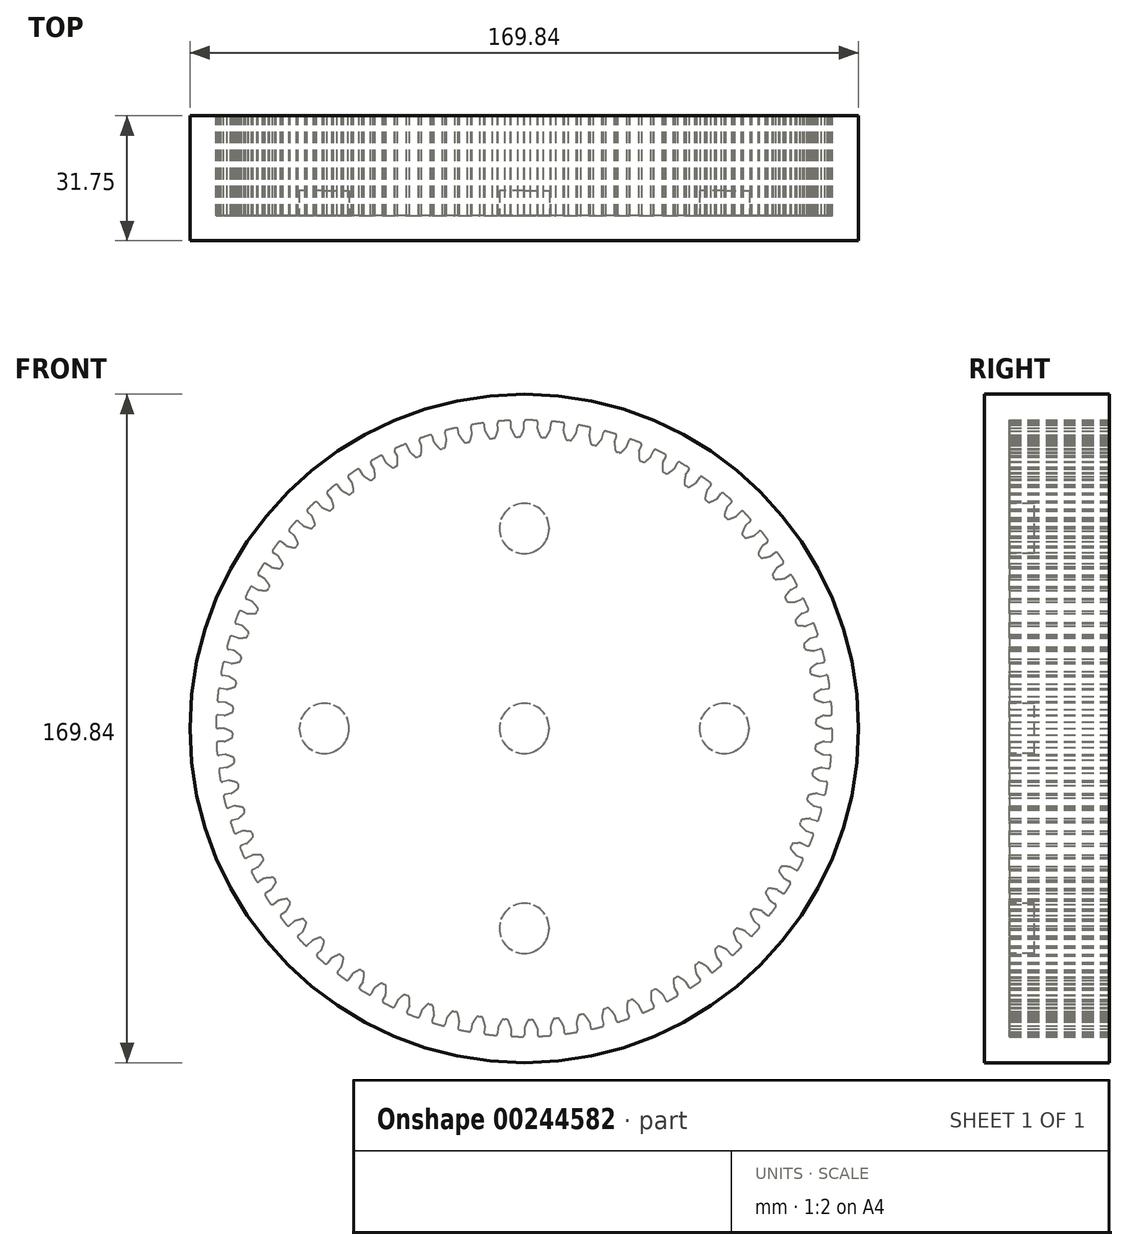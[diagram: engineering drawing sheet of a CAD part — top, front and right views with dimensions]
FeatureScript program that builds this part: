
annotation { "Feature Type Name" : "Feature", "Feature Type Description" : "" }
export const myFeature = defineFeature(function(context is Context, id is Id, definition is map)
    precondition{}
    {
        {
            var Q0;
            Q0=qCreatedBy(makeId("Front.planeOp"),FACE);
            var sketch = newSketch(context, id + "F0", { "sketchPlane" : qUnion([Q0])});
            skArc(sketch, "E0", {"start": v(-3.9, 78.22) * mm, "mid": v(-5.12, 78.15) * mm, "end": v(-6.35, 78.06) * mm});
            skArc(sketch, "E1.MirrorCS", {"start": v(-0.04, 76.1) * mm, "mid": v(-0.4, 75.22) * mm, "end": v(-0.82, 74.36) * mm});
            skPoint(sketch, "E2.end.orphan", {"position": v(-0.97, 78.31) * mm});
            skLineSegment(sketch, "E3", {"start": v(0, 76.3) * mm, "end": v(-0.03, 77.8) * mm});
            skLineSegment(sketch, "E4", {"start": v(-1.28, 74.09) * mm, "end": v(-1.62, 74.09) * mm});
            skLineSegment(sketch, "E5.MirrorCS", {"start": v(-3.33, 76.23) * mm, "end": v(-3.36, 77.73) * mm});
            skArc(sketch, "E6.MirrorCS", {"start": v(-3.28, 76.03) * mm, "mid": v(-2.87, 75.17) * mm, "end": v(-2.42, 74.33) * mm});
            skLineSegment(sketch, "E7.MirrorCS", {"start": v(-1.96, 74.07) * mm, "end": v(-1.62, 74.09) * mm});
            skPoint(sketch, "E8.visualSharp", {"position": v(-3.37, 78.25) * mm});
            skPoint(sketch, "E9.visualSharp", {"position": v(-0.05, 78.32) * mm});
            skArc(sketch, "E9.filletArc", {"start": v(0.48, 78.32) * mm, "mid": v(0.11, 78.17) * mm, "end": v(-0.03, 77.8) * mm});
            skPoint(sketch, "E10.visualSharp", {"position": v(0, 76.2) * mm});
            skArc(sketch, "E10.filletArc", {"start": v(-0.04, 76.1) * mm, "mid": v(0, 76.2) * mm, "end": v(0, 76.3) * mm});
            skPoint(sketch, "E11.visualSharp", {"position": v(-0.97, 74.09) * mm});
            skArc(sketch, "E11.filletArc", {"start": v(-1.28, 74.09) * mm, "mid": v(-1, 74.16) * mm, "end": v(-0.82, 74.36) * mm});
            skPoint(sketch, "E12.visualSharp", {"position": v(-2.27, 74.06) * mm});
            skArc(sketch, "E12.filletArc", {"start": v(-2.42, 74.33) * mm, "mid": v(-2.23, 74.13) * mm, "end": v(-1.96, 74.07) * mm});
            skPoint(sketch, "E13.visualSharp", {"position": v(-3.32, 76.13) * mm});
            skArc(sketch, "E13.filletArc", {"start": v(-3.33, 76.23) * mm, "mid": v(-3.31, 76.13) * mm, "end": v(-3.28, 76.03) * mm});
            skArc(sketch, "E14.filletArc", {"start": v(-3.36, 77.73) * mm, "mid": v(-3.52, 78.09) * mm, "end": v(-3.9, 78.22) * mm});
            skArc(sketch, "E15.1.0", {"start": v(-10.12, 77.14) * mm, "mid": v(-10.31, 77.48) * mm, "end": v(-10.7, 77.59) * mm});
            skLineSegment(sketch, "E15.1.1", {"start": v(-9.96, 75.65) * mm, "end": v(-10.12, 77.14) * mm});
            skArc(sketch, "E15.1.2", {"start": v(-9.96, 75.65) * mm, "mid": v(-9.94, 75.55) * mm, "end": v(-9.9, 75.46) * mm});
            skArc(sketch, "E15.1.3", {"start": v(-6.67, 75.81) * mm, "mid": v(-6.65, 75.91) * mm, "end": v(-6.65, 76.01) * mm});
            skLineSegment(sketch, "E15.1.4", {"start": v(-6.65, 76.01) * mm, "end": v(-6.82, 77.5) * mm});
            skArc(sketch, "E15.1.5", {"start": v(-6.35, 78.06) * mm, "mid": v(-6.7, 77.88) * mm, "end": v(-6.82, 77.5) * mm});
            skArc(sketch, "E15.1.6", {"start": v(-6.67, 75.81) * mm, "mid": v(-6.96, 74.9) * mm, "end": v(-7.3, 74) * mm});
            skArc(sketch, "E15.1.7", {"start": v(-9.9, 75.46) * mm, "mid": v(-9.42, 74.63) * mm, "end": v(-8.9, 73.83) * mm});
            skArc(sketch, "E15.1.8", {"start": v(-8.9, 73.83) * mm, "mid": v(-8.68, 73.66) * mm, "end": v(-8.4, 73.62) * mm});
            skLineSegment(sketch, "E15.1.9", {"start": v(-8.4, 73.62) * mm, "end": v(-8.07, 73.67) * mm});
            skLineSegment(sketch, "E15.1.10", {"start": v(-7.73, 73.7) * mm, "end": v(-8.07, 73.67) * mm});
            skArc(sketch, "E15.1.11", {"start": v(-7.73, 73.7) * mm, "mid": v(-7.47, 73.8) * mm, "end": v(-7.3, 74) * mm});
            skArc(sketch, "E15.2.0", {"start": v(-16.8, 75.96) * mm, "mid": v(-17.03, 76.3) * mm, "end": v(-17.42, 76.36) * mm});
            skLineSegment(sketch, "E15.2.1", {"start": v(-16.51, 74.5) * mm, "end": v(-16.8, 75.96) * mm});
            skArc(sketch, "E15.2.2", {"start": v(-16.51, 74.5) * mm, "mid": v(-16.48, 74.4) * mm, "end": v(-16.44, 74.3) * mm});
            skArc(sketch, "E15.2.3", {"start": v(-13.25, 74.94) * mm, "mid": v(-13.24, 75.04) * mm, "end": v(-13.25, 75.14) * mm});
            skLineSegment(sketch, "E15.2.4", {"start": v(-13.25, 75.14) * mm, "end": v(-13.54, 76.61) * mm});
            skArc(sketch, "E15.2.5", {"start": v(-13.13, 77.21) * mm, "mid": v(-13.46, 77) * mm, "end": v(-13.54, 76.61) * mm});
            skArc(sketch, "E15.2.6", {"start": v(-13.25, 74.94) * mm, "mid": v(-13.46, 74.01) * mm, "end": v(-13.72, 73.1) * mm});
            skArc(sketch, "E15.2.7", {"start": v(-16.44, 74.3) * mm, "mid": v(-15.88, 73.53) * mm, "end": v(-15.3, 72.78) * mm});
            skArc(sketch, "E15.2.8", {"start": v(-15.3, 72.78) * mm, "mid": v(-15.07, 72.62) * mm, "end": v(-14.8, 72.6) * mm});
            skLineSegment(sketch, "E15.2.9", {"start": v(-14.8, 72.6) * mm, "end": v(-14.46, 72.68) * mm});
            skLineSegment(sketch, "E15.2.10", {"start": v(-14.12, 72.74) * mm, "end": v(-14.46, 72.68) * mm});
            skArc(sketch, "E15.2.11", {"start": v(-14.12, 72.74) * mm, "mid": v(-13.87, 72.86) * mm, "end": v(-13.72, 73.1) * mm});
            skArc(sketch, "E15.3.0", {"start": v(-23.36, 74.21) * mm, "mid": v(-23.61, 74.52) * mm, "end": v(-24, 74.55) * mm});
            skLineSegment(sketch, "E15.3.1", {"start": v(-22.94, 72.77) * mm, "end": v(-23.36, 74.21) * mm});
            skArc(sketch, "E15.3.2", {"start": v(-22.94, 72.77) * mm, "mid": v(-22.9, 72.68) * mm, "end": v(-22.85, 72.6) * mm});
            skArc(sketch, "E15.3.3", {"start": v(-19.73, 73.5) * mm, "mid": v(-19.73, 73.6) * mm, "end": v(-19.75, 73.7) * mm});
            skLineSegment(sketch, "E15.3.4", {"start": v(-19.75, 73.7) * mm, "end": v(-20.17, 75.14) * mm});
            skArc(sketch, "E15.3.5", {"start": v(-19.81, 75.77) * mm, "mid": v(-20.12, 75.53) * mm, "end": v(-20.17, 75.14) * mm});
            skArc(sketch, "E15.3.6", {"start": v(-19.73, 73.5) * mm, "mid": v(-19.86, 72.56) * mm, "end": v(-20.04, 71.62) * mm});
            skArc(sketch, "E15.3.7", {"start": v(-22.85, 72.6) * mm, "mid": v(-22.23, 71.86) * mm, "end": v(-21.58, 71.17) * mm});
            skArc(sketch, "E15.3.8", {"start": v(-21.58, 71.17) * mm, "mid": v(-21.34, 71.03) * mm, "end": v(-21.06, 71.04) * mm});
            skLineSegment(sketch, "E15.3.9", {"start": v(-21.06, 71.04) * mm, "end": v(-20.74, 71.15) * mm});
            skLineSegment(sketch, "E15.3.10", {"start": v(-20.4, 71.23) * mm, "end": v(-20.74, 71.15) * mm});
            skArc(sketch, "E15.3.11", {"start": v(-20.4, 71.23) * mm, "mid": v(-20.17, 71.37) * mm, "end": v(-20.04, 71.62) * mm});
            skArc(sketch, "E15.4.0", {"start": v(-29.74, 71.9) * mm, "mid": v(-30.02, 72.18) * mm, "end": v(-30.41, 72.18) * mm});
            skLineSegment(sketch, "E15.4.1", {"start": v(-29.2, 70.5) * mm, "end": v(-29.74, 71.9) * mm});
            skArc(sketch, "E15.4.2", {"start": v(-29.2, 70.5) * mm, "mid": v(-29.15, 70.4) * mm, "end": v(-29.09, 70.33) * mm});
            skArc(sketch, "E15.4.3", {"start": v(-26.06, 71.5) * mm, "mid": v(-26.07, 71.6) * mm, "end": v(-26.1, 71.7) * mm});
            skLineSegment(sketch, "E15.4.4", {"start": v(-26.1, 71.7) * mm, "end": v(-26.64, 73.1) * mm});
            skArc(sketch, "E15.4.5", {"start": v(-26.34, 73.76) * mm, "mid": v(-26.63, 73.5) * mm, "end": v(-26.64, 73.1) * mm});
            skArc(sketch, "E15.4.6", {"start": v(-26.06, 71.5) * mm, "mid": v(-26.11, 70.55) * mm, "end": v(-26.2, 69.6) * mm});
            skArc(sketch, "E15.4.7", {"start": v(-29.09, 70.33) * mm, "mid": v(-28.41, 69.65) * mm, "end": v(-27.7, 69.02) * mm});
            skArc(sketch, "E15.4.8", {"start": v(-27.7, 69.02) * mm, "mid": v(-27.45, 68.9) * mm, "end": v(-27.17, 68.94) * mm});
            skLineSegment(sketch, "E15.4.9", {"start": v(-27.17, 68.94) * mm, "end": v(-26.86, 69.07) * mm});
            skLineSegment(sketch, "E15.4.10", {"start": v(-26.54, 69.18) * mm, "end": v(-26.86, 69.07) * mm});
            skArc(sketch, "E15.4.11", {"start": v(-26.54, 69.18) * mm, "mid": v(-26.31, 69.34) * mm, "end": v(-26.2, 69.6) * mm});
            skArc(sketch, "E15.5.0", {"start": v(-35.9, 69.03) * mm, "mid": v(-36.2, 69.28) * mm, "end": v(-36.59, 69.25) * mm});
            skLineSegment(sketch, "E15.5.1", {"start": v(-35.23, 67.68) * mm, "end": v(-35.9, 69.03) * mm});
            skArc(sketch, "E15.5.2", {"start": v(-35.23, 67.68) * mm, "mid": v(-35.18, 67.6) * mm, "end": v(-35.1, 67.52) * mm});
            skArc(sketch, "E15.5.3", {"start": v(-32.2, 68.96) * mm, "mid": v(-32.21, 69.06) * mm, "end": v(-32.25, 69.15) * mm});
            skLineSegment(sketch, "E15.5.4", {"start": v(-32.25, 69.15) * mm, "end": v(-32.91, 70.5) * mm});
            skArc(sketch, "E15.5.5", {"start": v(-32.67, 71.18) * mm, "mid": v(-32.93, 70.9) * mm, "end": v(-32.91, 70.5) * mm});
            skArc(sketch, "E15.5.6", {"start": v(-32.2, 68.96) * mm, "mid": v(-32.16, 68) * mm, "end": v(-32.17, 67.05) * mm});
            skArc(sketch, "E15.5.7", {"start": v(-35.1, 67.52) * mm, "mid": v(-34.37, 66.91) * mm, "end": v(-33.6, 66.34) * mm});
            skArc(sketch, "E15.5.8", {"start": v(-33.6, 66.34) * mm, "mid": v(-33.35, 66.25) * mm, "end": v(-33.08, 66.3) * mm});
            skLineSegment(sketch, "E15.5.9", {"start": v(-33.08, 66.3) * mm, "end": v(-32.78, 66.46) * mm});
            skLineSegment(sketch, "E15.5.10", {"start": v(-32.47, 66.6) * mm, "end": v(-32.78, 66.46) * mm});
            skArc(sketch, "E15.5.11", {"start": v(-32.47, 66.6) * mm, "mid": v(-32.26, 66.79) * mm, "end": v(-32.17, 67.05) * mm});
            skArc(sketch, "E15.6.0", {"start": v(-41.77, 65.63) * mm, "mid": v(-42.1, 65.87) * mm, "end": v(-42.48, 65.8) * mm});
            skLineSegment(sketch, "E15.6.1", {"start": v(-41, 64.35) * mm, "end": v(-41.77, 65.63) * mm});
            skArc(sketch, "E15.6.2", {"start": v(-41, 64.35) * mm, "mid": v(-40.93, 64.27) * mm, "end": v(-40.86, 64.2) * mm});
            skArc(sketch, "E15.6.3", {"start": v(-38.08, 65.9) * mm, "mid": v(-38.1, 65.99) * mm, "end": v(-38.15, 66.08) * mm});
            skLineSegment(sketch, "E15.6.4", {"start": v(-38.15, 66.08) * mm, "end": v(-38.93, 67.36) * mm});
            skArc(sketch, "E15.6.5", {"start": v(-38.75, 68.06) * mm, "mid": v(-38.99, 67.75) * mm, "end": v(-38.93, 67.36) * mm});
            skArc(sketch, "E15.6.6", {"start": v(-38.08, 65.9) * mm, "mid": v(-37.96, 64.94) * mm, "end": v(-37.9, 64) * mm});
            skArc(sketch, "E15.6.7", {"start": v(-40.86, 64.2) * mm, "mid": v(-40.07, 63.66) * mm, "end": v(-39.26, 63.16) * mm});
            skArc(sketch, "E15.6.8", {"start": v(-39.26, 63.16) * mm, "mid": v(-39, 63.09) * mm, "end": v(-38.73, 63.17) * mm});
            skLineSegment(sketch, "E15.6.9", {"start": v(-38.73, 63.17) * mm, "end": v(-38.44, 63.35) * mm});
            skLineSegment(sketch, "E15.6.10", {"start": v(-38.15, 63.52) * mm, "end": v(-38.44, 63.35) * mm});
            skArc(sketch, "E15.6.11", {"start": v(-38.15, 63.52) * mm, "mid": v(-37.95, 63.72) * mm, "end": v(-37.9, 64) * mm});
            skArc(sketch, "E15.7.0", {"start": v(-47.33, 61.74) * mm, "mid": v(-47.67, 61.95) * mm, "end": v(-48.06, 61.85) * mm});
            skLineSegment(sketch, "E15.7.1", {"start": v(-46.45, 60.53) * mm, "end": v(-47.33, 61.74) * mm});
            skArc(sketch, "E15.7.2", {"start": v(-46.45, 60.53) * mm, "mid": v(-46.38, 60.46) * mm, "end": v(-46.3, 60.4) * mm});
            skArc(sketch, "E15.7.3", {"start": v(-43.68, 62.32) * mm, "mid": v(-43.72, 62.41) * mm, "end": v(-43.77, 62.5) * mm});
            skLineSegment(sketch, "E15.7.4", {"start": v(-43.77, 62.5) * mm, "end": v(-44.65, 63.71) * mm});
            skArc(sketch, "E15.7.5", {"start": v(-44.53, 64.43) * mm, "mid": v(-44.74, 64.1) * mm, "end": v(-44.65, 63.71) * mm});
            skArc(sketch, "E15.7.6", {"start": v(-43.68, 62.32) * mm, "mid": v(-43.48, 61.39) * mm, "end": v(-43.32, 60.44) * mm});
            skArc(sketch, "E15.7.7", {"start": v(-46.3, 60.4) * mm, "mid": v(-45.47, 59.93) * mm, "end": v(-44.62, 59.5) * mm});
            skArc(sketch, "E15.7.8", {"start": v(-44.62, 59.5) * mm, "mid": v(-44.35, 59.45) * mm, "end": v(-44.09, 59.55) * mm});
            skLineSegment(sketch, "E15.7.9", {"start": v(-44.09, 59.55) * mm, "end": v(-43.82, 59.76) * mm});
            skLineSegment(sketch, "E15.7.10", {"start": v(-43.54, 59.96) * mm, "end": v(-43.82, 59.76) * mm});
            skArc(sketch, "E15.7.11", {"start": v(-43.54, 59.96) * mm, "mid": v(-43.36, 60.17) * mm, "end": v(-43.32, 60.44) * mm});
            skArc(sketch, "E15.8.0", {"start": v(-52.54, 57.38) * mm, "mid": v(-52.9, 57.56) * mm, "end": v(-53.26, 57.42) * mm});
            skLineSegment(sketch, "E15.8.1", {"start": v(-51.55, 56.26) * mm, "end": v(-52.54, 57.38) * mm});
            skArc(sketch, "E15.8.2", {"start": v(-51.55, 56.26) * mm, "mid": v(-51.47, 56.19) * mm, "end": v(-51.39, 56.14) * mm});
            skArc(sketch, "E15.8.3", {"start": v(-48.95, 58.28) * mm, "mid": v(-48.99, 58.37) * mm, "end": v(-49.05, 58.45) * mm});
            skLineSegment(sketch, "E15.8.4", {"start": v(-49.05, 58.45) * mm, "end": v(-50.04, 59.58) * mm});
            skArc(sketch, "E15.8.5", {"start": v(-49.98, 60.3) * mm, "mid": v(-50.16, 59.95) * mm, "end": v(-50.04, 59.58) * mm});
            skArc(sketch, "E15.8.6", {"start": v(-48.95, 58.28) * mm, "mid": v(-48.66, 57.36) * mm, "end": v(-48.43, 56.44) * mm});
            skArc(sketch, "E15.8.7", {"start": v(-51.39, 56.14) * mm, "mid": v(-50.52, 55.74) * mm, "end": v(-49.63, 55.38) * mm});
            skArc(sketch, "E15.8.8", {"start": v(-49.63, 55.38) * mm, "mid": v(-49.36, 55.36) * mm, "end": v(-49.11, 55.48) * mm});
            skLineSegment(sketch, "E15.8.9", {"start": v(-49.11, 55.48) * mm, "end": v(-48.86, 55.72) * mm});
            skLineSegment(sketch, "E15.8.10", {"start": v(-48.6, 55.93) * mm, "end": v(-48.86, 55.72) * mm});
            skArc(sketch, "E15.8.11", {"start": v(-48.6, 55.93) * mm, "mid": v(-48.44, 56.16) * mm, "end": v(-48.43, 56.44) * mm});
            skArc(sketch, "E15.9.0", {"start": v(-57.34, 52.59) * mm, "mid": v(-57.7, 52.73) * mm, "end": v(-58.06, 52.56) * mm});
            skLineSegment(sketch, "E15.9.1", {"start": v(-56.25, 51.55) * mm, "end": v(-57.34, 52.59) * mm});
            skArc(sketch, "E15.9.2", {"start": v(-56.25, 51.55) * mm, "mid": v(-56.17, 51.49) * mm, "end": v(-56.09, 51.44) * mm});
            skArc(sketch, "E15.9.3", {"start": v(-53.84, 53.79) * mm, "mid": v(-53.89, 53.88) * mm, "end": v(-53.95, 53.95) * mm});
            skLineSegment(sketch, "E15.9.4", {"start": v(-53.95, 53.95) * mm, "end": v(-55.04, 54.99) * mm});
            skArc(sketch, "E15.9.5", {"start": v(-55.04, 55.72) * mm, "mid": v(-55.2, 55.35) * mm, "end": v(-55.04, 54.99) * mm});
            skArc(sketch, "E15.9.6", {"start": v(-53.84, 53.79) * mm, "mid": v(-53.48, 52.9) * mm, "end": v(-53.16, 52) * mm});
            skArc(sketch, "E15.9.7", {"start": v(-56.09, 51.44) * mm, "mid": v(-55.19, 51.12) * mm, "end": v(-54.27, 50.84) * mm});
            skArc(sketch, "E15.9.8", {"start": v(-54.27, 50.84) * mm, "mid": v(-54, 50.85) * mm, "end": v(-53.76, 51) * mm});
            skLineSegment(sketch, "E15.9.9", {"start": v(-53.76, 51) * mm, "end": v(-53.53, 51.25) * mm});
            skLineSegment(sketch, "E15.9.10", {"start": v(-53.29, 51.49) * mm, "end": v(-53.53, 51.25) * mm});
            skArc(sketch, "E15.9.11", {"start": v(-53.29, 51.49) * mm, "mid": v(-53.15, 51.73) * mm, "end": v(-53.16, 52) * mm});
            skArc(sketch, "E15.10.0", {"start": v(-61.7, 47.39) * mm, "mid": v(-62.08, 47.5) * mm, "end": v(-62.42, 47.3) * mm});
            skLineSegment(sketch, "E15.10.1", {"start": v(-60.53, 46.45) * mm, "end": v(-61.7, 47.39) * mm});
            skArc(sketch, "E15.10.2", {"start": v(-60.53, 46.45) * mm, "mid": v(-60.45, 46.4) * mm, "end": v(-60.36, 46.36) * mm});
            skArc(sketch, "E15.10.3", {"start": v(-58.32, 48.9) * mm, "mid": v(-58.38, 48.97) * mm, "end": v(-58.45, 49.04) * mm});
            skLineSegment(sketch, "E15.10.4", {"start": v(-58.45, 49.04) * mm, "end": v(-59.62, 49.98) * mm});
            skArc(sketch, "E15.10.5", {"start": v(-59.7, 50.7) * mm, "mid": v(-59.8, 50.33) * mm, "end": v(-59.62, 49.98) * mm});
            skArc(sketch, "E15.10.6", {"start": v(-58.32, 48.9) * mm, "mid": v(-57.89, 48.04) * mm, "end": v(-57.5, 47.17) * mm});
            skArc(sketch, "E15.10.7", {"start": v(-60.36, 46.36) * mm, "mid": v(-59.43, 46.12) * mm, "end": v(-58.5, 45.92) * mm});
            skArc(sketch, "E15.10.8", {"start": v(-58.5, 45.92) * mm, "mid": v(-58.22, 45.95) * mm, "end": v(-58, 46.11) * mm});
            skLineSegment(sketch, "E15.10.9", {"start": v(-58, 46.11) * mm, "end": v(-57.8, 46.38) * mm});
            skLineSegment(sketch, "E15.10.10", {"start": v(-57.57, 46.65) * mm, "end": v(-57.8, 46.38) * mm});
            skArc(sketch, "E15.10.11", {"start": v(-57.57, 46.65) * mm, "mid": v(-57.46, 46.9) * mm, "end": v(-57.5, 47.17) * mm});
            skArc(sketch, "E15.11.0", {"start": v(-65.6, 41.83) * mm, "mid": v(-65.99, 41.9) * mm, "end": v(-66.3, 41.68) * mm});
            skLineSegment(sketch, "E15.11.1", {"start": v(-64.35, 41) * mm, "end": v(-65.6, 41.83) * mm});
            skArc(sketch, "E15.11.2", {"start": v(-64.35, 41) * mm, "mid": v(-64.26, 40.95) * mm, "end": v(-64.17, 40.92) * mm});
            skArc(sketch, "E15.11.3", {"start": v(-62.36, 43.62) * mm, "mid": v(-62.43, 43.7) * mm, "end": v(-62.5, 43.76) * mm});
            skLineSegment(sketch, "E15.11.4", {"start": v(-62.5, 43.76) * mm, "end": v(-63.75, 44.6) * mm});
            skArc(sketch, "E15.11.5", {"start": v(-63.88, 45.31) * mm, "mid": v(-63.97, 44.93) * mm, "end": v(-63.75, 44.6) * mm});
            skArc(sketch, "E15.11.6", {"start": v(-62.36, 43.62) * mm, "mid": v(-61.85, 42.81) * mm, "end": v(-61.39, 41.98) * mm});
            skArc(sketch, "E15.11.7", {"start": v(-64.17, 40.92) * mm, "mid": v(-63.22, 40.76) * mm, "end": v(-62.28, 40.65) * mm});
            skArc(sketch, "E15.11.8", {"start": v(-62.28, 40.65) * mm, "mid": v(-62, 40.7) * mm, "end": v(-61.8, 40.88) * mm});
            skLineSegment(sketch, "E15.11.9", {"start": v(-61.8, 40.88) * mm, "end": v(-61.62, 41.17) * mm});
            skLineSegment(sketch, "E15.11.10", {"start": v(-61.42, 41.45) * mm, "end": v(-61.62, 41.17) * mm});
            skArc(sketch, "E15.11.11", {"start": v(-61.42, 41.45) * mm, "mid": v(-61.33, 41.71) * mm, "end": v(-61.39, 41.98) * mm});
            skArc(sketch, "E15.12.0", {"start": v(-69, 35.96) * mm, "mid": v(-69.39, 36) * mm, "end": v(-69.7, 35.74) * mm});
            skLineSegment(sketch, "E15.12.1", {"start": v(-67.68, 35.23) * mm, "end": v(-69, 35.96) * mm});
            skArc(sketch, "E15.12.2", {"start": v(-67.68, 35.23) * mm, "mid": v(-67.59, 35.2) * mm, "end": v(-67.49, 35.17) * mm});
            skArc(sketch, "E15.12.3", {"start": v(-65.93, 38.02) * mm, "mid": v(-66, 38.1) * mm, "end": v(-66.08, 38.15) * mm});
            skLineSegment(sketch, "E15.12.4", {"start": v(-66.08, 38.15) * mm, "end": v(-67.4, 38.87) * mm});
            skArc(sketch, "E15.12.5", {"start": v(-67.59, 39.57) * mm, "mid": v(-67.64, 39.18) * mm, "end": v(-67.4, 38.87) * mm});
            skArc(sketch, "E15.12.6", {"start": v(-65.93, 38.02) * mm, "mid": v(-65.35, 37.26) * mm, "end": v(-64.81, 36.47) * mm});
            skArc(sketch, "E15.12.7", {"start": v(-67.49, 35.17) * mm, "mid": v(-66.54, 35.1) * mm, "end": v(-65.58, 35.06) * mm});
            skArc(sketch, "E15.12.8", {"start": v(-65.58, 35.06) * mm, "mid": v(-65.32, 35.14) * mm, "end": v(-65.13, 35.34) * mm});
            skLineSegment(sketch, "E15.12.9", {"start": v(-65.13, 35.34) * mm, "end": v(-64.97, 35.64) * mm});
            skLineSegment(sketch, "E15.12.10", {"start": v(-64.8, 35.94) * mm, "end": v(-64.97, 35.64) * mm});
            skArc(sketch, "E15.12.11", {"start": v(-64.8, 35.94) * mm, "mid": v(-64.73, 36.2) * mm, "end": v(-64.81, 36.47) * mm});
            skArc(sketch, "E15.13.0", {"start": v(-71.86, 29.8) * mm, "mid": v(-72.26, 29.81) * mm, "end": v(-72.54, 29.53) * mm});
            skLineSegment(sketch, "E15.13.1", {"start": v(-70.5, 29.2) * mm, "end": v(-71.86, 29.8) * mm});
            skArc(sketch, "E15.13.2", {"start": v(-70.5, 29.2) * mm, "mid": v(-70.4, 29.17) * mm, "end": v(-70.3, 29.16) * mm});
            skArc(sketch, "E15.13.3", {"start": v(-68.99, 32.13) * mm, "mid": v(-69.07, 32.2) * mm, "end": v(-69.15, 32.24) * mm});
            skLineSegment(sketch, "E15.13.4", {"start": v(-69.15, 32.24) * mm, "end": v(-70.53, 32.85) * mm});
            skArc(sketch, "E15.13.5", {"start": v(-70.78, 33.53) * mm, "mid": v(-70.8, 33.14) * mm, "end": v(-70.53, 32.85) * mm});
            skArc(sketch, "E15.13.6", {"start": v(-68.99, 32.13) * mm, "mid": v(-68.35, 31.42) * mm, "end": v(-67.74, 30.68) * mm});
            skArc(sketch, "E15.13.7", {"start": v(-70.3, 29.16) * mm, "mid": v(-69.34, 29.16) * mm, "end": v(-68.39, 29.22) * mm});
            skArc(sketch, "E15.13.8", {"start": v(-68.39, 29.22) * mm, "mid": v(-68.13, 29.31) * mm, "end": v(-67.96, 29.53) * mm});
            skLineSegment(sketch, "E15.13.9", {"start": v(-67.96, 29.53) * mm, "end": v(-67.83, 29.85) * mm});
            skLineSegment(sketch, "E15.13.10", {"start": v(-67.68, 30.15) * mm, "end": v(-67.83, 29.85) * mm});
            skArc(sketch, "E15.13.11", {"start": v(-67.68, 30.15) * mm, "mid": v(-67.64, 30.43) * mm, "end": v(-67.74, 30.68) * mm});
            skArc(sketch, "E15.14.0", {"start": v(-74.19, 23.43) * mm, "mid": v(-74.58, 23.4) * mm, "end": v(-74.84, 23.1) * mm});
            skLineSegment(sketch, "E15.14.1", {"start": v(-72.77, 22.95) * mm, "end": v(-74.19, 23.43) * mm});
            skArc(sketch, "E15.14.2", {"start": v(-72.77, 22.95) * mm, "mid": v(-72.67, 22.92) * mm, "end": v(-72.57, 22.92) * mm});
            skArc(sketch, "E15.14.3", {"start": v(-71.53, 26) * mm, "mid": v(-71.6, 26.05) * mm, "end": v(-71.7, 26.1) * mm});
            skLineSegment(sketch, "E15.14.4", {"start": v(-71.7, 26.1) * mm, "end": v(-73.12, 26.58) * mm});
            skArc(sketch, "E15.14.5", {"start": v(-73.43, 27.23) * mm, "mid": v(-73.42, 26.84) * mm, "end": v(-73.12, 26.58) * mm});
            skArc(sketch, "E15.14.6", {"start": v(-71.53, 26) * mm, "mid": v(-70.83, 25.35) * mm, "end": v(-70.16, 24.66) * mm});
            skArc(sketch, "E15.14.7", {"start": v(-72.57, 22.92) * mm, "mid": v(-71.62, 23) * mm, "end": v(-70.67, 23.14) * mm});
            skArc(sketch, "E15.14.8", {"start": v(-70.67, 23.14) * mm, "mid": v(-70.42, 23.26) * mm, "end": v(-70.27, 23.5) * mm});
            skLineSegment(sketch, "E15.14.9", {"start": v(-70.27, 23.5) * mm, "end": v(-70.17, 23.82) * mm});
            skLineSegment(sketch, "E15.14.10", {"start": v(-70.05, 24.14) * mm, "end": v(-70.17, 23.82) * mm});
            skArc(sketch, "E15.14.11", {"start": v(-70.05, 24.14) * mm, "mid": v(-70.03, 24.42) * mm, "end": v(-70.16, 24.66) * mm});
            skArc(sketch, "E15.15.0", {"start": v(-75.95, 16.87) * mm, "mid": v(-76.34, 16.81) * mm, "end": v(-76.57, 16.49) * mm});
            skLineSegment(sketch, "E15.15.1", {"start": v(-74.5, 16.52) * mm, "end": v(-75.95, 16.87) * mm});
            skArc(sketch, "E15.15.2", {"start": v(-74.5, 16.52) * mm, "mid": v(-74.4, 16.5) * mm, "end": v(-74.3, 16.5) * mm});
            skArc(sketch, "E15.15.3", {"start": v(-73.52, 19.66) * mm, "mid": v(-73.6, 19.71) * mm, "end": v(-73.7, 19.75) * mm});
            skLineSegment(sketch, "E15.15.4", {"start": v(-73.7, 19.75) * mm, "end": v(-75.16, 20.1) * mm});
            skArc(sketch, "E15.15.5", {"start": v(-75.53, 20.73) * mm, "mid": v(-75.48, 20.34) * mm, "end": v(-75.16, 20.1) * mm});
            skArc(sketch, "E15.15.6", {"start": v(-73.52, 19.66) * mm, "mid": v(-72.77, 19.08) * mm, "end": v(-72.04, 18.45) * mm});
            skArc(sketch, "E15.15.7", {"start": v(-74.3, 16.5) * mm, "mid": v(-73.35, 16.68) * mm, "end": v(-72.42, 16.9) * mm});
            skArc(sketch, "E15.15.8", {"start": v(-72.42, 16.9) * mm, "mid": v(-72.18, 17.04) * mm, "end": v(-72.05, 17.28) * mm});
            skLineSegment(sketch, "E15.15.9", {"start": v(-72.05, 17.28) * mm, "end": v(-71.98, 17.61) * mm});
            skLineSegment(sketch, "E15.15.10", {"start": v(-71.9, 17.94) * mm, "end": v(-71.98, 17.61) * mm});
            skArc(sketch, "E15.15.11", {"start": v(-71.9, 17.94) * mm, "mid": v(-71.9, 18.22) * mm, "end": v(-72.04, 18.45) * mm});
            skArc(sketch, "E15.16.0", {"start": v(-77.13, 10.19) * mm, "mid": v(-77.51, 10.1) * mm, "end": v(-77.71, 9.75) * mm});
            skLineSegment(sketch, "E15.16.1", {"start": v(-75.65, 9.96) * mm, "end": v(-77.13, 10.19) * mm});
            skArc(sketch, "E15.16.2", {"start": v(-75.65, 9.96) * mm, "mid": v(-75.55, 9.96) * mm, "end": v(-75.45, 9.97) * mm});
            skArc(sketch, "E15.16.3", {"start": v(-74.95, 13.18) * mm, "mid": v(-75.05, 13.22) * mm, "end": v(-75.14, 13.25) * mm});
            skLineSegment(sketch, "E15.16.4", {"start": v(-75.14, 13.25) * mm, "end": v(-76.62, 13.48) * mm});
            skArc(sketch, "E15.16.5", {"start": v(-77.05, 14.07) * mm, "mid": v(-76.96, 13.68) * mm, "end": v(-76.62, 13.48) * mm});
            skArc(sketch, "E15.16.6", {"start": v(-74.95, 13.18) * mm, "mid": v(-74.15, 12.66) * mm, "end": v(-73.38, 12.1) * mm});
            skArc(sketch, "E15.16.7", {"start": v(-75.45, 9.97) * mm, "mid": v(-74.53, 10.22) * mm, "end": v(-73.62, 10.52) * mm});
            skArc(sketch, "E15.16.8", {"start": v(-73.62, 10.52) * mm, "mid": v(-73.4, 10.68) * mm, "end": v(-73.29, 10.93) * mm});
            skLineSegment(sketch, "E15.16.9", {"start": v(-73.29, 10.93) * mm, "end": v(-73.24, 11.27) * mm});
            skLineSegment(sketch, "E15.16.10", {"start": v(-73.18, 11.6) * mm, "end": v(-73.24, 11.27) * mm});
            skArc(sketch, "E15.16.11", {"start": v(-73.18, 11.6) * mm, "mid": v(-73.2, 11.88) * mm, "end": v(-73.38, 12.1) * mm});
            skArc(sketch, "E15.17.0", {"start": v(-77.72, 3.43) * mm, "mid": v(-78.1, 3.3) * mm, "end": v(-78.27, 2.94) * mm});
            skLineSegment(sketch, "E15.17.1", {"start": v(-76.23, 3.33) * mm, "end": v(-77.72, 3.43) * mm});
            skArc(sketch, "E15.17.2", {"start": v(-76.23, 3.33) * mm, "mid": v(-76.13, 3.33) * mm, "end": v(-76.03, 3.36) * mm});
            skArc(sketch, "E15.17.3", {"start": v(-75.82, 6.6) * mm, "mid": v(-75.91, 6.63) * mm, "end": v(-76.01, 6.65) * mm});
            skLineSegment(sketch, "E15.17.4", {"start": v(-76.01, 6.65) * mm, "end": v(-77.5, 6.75) * mm});
            skArc(sketch, "E15.17.5", {"start": v(-77.98, 7.3) * mm, "mid": v(-77.86, 6.92) * mm, "end": v(-77.5, 6.75) * mm});
            skArc(sketch, "E15.17.6", {"start": v(-75.82, 6.6) * mm, "mid": v(-74.97, 6.15) * mm, "end": v(-74.15, 5.66) * mm});
            skArc(sketch, "E15.17.7", {"start": v(-76.03, 3.36) * mm, "mid": v(-75.13, 3.69) * mm, "end": v(-74.26, 4.06) * mm});
            skArc(sketch, "E15.17.8", {"start": v(-74.26, 4.06) * mm, "mid": v(-74.05, 4.24) * mm, "end": v(-73.96, 4.5) * mm});
            skLineSegment(sketch, "E15.17.9", {"start": v(-73.96, 4.5) * mm, "end": v(-73.95, 4.85) * mm});
            skLineSegment(sketch, "E15.17.10", {"start": v(-73.92, 5.19) * mm, "end": v(-73.95, 4.85) * mm});
            skArc(sketch, "E15.17.11", {"start": v(-73.92, 5.19) * mm, "mid": v(-73.97, 5.46) * mm, "end": v(-74.15, 5.66) * mm});
            skArc(sketch, "E15.18.0", {"start": v(-77.73, -3.36) * mm, "mid": v(-78.09, -3.52) * mm, "end": v(-78.22, -3.9) * mm});
            skLineSegment(sketch, "E15.18.1", {"start": v(-76.23, -3.33) * mm, "end": v(-77.73, -3.36) * mm});
            skArc(sketch, "E15.18.2", {"start": v(-76.23, -3.33) * mm, "mid": v(-76.13, -3.31) * mm, "end": v(-76.03, -3.28) * mm});
            skArc(sketch, "E15.18.3", {"start": v(-76.1, -0.04) * mm, "mid": v(-76.2, 0) * mm, "end": v(-76.3, 0) * mm});
            skLineSegment(sketch, "E15.18.4", {"start": v(-76.3, 0) * mm, "end": v(-77.8, -0.03) * mm});
            skArc(sketch, "E15.18.5", {"start": v(-78.32, 0.48) * mm, "mid": v(-78.17, 0.11) * mm, "end": v(-77.8, -0.03) * mm});
            skArc(sketch, "E15.18.6", {"start": v(-76.1, -0.04) * mm, "mid": v(-75.22, -0.4) * mm, "end": v(-74.36, -0.82) * mm});
            skArc(sketch, "E15.18.7", {"start": v(-76.03, -3.28) * mm, "mid": v(-75.17, -2.87) * mm, "end": v(-74.33, -2.42) * mm});
            skArc(sketch, "E15.18.8", {"start": v(-74.33, -2.42) * mm, "mid": v(-74.13, -2.23) * mm, "end": v(-74.07, -1.96) * mm});
            skLineSegment(sketch, "E15.18.9", {"start": v(-74.07, -1.96) * mm, "end": v(-74.09, -1.62) * mm});
            skLineSegment(sketch, "E15.18.10", {"start": v(-74.09, -1.28) * mm, "end": v(-74.09, -1.62) * mm});
            skArc(sketch, "E15.18.11", {"start": v(-74.09, -1.28) * mm, "mid": v(-74.16, -1) * mm, "end": v(-74.36, -0.82) * mm});
            skArc(sketch, "E15.19.0", {"start": v(-77.14, -10.12) * mm, "mid": v(-77.48, -10.31) * mm, "end": v(-77.59, -10.7) * mm});
            skLineSegment(sketch, "E15.19.1", {"start": v(-75.65, -9.96) * mm, "end": v(-77.14, -10.12) * mm});
            skArc(sketch, "E15.19.2", {"start": v(-75.65, -9.96) * mm, "mid": v(-75.55, -9.94) * mm, "end": v(-75.46, -9.9) * mm});
            skArc(sketch, "E15.19.3", {"start": v(-75.81, -6.67) * mm, "mid": v(-75.91, -6.65) * mm, "end": v(-76.01, -6.65) * mm});
            skLineSegment(sketch, "E15.19.4", {"start": v(-76.01, -6.65) * mm, "end": v(-77.5, -6.82) * mm});
            skArc(sketch, "E15.19.5", {"start": v(-78.06, -6.35) * mm, "mid": v(-77.88, -6.7) * mm, "end": v(-77.5, -6.82) * mm});
            skArc(sketch, "E15.19.6", {"start": v(-75.81, -6.67) * mm, "mid": v(-74.9, -6.96) * mm, "end": v(-74, -7.3) * mm});
            skArc(sketch, "E15.19.7", {"start": v(-75.46, -9.9) * mm, "mid": v(-74.63, -9.42) * mm, "end": v(-73.83, -8.9) * mm});
            skArc(sketch, "E15.19.8", {"start": v(-73.83, -8.9) * mm, "mid": v(-73.66, -8.68) * mm, "end": v(-73.62, -8.4) * mm});
            skLineSegment(sketch, "E15.19.9", {"start": v(-73.62, -8.4) * mm, "end": v(-73.67, -8.07) * mm});
            skLineSegment(sketch, "E15.19.10", {"start": v(-73.7, -7.73) * mm, "end": v(-73.67, -8.07) * mm});
            skArc(sketch, "E15.19.11", {"start": v(-73.7, -7.73) * mm, "mid": v(-73.8, -7.47) * mm, "end": v(-74, -7.3) * mm});
            skArc(sketch, "E15.20.0", {"start": v(-75.96, -16.8) * mm, "mid": v(-76.3, -17.03) * mm, "end": v(-76.36, -17.42) * mm});
            skLineSegment(sketch, "E15.20.1", {"start": v(-74.5, -16.51) * mm, "end": v(-75.96, -16.8) * mm});
            skArc(sketch, "E15.20.2", {"start": v(-74.5, -16.51) * mm, "mid": v(-74.4, -16.48) * mm, "end": v(-74.3, -16.44) * mm});
            skArc(sketch, "E15.20.3", {"start": v(-74.94, -13.25) * mm, "mid": v(-75.04, -13.24) * mm, "end": v(-75.14, -13.25) * mm});
            skLineSegment(sketch, "E15.20.4", {"start": v(-75.14, -13.25) * mm, "end": v(-76.61, -13.54) * mm});
            skArc(sketch, "E15.20.5", {"start": v(-77.21, -13.13) * mm, "mid": v(-77, -13.46) * mm, "end": v(-76.61, -13.54) * mm});
            skArc(sketch, "E15.20.6", {"start": v(-74.94, -13.25) * mm, "mid": v(-74.01, -13.46) * mm, "end": v(-73.1, -13.72) * mm});
            skArc(sketch, "E15.20.7", {"start": v(-74.3, -16.44) * mm, "mid": v(-73.53, -15.88) * mm, "end": v(-72.78, -15.3) * mm});
            skArc(sketch, "E15.20.8", {"start": v(-72.78, -15.3) * mm, "mid": v(-72.62, -15.07) * mm, "end": v(-72.6, -14.8) * mm});
            skLineSegment(sketch, "E15.20.9", {"start": v(-72.6, -14.8) * mm, "end": v(-72.68, -14.46) * mm});
            skLineSegment(sketch, "E15.20.10", {"start": v(-72.74, -14.12) * mm, "end": v(-72.68, -14.46) * mm});
            skArc(sketch, "E15.20.11", {"start": v(-72.74, -14.12) * mm, "mid": v(-72.86, -13.87) * mm, "end": v(-73.1, -13.72) * mm});
            skArc(sketch, "E15.21.0", {"start": v(-74.21, -23.36) * mm, "mid": v(-74.52, -23.61) * mm, "end": v(-74.55, -24) * mm});
            skLineSegment(sketch, "E15.21.1", {"start": v(-72.77, -22.94) * mm, "end": v(-74.21, -23.36) * mm});
            skArc(sketch, "E15.21.2", {"start": v(-72.77, -22.94) * mm, "mid": v(-72.68, -22.9) * mm, "end": v(-72.6, -22.85) * mm});
            skArc(sketch, "E15.21.3", {"start": v(-73.5, -19.73) * mm, "mid": v(-73.6, -19.73) * mm, "end": v(-73.7, -19.75) * mm});
            skLineSegment(sketch, "E15.21.4", {"start": v(-73.7, -19.75) * mm, "end": v(-75.14, -20.17) * mm});
            skArc(sketch, "E15.21.5", {"start": v(-75.77, -19.81) * mm, "mid": v(-75.53, -20.12) * mm, "end": v(-75.14, -20.17) * mm});
            skArc(sketch, "E15.21.6", {"start": v(-73.5, -19.73) * mm, "mid": v(-72.56, -19.86) * mm, "end": v(-71.62, -20.04) * mm});
            skArc(sketch, "E15.21.7", {"start": v(-72.6, -22.85) * mm, "mid": v(-71.86, -22.23) * mm, "end": v(-71.17, -21.58) * mm});
            skArc(sketch, "E15.21.8", {"start": v(-71.17, -21.58) * mm, "mid": v(-71.03, -21.34) * mm, "end": v(-71.04, -21.06) * mm});
            skLineSegment(sketch, "E15.21.9", {"start": v(-71.04, -21.06) * mm, "end": v(-71.15, -20.74) * mm});
            skLineSegment(sketch, "E15.21.10", {"start": v(-71.23, -20.4) * mm, "end": v(-71.15, -20.74) * mm});
            skArc(sketch, "E15.21.11", {"start": v(-71.23, -20.4) * mm, "mid": v(-71.37, -20.17) * mm, "end": v(-71.62, -20.04) * mm});
            skArc(sketch, "E15.22.0", {"start": v(-71.9, -29.74) * mm, "mid": v(-72.18, -30.02) * mm, "end": v(-72.18, -30.41) * mm});
            skLineSegment(sketch, "E15.22.1", {"start": v(-70.5, -29.2) * mm, "end": v(-71.9, -29.74) * mm});
            skArc(sketch, "E15.22.2", {"start": v(-70.5, -29.2) * mm, "mid": v(-70.4, -29.15) * mm, "end": v(-70.33, -29.09) * mm});
            skArc(sketch, "E15.22.3", {"start": v(-71.5, -26.06) * mm, "mid": v(-71.6, -26.07) * mm, "end": v(-71.7, -26.1) * mm});
            skLineSegment(sketch, "E15.22.4", {"start": v(-71.7, -26.1) * mm, "end": v(-73.1, -26.64) * mm});
            skArc(sketch, "E15.22.5", {"start": v(-73.76, -26.34) * mm, "mid": v(-73.5, -26.63) * mm, "end": v(-73.1, -26.64) * mm});
            skArc(sketch, "E15.22.6", {"start": v(-71.5, -26.06) * mm, "mid": v(-70.55, -26.11) * mm, "end": v(-69.6, -26.2) * mm});
            skArc(sketch, "E15.22.7", {"start": v(-70.33, -29.09) * mm, "mid": v(-69.65, -28.41) * mm, "end": v(-69.02, -27.7) * mm});
            skArc(sketch, "E15.22.8", {"start": v(-69.02, -27.7) * mm, "mid": v(-68.9, -27.45) * mm, "end": v(-68.94, -27.17) * mm});
            skLineSegment(sketch, "E15.22.9", {"start": v(-68.94, -27.17) * mm, "end": v(-69.07, -26.86) * mm});
            skLineSegment(sketch, "E15.22.10", {"start": v(-69.18, -26.54) * mm, "end": v(-69.07, -26.86) * mm});
            skArc(sketch, "E15.22.11", {"start": v(-69.18, -26.54) * mm, "mid": v(-69.34, -26.31) * mm, "end": v(-69.6, -26.2) * mm});
            skArc(sketch, "E15.23.0", {"start": v(-69.03, -35.9) * mm, "mid": v(-69.28, -36.2) * mm, "end": v(-69.25, -36.59) * mm});
            skLineSegment(sketch, "E15.23.1", {"start": v(-67.68, -35.23) * mm, "end": v(-69.03, -35.9) * mm});
            skArc(sketch, "E15.23.2", {"start": v(-67.68, -35.23) * mm, "mid": v(-67.6, -35.18) * mm, "end": v(-67.52, -35.1) * mm});
            skArc(sketch, "E15.23.3", {"start": v(-68.96, -32.2) * mm, "mid": v(-69.06, -32.21) * mm, "end": v(-69.15, -32.25) * mm});
            skLineSegment(sketch, "E15.23.4", {"start": v(-69.15, -32.25) * mm, "end": v(-70.5, -32.91) * mm});
            skArc(sketch, "E15.23.5", {"start": v(-71.18, -32.67) * mm, "mid": v(-70.9, -32.93) * mm, "end": v(-70.5, -32.91) * mm});
            skArc(sketch, "E15.23.6", {"start": v(-68.96, -32.2) * mm, "mid": v(-68, -32.16) * mm, "end": v(-67.05, -32.17) * mm});
            skArc(sketch, "E15.23.7", {"start": v(-67.52, -35.1) * mm, "mid": v(-66.91, -34.37) * mm, "end": v(-66.34, -33.6) * mm});
            skArc(sketch, "E15.23.8", {"start": v(-66.34, -33.6) * mm, "mid": v(-66.25, -33.35) * mm, "end": v(-66.3, -33.08) * mm});
            skLineSegment(sketch, "E15.23.9", {"start": v(-66.3, -33.08) * mm, "end": v(-66.46, -32.78) * mm});
            skLineSegment(sketch, "E15.23.10", {"start": v(-66.6, -32.47) * mm, "end": v(-66.46, -32.78) * mm});
            skArc(sketch, "E15.23.11", {"start": v(-66.6, -32.47) * mm, "mid": v(-66.79, -32.26) * mm, "end": v(-67.05, -32.17) * mm});
            skArc(sketch, "E15.24.0", {"start": v(-65.63, -41.77) * mm, "mid": v(-65.87, -42.1) * mm, "end": v(-65.8, -42.48) * mm});
            skLineSegment(sketch, "E15.24.1", {"start": v(-64.35, -41) * mm, "end": v(-65.63, -41.77) * mm});
            skArc(sketch, "E15.24.2", {"start": v(-64.35, -41) * mm, "mid": v(-64.27, -40.93) * mm, "end": v(-64.2, -40.86) * mm});
            skArc(sketch, "E15.24.3", {"start": v(-65.9, -38.08) * mm, "mid": v(-65.99, -38.1) * mm, "end": v(-66.08, -38.15) * mm});
            skLineSegment(sketch, "E15.24.4", {"start": v(-66.08, -38.15) * mm, "end": v(-67.36, -38.93) * mm});
            skArc(sketch, "E15.24.5", {"start": v(-68.06, -38.75) * mm, "mid": v(-67.75, -38.99) * mm, "end": v(-67.36, -38.93) * mm});
            skArc(sketch, "E15.24.6", {"start": v(-65.9, -38.08) * mm, "mid": v(-64.94, -37.96) * mm, "end": v(-64, -37.9) * mm});
            skArc(sketch, "E15.24.7", {"start": v(-64.2, -40.86) * mm, "mid": v(-63.66, -40.07) * mm, "end": v(-63.16, -39.26) * mm});
            skArc(sketch, "E15.24.8", {"start": v(-63.16, -39.26) * mm, "mid": v(-63.09, -39) * mm, "end": v(-63.17, -38.73) * mm});
            skLineSegment(sketch, "E15.24.9", {"start": v(-63.17, -38.73) * mm, "end": v(-63.35, -38.44) * mm});
            skLineSegment(sketch, "E15.24.10", {"start": v(-63.52, -38.15) * mm, "end": v(-63.35, -38.44) * mm});
            skArc(sketch, "E15.24.11", {"start": v(-63.52, -38.15) * mm, "mid": v(-63.72, -37.95) * mm, "end": v(-64, -37.9) * mm});
            skArc(sketch, "E15.25.0", {"start": v(-61.74, -47.33) * mm, "mid": v(-61.95, -47.67) * mm, "end": v(-61.85, -48.06) * mm});
            skLineSegment(sketch, "E15.25.1", {"start": v(-60.53, -46.45) * mm, "end": v(-61.74, -47.33) * mm});
            skArc(sketch, "E15.25.2", {"start": v(-60.53, -46.45) * mm, "mid": v(-60.46, -46.38) * mm, "end": v(-60.4, -46.3) * mm});
            skArc(sketch, "E15.25.3", {"start": v(-62.32, -43.68) * mm, "mid": v(-62.41, -43.72) * mm, "end": v(-62.5, -43.77) * mm});
            skLineSegment(sketch, "E15.25.4", {"start": v(-62.5, -43.77) * mm, "end": v(-63.71, -44.65) * mm});
            skArc(sketch, "E15.25.5", {"start": v(-64.43, -44.53) * mm, "mid": v(-64.1, -44.74) * mm, "end": v(-63.71, -44.65) * mm});
            skArc(sketch, "E15.25.6", {"start": v(-62.32, -43.68) * mm, "mid": v(-61.39, -43.48) * mm, "end": v(-60.44, -43.32) * mm});
            skArc(sketch, "E15.25.7", {"start": v(-60.4, -46.3) * mm, "mid": v(-59.93, -45.47) * mm, "end": v(-59.5, -44.62) * mm});
            skArc(sketch, "E15.25.8", {"start": v(-59.5, -44.62) * mm, "mid": v(-59.45, -44.35) * mm, "end": v(-59.55, -44.09) * mm});
            skLineSegment(sketch, "E15.25.9", {"start": v(-59.55, -44.09) * mm, "end": v(-59.76, -43.82) * mm});
            skLineSegment(sketch, "E15.25.10", {"start": v(-59.96, -43.54) * mm, "end": v(-59.76, -43.82) * mm});
            skArc(sketch, "E15.25.11", {"start": v(-59.96, -43.54) * mm, "mid": v(-60.17, -43.36) * mm, "end": v(-60.44, -43.32) * mm});
            skArc(sketch, "E15.26.0", {"start": v(-57.38, -52.54) * mm, "mid": v(-57.56, -52.9) * mm, "end": v(-57.42, -53.26) * mm});
            skLineSegment(sketch, "E15.26.1", {"start": v(-56.26, -51.55) * mm, "end": v(-57.38, -52.54) * mm});
            skArc(sketch, "E15.26.2", {"start": v(-56.26, -51.55) * mm, "mid": v(-56.19, -51.47) * mm, "end": v(-56.14, -51.39) * mm});
            skArc(sketch, "E15.26.3", {"start": v(-58.28, -48.95) * mm, "mid": v(-58.37, -48.99) * mm, "end": v(-58.45, -49.05) * mm});
            skLineSegment(sketch, "E15.26.4", {"start": v(-58.45, -49.05) * mm, "end": v(-59.58, -50.04) * mm});
            skArc(sketch, "E15.26.5", {"start": v(-60.3, -49.98) * mm, "mid": v(-59.95, -50.16) * mm, "end": v(-59.58, -50.04) * mm});
            skArc(sketch, "E15.26.6", {"start": v(-58.28, -48.95) * mm, "mid": v(-57.36, -48.66) * mm, "end": v(-56.44, -48.43) * mm});
            skArc(sketch, "E15.26.7", {"start": v(-56.14, -51.39) * mm, "mid": v(-55.74, -50.52) * mm, "end": v(-55.38, -49.63) * mm});
            skArc(sketch, "E15.26.8", {"start": v(-55.38, -49.63) * mm, "mid": v(-55.36, -49.36) * mm, "end": v(-55.48, -49.11) * mm});
            skLineSegment(sketch, "E15.26.9", {"start": v(-55.48, -49.11) * mm, "end": v(-55.72, -48.86) * mm});
            skLineSegment(sketch, "E15.26.10", {"start": v(-55.93, -48.6) * mm, "end": v(-55.72, -48.86) * mm});
            skArc(sketch, "E15.26.11", {"start": v(-55.93, -48.6) * mm, "mid": v(-56.16, -48.44) * mm, "end": v(-56.44, -48.43) * mm});
            skArc(sketch, "E15.27.0", {"start": v(-52.59, -57.34) * mm, "mid": v(-52.73, -57.7) * mm, "end": v(-52.56, -58.06) * mm});
            skLineSegment(sketch, "E15.27.1", {"start": v(-51.55, -56.25) * mm, "end": v(-52.59, -57.34) * mm});
            skArc(sketch, "E15.27.2", {"start": v(-51.55, -56.25) * mm, "mid": v(-51.49, -56.17) * mm, "end": v(-51.44, -56.09) * mm});
            skArc(sketch, "E15.27.3", {"start": v(-53.79, -53.84) * mm, "mid": v(-53.88, -53.89) * mm, "end": v(-53.95, -53.95) * mm});
            skLineSegment(sketch, "E15.27.4", {"start": v(-53.95, -53.95) * mm, "end": v(-54.99, -55.04) * mm});
            skArc(sketch, "E15.27.5", {"start": v(-55.72, -55.04) * mm, "mid": v(-55.35, -55.2) * mm, "end": v(-54.99, -55.04) * mm});
            skArc(sketch, "E15.27.6", {"start": v(-53.79, -53.84) * mm, "mid": v(-52.9, -53.48) * mm, "end": v(-52, -53.16) * mm});
            skArc(sketch, "E15.27.7", {"start": v(-51.44, -56.09) * mm, "mid": v(-51.12, -55.19) * mm, "end": v(-50.84, -54.27) * mm});
            skArc(sketch, "E15.27.8", {"start": v(-50.84, -54.27) * mm, "mid": v(-50.85, -54) * mm, "end": v(-51, -53.76) * mm});
            skLineSegment(sketch, "E15.27.9", {"start": v(-51, -53.76) * mm, "end": v(-51.25, -53.53) * mm});
            skLineSegment(sketch, "E15.27.10", {"start": v(-51.49, -53.29) * mm, "end": v(-51.25, -53.53) * mm});
            skArc(sketch, "E15.27.11", {"start": v(-51.49, -53.29) * mm, "mid": v(-51.73, -53.15) * mm, "end": v(-52, -53.16) * mm});
            skArc(sketch, "E15.28.0", {"start": v(-47.39, -61.7) * mm, "mid": v(-47.5, -62.08) * mm, "end": v(-47.3, -62.42) * mm});
            skLineSegment(sketch, "E15.28.1", {"start": v(-46.45, -60.53) * mm, "end": v(-47.39, -61.7) * mm});
            skArc(sketch, "E15.28.2", {"start": v(-46.45, -60.53) * mm, "mid": v(-46.4, -60.45) * mm, "end": v(-46.36, -60.36) * mm});
            skArc(sketch, "E15.28.3", {"start": v(-48.9, -58.32) * mm, "mid": v(-48.97, -58.38) * mm, "end": v(-49.04, -58.45) * mm});
            skLineSegment(sketch, "E15.28.4", {"start": v(-49.04, -58.45) * mm, "end": v(-49.98, -59.62) * mm});
            skArc(sketch, "E15.28.5", {"start": v(-50.7, -59.7) * mm, "mid": v(-50.33, -59.8) * mm, "end": v(-49.98, -59.62) * mm});
            skArc(sketch, "E15.28.6", {"start": v(-48.9, -58.32) * mm, "mid": v(-48.04, -57.89) * mm, "end": v(-47.17, -57.5) * mm});
            skArc(sketch, "E15.28.7", {"start": v(-46.36, -60.36) * mm, "mid": v(-46.12, -59.43) * mm, "end": v(-45.92, -58.5) * mm});
            skArc(sketch, "E15.28.8", {"start": v(-45.92, -58.5) * mm, "mid": v(-45.95, -58.22) * mm, "end": v(-46.11, -58) * mm});
            skLineSegment(sketch, "E15.28.9", {"start": v(-46.11, -58) * mm, "end": v(-46.38, -57.8) * mm});
            skLineSegment(sketch, "E15.28.10", {"start": v(-46.65, -57.57) * mm, "end": v(-46.38, -57.8) * mm});
            skArc(sketch, "E15.28.11", {"start": v(-46.65, -57.57) * mm, "mid": v(-46.9, -57.46) * mm, "end": v(-47.17, -57.5) * mm});
            skArc(sketch, "E15.29.0", {"start": v(-41.83, -65.6) * mm, "mid": v(-41.9, -65.99) * mm, "end": v(-41.68, -66.3) * mm});
            skLineSegment(sketch, "E15.29.1", {"start": v(-41, -64.35) * mm, "end": v(-41.83, -65.6) * mm});
            skArc(sketch, "E15.29.2", {"start": v(-41, -64.35) * mm, "mid": v(-40.95, -64.26) * mm, "end": v(-40.92, -64.17) * mm});
            skArc(sketch, "E15.29.3", {"start": v(-43.62, -62.36) * mm, "mid": v(-43.7, -62.43) * mm, "end": v(-43.76, -62.5) * mm});
            skLineSegment(sketch, "E15.29.4", {"start": v(-43.76, -62.5) * mm, "end": v(-44.6, -63.75) * mm});
            skArc(sketch, "E15.29.5", {"start": v(-45.31, -63.88) * mm, "mid": v(-44.93, -63.97) * mm, "end": v(-44.6, -63.75) * mm});
            skArc(sketch, "E15.29.6", {"start": v(-43.62, -62.36) * mm, "mid": v(-42.81, -61.85) * mm, "end": v(-41.98, -61.39) * mm});
            skArc(sketch, "E15.29.7", {"start": v(-40.92, -64.17) * mm, "mid": v(-40.76, -63.22) * mm, "end": v(-40.65, -62.28) * mm});
            skArc(sketch, "E15.29.8", {"start": v(-40.65, -62.28) * mm, "mid": v(-40.7, -62) * mm, "end": v(-40.88, -61.8) * mm});
            skLineSegment(sketch, "E15.29.9", {"start": v(-40.88, -61.8) * mm, "end": v(-41.17, -61.62) * mm});
            skLineSegment(sketch, "E15.29.10", {"start": v(-41.45, -61.42) * mm, "end": v(-41.17, -61.62) * mm});
            skArc(sketch, "E15.29.11", {"start": v(-41.45, -61.42) * mm, "mid": v(-41.71, -61.33) * mm, "end": v(-41.98, -61.39) * mm});
            skArc(sketch, "E15.30.0", {"start": v(-35.96, -69) * mm, "mid": v(-36, -69.39) * mm, "end": v(-35.74, -69.7) * mm});
            skLineSegment(sketch, "E15.30.1", {"start": v(-35.23, -67.68) * mm, "end": v(-35.96, -69) * mm});
            skArc(sketch, "E15.30.2", {"start": v(-35.23, -67.68) * mm, "mid": v(-35.2, -67.59) * mm, "end": v(-35.17, -67.49) * mm});
            skArc(sketch, "E15.30.3", {"start": v(-38.02, -65.93) * mm, "mid": v(-38.1, -66) * mm, "end": v(-38.15, -66.08) * mm});
            skLineSegment(sketch, "E15.30.4", {"start": v(-38.15, -66.08) * mm, "end": v(-38.87, -67.4) * mm});
            skArc(sketch, "E15.30.5", {"start": v(-39.57, -67.59) * mm, "mid": v(-39.18, -67.64) * mm, "end": v(-38.87, -67.4) * mm});
            skArc(sketch, "E15.30.6", {"start": v(-38.02, -65.93) * mm, "mid": v(-37.26, -65.35) * mm, "end": v(-36.47, -64.81) * mm});
            skArc(sketch, "E15.30.7", {"start": v(-35.17, -67.49) * mm, "mid": v(-35.1, -66.54) * mm, "end": v(-35.06, -65.58) * mm});
            skArc(sketch, "E15.30.8", {"start": v(-35.06, -65.58) * mm, "mid": v(-35.14, -65.32) * mm, "end": v(-35.34, -65.13) * mm});
            skLineSegment(sketch, "E15.30.9", {"start": v(-35.34, -65.13) * mm, "end": v(-35.64, -64.97) * mm});
            skLineSegment(sketch, "E15.30.10", {"start": v(-35.94, -64.8) * mm, "end": v(-35.64, -64.97) * mm});
            skArc(sketch, "E15.30.11", {"start": v(-35.94, -64.8) * mm, "mid": v(-36.2, -64.73) * mm, "end": v(-36.47, -64.81) * mm});
            skArc(sketch, "E15.31.0", {"start": v(-29.8, -71.86) * mm, "mid": v(-29.81, -72.26) * mm, "end": v(-29.53, -72.54) * mm});
            skLineSegment(sketch, "E15.31.1", {"start": v(-29.2, -70.5) * mm, "end": v(-29.8, -71.86) * mm});
            skArc(sketch, "E15.31.2", {"start": v(-29.2, -70.5) * mm, "mid": v(-29.17, -70.4) * mm, "end": v(-29.16, -70.3) * mm});
            skArc(sketch, "E15.31.3", {"start": v(-32.13, -68.99) * mm, "mid": v(-32.2, -69.07) * mm, "end": v(-32.24, -69.15) * mm});
            skLineSegment(sketch, "E15.31.4", {"start": v(-32.24, -69.15) * mm, "end": v(-32.85, -70.53) * mm});
            skArc(sketch, "E15.31.5", {"start": v(-33.53, -70.78) * mm, "mid": v(-33.14, -70.8) * mm, "end": v(-32.85, -70.53) * mm});
            skArc(sketch, "E15.31.6", {"start": v(-32.13, -68.99) * mm, "mid": v(-31.42, -68.35) * mm, "end": v(-30.68, -67.74) * mm});
            skArc(sketch, "E15.31.7", {"start": v(-29.16, -70.3) * mm, "mid": v(-29.16, -69.34) * mm, "end": v(-29.22, -68.39) * mm});
            skArc(sketch, "E15.31.8", {"start": v(-29.22, -68.39) * mm, "mid": v(-29.31, -68.13) * mm, "end": v(-29.53, -67.96) * mm});
            skLineSegment(sketch, "E15.31.9", {"start": v(-29.53, -67.96) * mm, "end": v(-29.85, -67.83) * mm});
            skLineSegment(sketch, "E15.31.10", {"start": v(-30.15, -67.68) * mm, "end": v(-29.85, -67.83) * mm});
            skArc(sketch, "E15.31.11", {"start": v(-30.15, -67.68) * mm, "mid": v(-30.43, -67.64) * mm, "end": v(-30.68, -67.74) * mm});
            skArc(sketch, "E15.32.0", {"start": v(-23.43, -74.19) * mm, "mid": v(-23.4, -74.58) * mm, "end": v(-23.1, -74.84) * mm});
            skLineSegment(sketch, "E15.32.1", {"start": v(-22.95, -72.77) * mm, "end": v(-23.43, -74.19) * mm});
            skArc(sketch, "E15.32.2", {"start": v(-22.95, -72.77) * mm, "mid": v(-22.92, -72.67) * mm, "end": v(-22.92, -72.57) * mm});
            skArc(sketch, "E15.32.3", {"start": v(-26, -71.53) * mm, "mid": v(-26.05, -71.6) * mm, "end": v(-26.1, -71.7) * mm});
            skLineSegment(sketch, "E15.32.4", {"start": v(-26.1, -71.7) * mm, "end": v(-26.58, -73.12) * mm});
            skArc(sketch, "E15.32.5", {"start": v(-27.23, -73.43) * mm, "mid": v(-26.84, -73.42) * mm, "end": v(-26.58, -73.12) * mm});
            skArc(sketch, "E15.32.6", {"start": v(-26, -71.53) * mm, "mid": v(-25.35, -70.83) * mm, "end": v(-24.66, -70.16) * mm});
            skArc(sketch, "E15.32.7", {"start": v(-22.92, -72.57) * mm, "mid": v(-23, -71.62) * mm, "end": v(-23.14, -70.67) * mm});
            skArc(sketch, "E15.32.8", {"start": v(-23.14, -70.67) * mm, "mid": v(-23.26, -70.42) * mm, "end": v(-23.5, -70.27) * mm});
            skLineSegment(sketch, "E15.32.9", {"start": v(-23.5, -70.27) * mm, "end": v(-23.82, -70.17) * mm});
            skLineSegment(sketch, "E15.32.10", {"start": v(-24.14, -70.05) * mm, "end": v(-23.82, -70.17) * mm});
            skArc(sketch, "E15.32.11", {"start": v(-24.14, -70.05) * mm, "mid": v(-24.42, -70.03) * mm, "end": v(-24.66, -70.16) * mm});
            skArc(sketch, "E15.33.0", {"start": v(-16.87, -75.95) * mm, "mid": v(-16.81, -76.34) * mm, "end": v(-16.49, -76.57) * mm});
            skLineSegment(sketch, "E15.33.1", {"start": v(-16.52, -74.5) * mm, "end": v(-16.87, -75.95) * mm});
            skArc(sketch, "E15.33.2", {"start": v(-16.52, -74.5) * mm, "mid": v(-16.5, -74.4) * mm, "end": v(-16.5, -74.3) * mm});
            skArc(sketch, "E15.33.3", {"start": v(-19.66, -73.52) * mm, "mid": v(-19.71, -73.6) * mm, "end": v(-19.75, -73.7) * mm});
            skLineSegment(sketch, "E15.33.4", {"start": v(-19.75, -73.7) * mm, "end": v(-20.1, -75.16) * mm});
            skArc(sketch, "E15.33.5", {"start": v(-20.73, -75.53) * mm, "mid": v(-20.34, -75.48) * mm, "end": v(-20.1, -75.16) * mm});
            skArc(sketch, "E15.33.6", {"start": v(-19.66, -73.52) * mm, "mid": v(-19.08, -72.77) * mm, "end": v(-18.45, -72.04) * mm});
            skArc(sketch, "E15.33.7", {"start": v(-16.5, -74.3) * mm, "mid": v(-16.68, -73.35) * mm, "end": v(-16.9, -72.42) * mm});
            skArc(sketch, "E15.33.8", {"start": v(-16.9, -72.42) * mm, "mid": v(-17.04, -72.18) * mm, "end": v(-17.28, -72.05) * mm});
            skLineSegment(sketch, "E15.33.9", {"start": v(-17.28, -72.05) * mm, "end": v(-17.61, -71.98) * mm});
            skLineSegment(sketch, "E15.33.10", {"start": v(-17.94, -71.9) * mm, "end": v(-17.61, -71.98) * mm});
            skArc(sketch, "E15.33.11", {"start": v(-17.94, -71.9) * mm, "mid": v(-18.22, -71.9) * mm, "end": v(-18.45, -72.04) * mm});
            skArc(sketch, "E15.34.0", {"start": v(-10.19, -77.13) * mm, "mid": v(-10.1, -77.51) * mm, "end": v(-9.75, -77.71) * mm});
            skLineSegment(sketch, "E15.34.1", {"start": v(-9.96, -75.65) * mm, "end": v(-10.19, -77.13) * mm});
            skArc(sketch, "E15.34.2", {"start": v(-9.96, -75.65) * mm, "mid": v(-9.96, -75.55) * mm, "end": v(-9.97, -75.45) * mm});
            skArc(sketch, "E15.34.3", {"start": v(-13.18, -74.95) * mm, "mid": v(-13.22, -75.05) * mm, "end": v(-13.25, -75.14) * mm});
            skLineSegment(sketch, "E15.34.4", {"start": v(-13.25, -75.14) * mm, "end": v(-13.48, -76.62) * mm});
            skArc(sketch, "E15.34.5", {"start": v(-14.07, -77.05) * mm, "mid": v(-13.68, -76.96) * mm, "end": v(-13.48, -76.62) * mm});
            skArc(sketch, "E15.34.6", {"start": v(-13.18, -74.95) * mm, "mid": v(-12.66, -74.15) * mm, "end": v(-12.1, -73.38) * mm});
            skArc(sketch, "E15.34.7", {"start": v(-9.97, -75.45) * mm, "mid": v(-10.22, -74.53) * mm, "end": v(-10.52, -73.62) * mm});
            skArc(sketch, "E15.34.8", {"start": v(-10.52, -73.62) * mm, "mid": v(-10.68, -73.4) * mm, "end": v(-10.93, -73.29) * mm});
            skLineSegment(sketch, "E15.34.9", {"start": v(-10.93, -73.29) * mm, "end": v(-11.27, -73.24) * mm});
            skLineSegment(sketch, "E15.34.10", {"start": v(-11.6, -73.18) * mm, "end": v(-11.27, -73.24) * mm});
            skArc(sketch, "E15.34.11", {"start": v(-11.6, -73.18) * mm, "mid": v(-11.88, -73.2) * mm, "end": v(-12.1, -73.38) * mm});
            skArc(sketch, "E15.35.0", {"start": v(-3.43, -77.72) * mm, "mid": v(-3.3, -78.1) * mm, "end": v(-2.94, -78.27) * mm});
            skLineSegment(sketch, "E15.35.1", {"start": v(-3.33, -76.23) * mm, "end": v(-3.43, -77.72) * mm});
            skArc(sketch, "E15.35.2", {"start": v(-3.33, -76.23) * mm, "mid": v(-3.33, -76.13) * mm, "end": v(-3.36, -76.03) * mm});
            skArc(sketch, "E15.35.3", {"start": v(-6.6, -75.82) * mm, "mid": v(-6.63, -75.91) * mm, "end": v(-6.65, -76.01) * mm});
            skLineSegment(sketch, "E15.35.4", {"start": v(-6.65, -76.01) * mm, "end": v(-6.75, -77.5) * mm});
            skArc(sketch, "E15.35.5", {"start": v(-7.3, -77.98) * mm, "mid": v(-6.92, -77.86) * mm, "end": v(-6.75, -77.5) * mm});
            skArc(sketch, "E15.35.6", {"start": v(-6.6, -75.82) * mm, "mid": v(-6.15, -74.97) * mm, "end": v(-5.66, -74.15) * mm});
            skArc(sketch, "E15.35.7", {"start": v(-3.36, -76.03) * mm, "mid": v(-3.69, -75.13) * mm, "end": v(-4.06, -74.26) * mm});
            skArc(sketch, "E15.35.8", {"start": v(-4.06, -74.26) * mm, "mid": v(-4.24, -74.05) * mm, "end": v(-4.5, -73.96) * mm});
            skLineSegment(sketch, "E15.35.9", {"start": v(-4.5, -73.96) * mm, "end": v(-4.85, -73.95) * mm});
            skLineSegment(sketch, "E15.35.10", {"start": v(-5.19, -73.92) * mm, "end": v(-4.85, -73.95) * mm});
            skArc(sketch, "E15.35.11", {"start": v(-5.19, -73.92) * mm, "mid": v(-5.46, -73.97) * mm, "end": v(-5.66, -74.15) * mm});
            skArc(sketch, "E15.36.0", {"start": v(3.36, -77.73) * mm, "mid": v(3.52, -78.09) * mm, "end": v(3.9, -78.22) * mm});
            skLineSegment(sketch, "E15.36.1", {"start": v(3.33, -76.23) * mm, "end": v(3.36, -77.73) * mm});
            skArc(sketch, "E15.36.2", {"start": v(3.33, -76.23) * mm, "mid": v(3.31, -76.13) * mm, "end": v(3.28, -76.03) * mm});
            skArc(sketch, "E15.36.3", {"start": v(0.04, -76.1) * mm, "mid": v(0, -76.2) * mm, "end": v(0, -76.3) * mm});
            skLineSegment(sketch, "E15.36.4", {"start": v(0, -76.3) * mm, "end": v(0.03, -77.8) * mm});
            skArc(sketch, "E15.36.5", {"start": v(-0.48, -78.32) * mm, "mid": v(-0.11, -78.17) * mm, "end": v(0.03, -77.8) * mm});
            skArc(sketch, "E15.36.6", {"start": v(0.04, -76.1) * mm, "mid": v(0.4, -75.22) * mm, "end": v(0.82, -74.36) * mm});
            skArc(sketch, "E15.36.7", {"start": v(3.28, -76.03) * mm, "mid": v(2.87, -75.17) * mm, "end": v(2.42, -74.33) * mm});
            skArc(sketch, "E15.36.8", {"start": v(2.42, -74.33) * mm, "mid": v(2.23, -74.13) * mm, "end": v(1.96, -74.07) * mm});
            skLineSegment(sketch, "E15.36.9", {"start": v(1.96, -74.07) * mm, "end": v(1.62, -74.09) * mm});
            skLineSegment(sketch, "E15.36.10", {"start": v(1.28, -74.09) * mm, "end": v(1.62, -74.09) * mm});
            skArc(sketch, "E15.36.11", {"start": v(1.28, -74.09) * mm, "mid": v(1, -74.16) * mm, "end": v(0.82, -74.36) * mm});
            skArc(sketch, "E15.37.0", {"start": v(10.12, -77.14) * mm, "mid": v(10.31, -77.48) * mm, "end": v(10.7, -77.59) * mm});
            skLineSegment(sketch, "E15.37.1", {"start": v(9.96, -75.65) * mm, "end": v(10.12, -77.14) * mm});
            skArc(sketch, "E15.37.2", {"start": v(9.96, -75.65) * mm, "mid": v(9.94, -75.55) * mm, "end": v(9.9, -75.46) * mm});
            skArc(sketch, "E15.37.3", {"start": v(6.67, -75.81) * mm, "mid": v(6.65, -75.91) * mm, "end": v(6.65, -76.01) * mm});
            skLineSegment(sketch, "E15.37.4", {"start": v(6.65, -76.01) * mm, "end": v(6.82, -77.5) * mm});
            skArc(sketch, "E15.37.5", {"start": v(6.35, -78.06) * mm, "mid": v(6.7, -77.88) * mm, "end": v(6.82, -77.5) * mm});
            skArc(sketch, "E15.37.6", {"start": v(6.67, -75.81) * mm, "mid": v(6.96, -74.9) * mm, "end": v(7.3, -74) * mm});
            skArc(sketch, "E15.37.7", {"start": v(9.9, -75.46) * mm, "mid": v(9.42, -74.63) * mm, "end": v(8.9, -73.83) * mm});
            skArc(sketch, "E15.37.8", {"start": v(8.9, -73.83) * mm, "mid": v(8.68, -73.66) * mm, "end": v(8.4, -73.62) * mm});
            skLineSegment(sketch, "E15.37.9", {"start": v(8.4, -73.62) * mm, "end": v(8.07, -73.67) * mm});
            skLineSegment(sketch, "E15.37.10", {"start": v(7.73, -73.7) * mm, "end": v(8.07, -73.67) * mm});
            skArc(sketch, "E15.37.11", {"start": v(7.73, -73.7) * mm, "mid": v(7.47, -73.8) * mm, "end": v(7.3, -74) * mm});
            skArc(sketch, "E15.38.0", {"start": v(16.8, -75.96) * mm, "mid": v(17.03, -76.3) * mm, "end": v(17.42, -76.36) * mm});
            skLineSegment(sketch, "E15.38.1", {"start": v(16.51, -74.5) * mm, "end": v(16.8, -75.96) * mm});
            skArc(sketch, "E15.38.2", {"start": v(16.51, -74.5) * mm, "mid": v(16.48, -74.4) * mm, "end": v(16.44, -74.3) * mm});
            skArc(sketch, "E15.38.3", {"start": v(13.25, -74.94) * mm, "mid": v(13.24, -75.04) * mm, "end": v(13.25, -75.14) * mm});
            skLineSegment(sketch, "E15.38.4", {"start": v(13.25, -75.14) * mm, "end": v(13.54, -76.61) * mm});
            skArc(sketch, "E15.38.5", {"start": v(13.13, -77.21) * mm, "mid": v(13.46, -77) * mm, "end": v(13.54, -76.61) * mm});
            skArc(sketch, "E15.38.6", {"start": v(13.25, -74.94) * mm, "mid": v(13.46, -74.01) * mm, "end": v(13.72, -73.1) * mm});
            skArc(sketch, "E15.38.7", {"start": v(16.44, -74.3) * mm, "mid": v(15.88, -73.53) * mm, "end": v(15.3, -72.78) * mm});
            skArc(sketch, "E15.38.8", {"start": v(15.3, -72.78) * mm, "mid": v(15.07, -72.62) * mm, "end": v(14.8, -72.6) * mm});
            skLineSegment(sketch, "E15.38.9", {"start": v(14.8, -72.6) * mm, "end": v(14.46, -72.68) * mm});
            skLineSegment(sketch, "E15.38.10", {"start": v(14.12, -72.74) * mm, "end": v(14.46, -72.68) * mm});
            skArc(sketch, "E15.38.11", {"start": v(14.12, -72.74) * mm, "mid": v(13.87, -72.86) * mm, "end": v(13.72, -73.1) * mm});
            skArc(sketch, "E15.39.0", {"start": v(23.36, -74.21) * mm, "mid": v(23.61, -74.52) * mm, "end": v(24, -74.55) * mm});
            skLineSegment(sketch, "E15.39.1", {"start": v(22.94, -72.77) * mm, "end": v(23.36, -74.21) * mm});
            skArc(sketch, "E15.39.2", {"start": v(22.94, -72.77) * mm, "mid": v(22.9, -72.68) * mm, "end": v(22.85, -72.6) * mm});
            skArc(sketch, "E15.39.3", {"start": v(19.73, -73.5) * mm, "mid": v(19.73, -73.6) * mm, "end": v(19.75, -73.7) * mm});
            skLineSegment(sketch, "E15.39.4", {"start": v(19.75, -73.7) * mm, "end": v(20.17, -75.14) * mm});
            skArc(sketch, "E15.39.5", {"start": v(19.81, -75.77) * mm, "mid": v(20.12, -75.53) * mm, "end": v(20.17, -75.14) * mm});
            skArc(sketch, "E15.39.6", {"start": v(19.73, -73.5) * mm, "mid": v(19.86, -72.56) * mm, "end": v(20.04, -71.62) * mm});
            skArc(sketch, "E15.39.7", {"start": v(22.85, -72.6) * mm, "mid": v(22.23, -71.86) * mm, "end": v(21.58, -71.17) * mm});
            skArc(sketch, "E15.39.8", {"start": v(21.58, -71.17) * mm, "mid": v(21.34, -71.03) * mm, "end": v(21.06, -71.04) * mm});
            skLineSegment(sketch, "E15.39.9", {"start": v(21.06, -71.04) * mm, "end": v(20.74, -71.15) * mm});
            skLineSegment(sketch, "E15.39.10", {"start": v(20.4, -71.23) * mm, "end": v(20.74, -71.15) * mm});
            skArc(sketch, "E15.39.11", {"start": v(20.4, -71.23) * mm, "mid": v(20.17, -71.37) * mm, "end": v(20.04, -71.62) * mm});
            skArc(sketch, "E15.40.0", {"start": v(29.74, -71.9) * mm, "mid": v(30.02, -72.18) * mm, "end": v(30.41, -72.18) * mm});
            skLineSegment(sketch, "E15.40.1", {"start": v(29.2, -70.5) * mm, "end": v(29.74, -71.9) * mm});
            skArc(sketch, "E15.40.2", {"start": v(29.2, -70.5) * mm, "mid": v(29.15, -70.4) * mm, "end": v(29.09, -70.33) * mm});
            skArc(sketch, "E15.40.3", {"start": v(26.06, -71.5) * mm, "mid": v(26.07, -71.6) * mm, "end": v(26.1, -71.7) * mm});
            skLineSegment(sketch, "E15.40.4", {"start": v(26.1, -71.7) * mm, "end": v(26.64, -73.1) * mm});
            skArc(sketch, "E15.40.5", {"start": v(26.34, -73.76) * mm, "mid": v(26.63, -73.5) * mm, "end": v(26.64, -73.1) * mm});
            skArc(sketch, "E15.40.6", {"start": v(26.06, -71.5) * mm, "mid": v(26.11, -70.55) * mm, "end": v(26.2, -69.6) * mm});
            skArc(sketch, "E15.40.7", {"start": v(29.09, -70.33) * mm, "mid": v(28.41, -69.65) * mm, "end": v(27.7, -69.02) * mm});
            skArc(sketch, "E15.40.8", {"start": v(27.7, -69.02) * mm, "mid": v(27.45, -68.9) * mm, "end": v(27.17, -68.94) * mm});
            skLineSegment(sketch, "E15.40.9", {"start": v(27.17, -68.94) * mm, "end": v(26.86, -69.07) * mm});
            skLineSegment(sketch, "E15.40.10", {"start": v(26.54, -69.18) * mm, "end": v(26.86, -69.07) * mm});
            skArc(sketch, "E15.40.11", {"start": v(26.54, -69.18) * mm, "mid": v(26.31, -69.34) * mm, "end": v(26.2, -69.6) * mm});
            skArc(sketch, "E15.41.0", {"start": v(35.9, -69.03) * mm, "mid": v(36.2, -69.28) * mm, "end": v(36.59, -69.25) * mm});
            skLineSegment(sketch, "E15.41.1", {"start": v(35.23, -67.68) * mm, "end": v(35.9, -69.03) * mm});
            skArc(sketch, "E15.41.2", {"start": v(35.23, -67.68) * mm, "mid": v(35.18, -67.6) * mm, "end": v(35.1, -67.52) * mm});
            skArc(sketch, "E15.41.3", {"start": v(32.2, -68.96) * mm, "mid": v(32.21, -69.06) * mm, "end": v(32.25, -69.15) * mm});
            skLineSegment(sketch, "E15.41.4", {"start": v(32.25, -69.15) * mm, "end": v(32.91, -70.5) * mm});
            skArc(sketch, "E15.41.5", {"start": v(32.67, -71.18) * mm, "mid": v(32.93, -70.9) * mm, "end": v(32.91, -70.5) * mm});
            skArc(sketch, "E15.41.6", {"start": v(32.2, -68.96) * mm, "mid": v(32.16, -68) * mm, "end": v(32.17, -67.05) * mm});
            skArc(sketch, "E15.41.7", {"start": v(35.1, -67.52) * mm, "mid": v(34.37, -66.91) * mm, "end": v(33.6, -66.34) * mm});
            skArc(sketch, "E15.41.8", {"start": v(33.6, -66.34) * mm, "mid": v(33.35, -66.25) * mm, "end": v(33.08, -66.3) * mm});
            skLineSegment(sketch, "E15.41.9", {"start": v(33.08, -66.3) * mm, "end": v(32.78, -66.46) * mm});
            skLineSegment(sketch, "E15.41.10", {"start": v(32.47, -66.6) * mm, "end": v(32.78, -66.46) * mm});
            skArc(sketch, "E15.41.11", {"start": v(32.47, -66.6) * mm, "mid": v(32.26, -66.79) * mm, "end": v(32.17, -67.05) * mm});
            skArc(sketch, "E15.42.0", {"start": v(41.77, -65.63) * mm, "mid": v(42.1, -65.87) * mm, "end": v(42.48, -65.8) * mm});
            skLineSegment(sketch, "E15.42.1", {"start": v(41, -64.35) * mm, "end": v(41.77, -65.63) * mm});
            skArc(sketch, "E15.42.2", {"start": v(41, -64.35) * mm, "mid": v(40.93, -64.27) * mm, "end": v(40.86, -64.2) * mm});
            skArc(sketch, "E15.42.3", {"start": v(38.08, -65.9) * mm, "mid": v(38.1, -65.99) * mm, "end": v(38.15, -66.08) * mm});
            skLineSegment(sketch, "E15.42.4", {"start": v(38.15, -66.08) * mm, "end": v(38.93, -67.36) * mm});
            skArc(sketch, "E15.42.5", {"start": v(38.75, -68.06) * mm, "mid": v(38.99, -67.75) * mm, "end": v(38.93, -67.36) * mm});
            skArc(sketch, "E15.42.6", {"start": v(38.08, -65.9) * mm, "mid": v(37.96, -64.94) * mm, "end": v(37.9, -64) * mm});
            skArc(sketch, "E15.42.7", {"start": v(40.86, -64.2) * mm, "mid": v(40.07, -63.66) * mm, "end": v(39.26, -63.16) * mm});
            skArc(sketch, "E15.42.8", {"start": v(39.26, -63.16) * mm, "mid": v(39, -63.09) * mm, "end": v(38.73, -63.17) * mm});
            skLineSegment(sketch, "E15.42.9", {"start": v(38.73, -63.17) * mm, "end": v(38.44, -63.35) * mm});
            skLineSegment(sketch, "E15.42.10", {"start": v(38.15, -63.52) * mm, "end": v(38.44, -63.35) * mm});
            skArc(sketch, "E15.42.11", {"start": v(38.15, -63.52) * mm, "mid": v(37.95, -63.72) * mm, "end": v(37.9, -64) * mm});
            skArc(sketch, "E15.43.0", {"start": v(47.33, -61.74) * mm, "mid": v(47.67, -61.95) * mm, "end": v(48.06, -61.85) * mm});
            skLineSegment(sketch, "E15.43.1", {"start": v(46.45, -60.53) * mm, "end": v(47.33, -61.74) * mm});
            skArc(sketch, "E15.43.2", {"start": v(46.45, -60.53) * mm, "mid": v(46.38, -60.46) * mm, "end": v(46.3, -60.4) * mm});
            skArc(sketch, "E15.43.3", {"start": v(43.68, -62.32) * mm, "mid": v(43.72, -62.41) * mm, "end": v(43.77, -62.5) * mm});
            skLineSegment(sketch, "E15.43.4", {"start": v(43.77, -62.5) * mm, "end": v(44.65, -63.71) * mm});
            skArc(sketch, "E15.43.5", {"start": v(44.53, -64.43) * mm, "mid": v(44.74, -64.1) * mm, "end": v(44.65, -63.71) * mm});
            skArc(sketch, "E15.43.6", {"start": v(43.68, -62.32) * mm, "mid": v(43.48, -61.39) * mm, "end": v(43.32, -60.44) * mm});
            skArc(sketch, "E15.43.7", {"start": v(46.3, -60.4) * mm, "mid": v(45.47, -59.93) * mm, "end": v(44.62, -59.5) * mm});
            skArc(sketch, "E15.43.8", {"start": v(44.62, -59.5) * mm, "mid": v(44.35, -59.45) * mm, "end": v(44.09, -59.55) * mm});
            skLineSegment(sketch, "E15.43.9", {"start": v(44.09, -59.55) * mm, "end": v(43.82, -59.76) * mm});
            skLineSegment(sketch, "E15.43.10", {"start": v(43.54, -59.96) * mm, "end": v(43.82, -59.76) * mm});
            skArc(sketch, "E15.43.11", {"start": v(43.54, -59.96) * mm, "mid": v(43.36, -60.17) * mm, "end": v(43.32, -60.44) * mm});
            skArc(sketch, "E15.44.0", {"start": v(52.54, -57.38) * mm, "mid": v(52.9, -57.56) * mm, "end": v(53.26, -57.42) * mm});
            skLineSegment(sketch, "E15.44.1", {"start": v(51.55, -56.26) * mm, "end": v(52.54, -57.38) * mm});
            skArc(sketch, "E15.44.2", {"start": v(51.55, -56.26) * mm, "mid": v(51.47, -56.19) * mm, "end": v(51.39, -56.14) * mm});
            skArc(sketch, "E15.44.3", {"start": v(48.95, -58.28) * mm, "mid": v(48.99, -58.37) * mm, "end": v(49.05, -58.45) * mm});
            skLineSegment(sketch, "E15.44.4", {"start": v(49.05, -58.45) * mm, "end": v(50.04, -59.58) * mm});
            skArc(sketch, "E15.44.5", {"start": v(49.98, -60.3) * mm, "mid": v(50.16, -59.95) * mm, "end": v(50.04, -59.58) * mm});
            skArc(sketch, "E15.44.6", {"start": v(48.95, -58.28) * mm, "mid": v(48.66, -57.36) * mm, "end": v(48.43, -56.44) * mm});
            skArc(sketch, "E15.44.7", {"start": v(51.39, -56.14) * mm, "mid": v(50.52, -55.74) * mm, "end": v(49.63, -55.38) * mm});
            skArc(sketch, "E15.44.8", {"start": v(49.63, -55.38) * mm, "mid": v(49.36, -55.36) * mm, "end": v(49.11, -55.48) * mm});
            skLineSegment(sketch, "E15.44.9", {"start": v(49.11, -55.48) * mm, "end": v(48.86, -55.72) * mm});
            skLineSegment(sketch, "E15.44.10", {"start": v(48.6, -55.93) * mm, "end": v(48.86, -55.72) * mm});
            skArc(sketch, "E15.44.11", {"start": v(48.6, -55.93) * mm, "mid": v(48.44, -56.16) * mm, "end": v(48.43, -56.44) * mm});
            skArc(sketch, "E15.45.0", {"start": v(57.34, -52.59) * mm, "mid": v(57.7, -52.73) * mm, "end": v(58.06, -52.56) * mm});
            skLineSegment(sketch, "E15.45.1", {"start": v(56.25, -51.55) * mm, "end": v(57.34, -52.59) * mm});
            skArc(sketch, "E15.45.2", {"start": v(56.25, -51.55) * mm, "mid": v(56.17, -51.49) * mm, "end": v(56.09, -51.44) * mm});
            skArc(sketch, "E15.45.3", {"start": v(53.84, -53.79) * mm, "mid": v(53.89, -53.88) * mm, "end": v(53.95, -53.95) * mm});
            skLineSegment(sketch, "E15.45.4", {"start": v(53.95, -53.95) * mm, "end": v(55.04, -54.99) * mm});
            skArc(sketch, "E15.45.5", {"start": v(55.04, -55.72) * mm, "mid": v(55.2, -55.35) * mm, "end": v(55.04, -54.99) * mm});
            skArc(sketch, "E15.45.6", {"start": v(53.84, -53.79) * mm, "mid": v(53.48, -52.9) * mm, "end": v(53.16, -52) * mm});
            skArc(sketch, "E15.45.7", {"start": v(56.09, -51.44) * mm, "mid": v(55.19, -51.12) * mm, "end": v(54.27, -50.84) * mm});
            skArc(sketch, "E15.45.8", {"start": v(54.27, -50.84) * mm, "mid": v(54, -50.85) * mm, "end": v(53.76, -51) * mm});
            skLineSegment(sketch, "E15.45.9", {"start": v(53.76, -51) * mm, "end": v(53.53, -51.25) * mm});
            skLineSegment(sketch, "E15.45.10", {"start": v(53.29, -51.49) * mm, "end": v(53.53, -51.25) * mm});
            skArc(sketch, "E15.45.11", {"start": v(53.29, -51.49) * mm, "mid": v(53.15, -51.73) * mm, "end": v(53.16, -52) * mm});
            skArc(sketch, "E15.46.0", {"start": v(61.7, -47.39) * mm, "mid": v(62.08, -47.5) * mm, "end": v(62.42, -47.3) * mm});
            skLineSegment(sketch, "E15.46.1", {"start": v(60.53, -46.45) * mm, "end": v(61.7, -47.39) * mm});
            skArc(sketch, "E15.46.2", {"start": v(60.53, -46.45) * mm, "mid": v(60.45, -46.4) * mm, "end": v(60.36, -46.36) * mm});
            skArc(sketch, "E15.46.3", {"start": v(58.32, -48.9) * mm, "mid": v(58.38, -48.97) * mm, "end": v(58.45, -49.04) * mm});
            skLineSegment(sketch, "E15.46.4", {"start": v(58.45, -49.04) * mm, "end": v(59.62, -49.98) * mm});
            skArc(sketch, "E15.46.5", {"start": v(59.7, -50.7) * mm, "mid": v(59.8, -50.33) * mm, "end": v(59.62, -49.98) * mm});
            skArc(sketch, "E15.46.6", {"start": v(58.32, -48.9) * mm, "mid": v(57.89, -48.04) * mm, "end": v(57.5, -47.17) * mm});
            skArc(sketch, "E15.46.7", {"start": v(60.36, -46.36) * mm, "mid": v(59.43, -46.12) * mm, "end": v(58.5, -45.92) * mm});
            skArc(sketch, "E15.46.8", {"start": v(58.5, -45.92) * mm, "mid": v(58.22, -45.95) * mm, "end": v(58, -46.11) * mm});
            skLineSegment(sketch, "E15.46.9", {"start": v(58, -46.11) * mm, "end": v(57.8, -46.38) * mm});
            skLineSegment(sketch, "E15.46.10", {"start": v(57.57, -46.65) * mm, "end": v(57.8, -46.38) * mm});
            skArc(sketch, "E15.46.11", {"start": v(57.57, -46.65) * mm, "mid": v(57.46, -46.9) * mm, "end": v(57.5, -47.17) * mm});
            skArc(sketch, "E15.47.0", {"start": v(65.6, -41.83) * mm, "mid": v(65.99, -41.9) * mm, "end": v(66.3, -41.68) * mm});
            skLineSegment(sketch, "E15.47.1", {"start": v(64.35, -41) * mm, "end": v(65.6, -41.83) * mm});
            skArc(sketch, "E15.47.2", {"start": v(64.35, -41) * mm, "mid": v(64.26, -40.95) * mm, "end": v(64.17, -40.92) * mm});
            skArc(sketch, "E15.47.3", {"start": v(62.36, -43.62) * mm, "mid": v(62.43, -43.7) * mm, "end": v(62.5, -43.76) * mm});
            skLineSegment(sketch, "E15.47.4", {"start": v(62.5, -43.76) * mm, "end": v(63.75, -44.6) * mm});
            skArc(sketch, "E15.47.5", {"start": v(63.88, -45.31) * mm, "mid": v(63.97, -44.93) * mm, "end": v(63.75, -44.6) * mm});
            skArc(sketch, "E15.47.6", {"start": v(62.36, -43.62) * mm, "mid": v(61.85, -42.81) * mm, "end": v(61.39, -41.98) * mm});
            skArc(sketch, "E15.47.7", {"start": v(64.17, -40.92) * mm, "mid": v(63.22, -40.76) * mm, "end": v(62.28, -40.65) * mm});
            skArc(sketch, "E15.47.8", {"start": v(62.28, -40.65) * mm, "mid": v(62, -40.7) * mm, "end": v(61.8, -40.88) * mm});
            skLineSegment(sketch, "E15.47.9", {"start": v(61.8, -40.88) * mm, "end": v(61.62, -41.17) * mm});
            skLineSegment(sketch, "E15.47.10", {"start": v(61.42, -41.45) * mm, "end": v(61.62, -41.17) * mm});
            skArc(sketch, "E15.47.11", {"start": v(61.42, -41.45) * mm, "mid": v(61.33, -41.71) * mm, "end": v(61.39, -41.98) * mm});
            skArc(sketch, "E15.48.0", {"start": v(69, -35.96) * mm, "mid": v(69.39, -36) * mm, "end": v(69.7, -35.74) * mm});
            skLineSegment(sketch, "E15.48.1", {"start": v(67.68, -35.23) * mm, "end": v(69, -35.96) * mm});
            skArc(sketch, "E15.48.2", {"start": v(67.68, -35.23) * mm, "mid": v(67.59, -35.2) * mm, "end": v(67.49, -35.17) * mm});
            skArc(sketch, "E15.48.3", {"start": v(65.93, -38.02) * mm, "mid": v(66, -38.1) * mm, "end": v(66.08, -38.15) * mm});
            skLineSegment(sketch, "E15.48.4", {"start": v(66.08, -38.15) * mm, "end": v(67.4, -38.87) * mm});
            skArc(sketch, "E15.48.5", {"start": v(67.59, -39.57) * mm, "mid": v(67.64, -39.18) * mm, "end": v(67.4, -38.87) * mm});
            skArc(sketch, "E15.48.6", {"start": v(65.93, -38.02) * mm, "mid": v(65.35, -37.26) * mm, "end": v(64.81, -36.47) * mm});
            skArc(sketch, "E15.48.7", {"start": v(67.49, -35.17) * mm, "mid": v(66.54, -35.1) * mm, "end": v(65.58, -35.06) * mm});
            skArc(sketch, "E15.48.8", {"start": v(65.58, -35.06) * mm, "mid": v(65.32, -35.14) * mm, "end": v(65.13, -35.34) * mm});
            skLineSegment(sketch, "E15.48.9", {"start": v(65.13, -35.34) * mm, "end": v(64.97, -35.64) * mm});
            skLineSegment(sketch, "E15.48.10", {"start": v(64.8, -35.94) * mm, "end": v(64.97, -35.64) * mm});
            skArc(sketch, "E15.48.11", {"start": v(64.8, -35.94) * mm, "mid": v(64.73, -36.2) * mm, "end": v(64.81, -36.47) * mm});
            skArc(sketch, "E15.49.0", {"start": v(71.86, -29.8) * mm, "mid": v(72.26, -29.81) * mm, "end": v(72.54, -29.53) * mm});
            skLineSegment(sketch, "E15.49.1", {"start": v(70.5, -29.2) * mm, "end": v(71.86, -29.8) * mm});
            skArc(sketch, "E15.49.2", {"start": v(70.5, -29.2) * mm, "mid": v(70.4, -29.17) * mm, "end": v(70.3, -29.16) * mm});
            skArc(sketch, "E15.49.3", {"start": v(68.99, -32.13) * mm, "mid": v(69.07, -32.2) * mm, "end": v(69.15, -32.24) * mm});
            skLineSegment(sketch, "E15.49.4", {"start": v(69.15, -32.24) * mm, "end": v(70.53, -32.85) * mm});
            skArc(sketch, "E15.49.5", {"start": v(70.78, -33.53) * mm, "mid": v(70.8, -33.14) * mm, "end": v(70.53, -32.85) * mm});
            skArc(sketch, "E15.49.6", {"start": v(68.99, -32.13) * mm, "mid": v(68.35, -31.42) * mm, "end": v(67.74, -30.68) * mm});
            skArc(sketch, "E15.49.7", {"start": v(70.3, -29.16) * mm, "mid": v(69.34, -29.16) * mm, "end": v(68.39, -29.22) * mm});
            skArc(sketch, "E15.49.8", {"start": v(68.39, -29.22) * mm, "mid": v(68.13, -29.31) * mm, "end": v(67.96, -29.53) * mm});
            skLineSegment(sketch, "E15.49.9", {"start": v(67.96, -29.53) * mm, "end": v(67.83, -29.85) * mm});
            skLineSegment(sketch, "E15.49.10", {"start": v(67.68, -30.15) * mm, "end": v(67.83, -29.85) * mm});
            skArc(sketch, "E15.49.11", {"start": v(67.68, -30.15) * mm, "mid": v(67.64, -30.43) * mm, "end": v(67.74, -30.68) * mm});
            skArc(sketch, "E15.50.0", {"start": v(74.19, -23.43) * mm, "mid": v(74.58, -23.4) * mm, "end": v(74.84, -23.1) * mm});
            skLineSegment(sketch, "E15.50.1", {"start": v(72.77, -22.95) * mm, "end": v(74.19, -23.43) * mm});
            skArc(sketch, "E15.50.2", {"start": v(72.77, -22.95) * mm, "mid": v(72.67, -22.92) * mm, "end": v(72.57, -22.92) * mm});
            skArc(sketch, "E15.50.3", {"start": v(71.53, -26) * mm, "mid": v(71.6, -26.05) * mm, "end": v(71.7, -26.1) * mm});
            skLineSegment(sketch, "E15.50.4", {"start": v(71.7, -26.1) * mm, "end": v(73.12, -26.58) * mm});
            skArc(sketch, "E15.50.5", {"start": v(73.43, -27.23) * mm, "mid": v(73.42, -26.84) * mm, "end": v(73.12, -26.58) * mm});
            skArc(sketch, "E15.50.6", {"start": v(71.53, -26) * mm, "mid": v(70.83, -25.35) * mm, "end": v(70.16, -24.66) * mm});
            skArc(sketch, "E15.50.7", {"start": v(72.57, -22.92) * mm, "mid": v(71.62, -23) * mm, "end": v(70.67, -23.14) * mm});
            skArc(sketch, "E15.50.8", {"start": v(70.67, -23.14) * mm, "mid": v(70.42, -23.26) * mm, "end": v(70.27, -23.5) * mm});
            skLineSegment(sketch, "E15.50.9", {"start": v(70.27, -23.5) * mm, "end": v(70.17, -23.82) * mm});
            skLineSegment(sketch, "E15.50.10", {"start": v(70.05, -24.14) * mm, "end": v(70.17, -23.82) * mm});
            skArc(sketch, "E15.50.11", {"start": v(70.05, -24.14) * mm, "mid": v(70.03, -24.42) * mm, "end": v(70.16, -24.66) * mm});
            skArc(sketch, "E15.51.0", {"start": v(75.95, -16.87) * mm, "mid": v(76.34, -16.81) * mm, "end": v(76.57, -16.49) * mm});
            skLineSegment(sketch, "E15.51.1", {"start": v(74.5, -16.52) * mm, "end": v(75.95, -16.87) * mm});
            skArc(sketch, "E15.51.2", {"start": v(74.5, -16.52) * mm, "mid": v(74.4, -16.5) * mm, "end": v(74.3, -16.5) * mm});
            skArc(sketch, "E15.51.3", {"start": v(73.52, -19.66) * mm, "mid": v(73.6, -19.71) * mm, "end": v(73.7, -19.75) * mm});
            skLineSegment(sketch, "E15.51.4", {"start": v(73.7, -19.75) * mm, "end": v(75.16, -20.1) * mm});
            skArc(sketch, "E15.51.5", {"start": v(75.53, -20.73) * mm, "mid": v(75.48, -20.34) * mm, "end": v(75.16, -20.1) * mm});
            skArc(sketch, "E15.51.6", {"start": v(73.52, -19.66) * mm, "mid": v(72.77, -19.08) * mm, "end": v(72.04, -18.45) * mm});
            skArc(sketch, "E15.51.7", {"start": v(74.3, -16.5) * mm, "mid": v(73.35, -16.68) * mm, "end": v(72.42, -16.9) * mm});
            skArc(sketch, "E15.51.8", {"start": v(72.42, -16.9) * mm, "mid": v(72.18, -17.04) * mm, "end": v(72.05, -17.28) * mm});
            skLineSegment(sketch, "E15.51.9", {"start": v(72.05, -17.28) * mm, "end": v(71.98, -17.61) * mm});
            skLineSegment(sketch, "E15.51.10", {"start": v(71.9, -17.94) * mm, "end": v(71.98, -17.61) * mm});
            skArc(sketch, "E15.51.11", {"start": v(71.9, -17.94) * mm, "mid": v(71.9, -18.22) * mm, "end": v(72.04, -18.45) * mm});
            skArc(sketch, "E15.52.0", {"start": v(77.13, -10.19) * mm, "mid": v(77.51, -10.1) * mm, "end": v(77.71, -9.75) * mm});
            skLineSegment(sketch, "E15.52.1", {"start": v(75.65, -9.96) * mm, "end": v(77.13, -10.19) * mm});
            skArc(sketch, "E15.52.2", {"start": v(75.65, -9.96) * mm, "mid": v(75.55, -9.96) * mm, "end": v(75.45, -9.97) * mm});
            skArc(sketch, "E15.52.3", {"start": v(74.95, -13.18) * mm, "mid": v(75.05, -13.22) * mm, "end": v(75.14, -13.25) * mm});
            skLineSegment(sketch, "E15.52.4", {"start": v(75.14, -13.25) * mm, "end": v(76.62, -13.48) * mm});
            skArc(sketch, "E15.52.5", {"start": v(77.05, -14.07) * mm, "mid": v(76.96, -13.68) * mm, "end": v(76.62, -13.48) * mm});
            skArc(sketch, "E15.52.6", {"start": v(74.95, -13.18) * mm, "mid": v(74.15, -12.66) * mm, "end": v(73.38, -12.1) * mm});
            skArc(sketch, "E15.52.7", {"start": v(75.45, -9.97) * mm, "mid": v(74.53, -10.22) * mm, "end": v(73.62, -10.52) * mm});
            skArc(sketch, "E15.52.8", {"start": v(73.62, -10.52) * mm, "mid": v(73.4, -10.68) * mm, "end": v(73.29, -10.93) * mm});
            skLineSegment(sketch, "E15.52.9", {"start": v(73.29, -10.93) * mm, "end": v(73.24, -11.27) * mm});
            skLineSegment(sketch, "E15.52.10", {"start": v(73.18, -11.6) * mm, "end": v(73.24, -11.27) * mm});
            skArc(sketch, "E15.52.11", {"start": v(73.18, -11.6) * mm, "mid": v(73.2, -11.88) * mm, "end": v(73.38, -12.1) * mm});
            skArc(sketch, "E15.53.0", {"start": v(77.72, -3.43) * mm, "mid": v(78.1, -3.3) * mm, "end": v(78.27, -2.94) * mm});
            skLineSegment(sketch, "E15.53.1", {"start": v(76.23, -3.33) * mm, "end": v(77.72, -3.43) * mm});
            skArc(sketch, "E15.53.2", {"start": v(76.23, -3.33) * mm, "mid": v(76.13, -3.33) * mm, "end": v(76.03, -3.36) * mm});
            skArc(sketch, "E15.53.3", {"start": v(75.82, -6.6) * mm, "mid": v(75.91, -6.63) * mm, "end": v(76.01, -6.65) * mm});
            skLineSegment(sketch, "E15.53.4", {"start": v(76.01, -6.65) * mm, "end": v(77.5, -6.75) * mm});
            skArc(sketch, "E15.53.5", {"start": v(77.98, -7.3) * mm, "mid": v(77.86, -6.92) * mm, "end": v(77.5, -6.75) * mm});
            skArc(sketch, "E15.53.6", {"start": v(75.82, -6.6) * mm, "mid": v(74.97, -6.15) * mm, "end": v(74.15, -5.66) * mm});
            skArc(sketch, "E15.53.7", {"start": v(76.03, -3.36) * mm, "mid": v(75.13, -3.69) * mm, "end": v(74.26, -4.06) * mm});
            skArc(sketch, "E15.53.8", {"start": v(74.26, -4.06) * mm, "mid": v(74.05, -4.24) * mm, "end": v(73.96, -4.5) * mm});
            skLineSegment(sketch, "E15.53.9", {"start": v(73.96, -4.5) * mm, "end": v(73.95, -4.85) * mm});
            skLineSegment(sketch, "E15.53.10", {"start": v(73.92, -5.19) * mm, "end": v(73.95, -4.85) * mm});
            skArc(sketch, "E15.53.11", {"start": v(73.92, -5.19) * mm, "mid": v(73.97, -5.46) * mm, "end": v(74.15, -5.66) * mm});
            skArc(sketch, "E15.54.0", {"start": v(77.73, 3.36) * mm, "mid": v(78.09, 3.52) * mm, "end": v(78.22, 3.9) * mm});
            skLineSegment(sketch, "E15.54.1", {"start": v(76.23, 3.33) * mm, "end": v(77.73, 3.36) * mm});
            skArc(sketch, "E15.54.2", {"start": v(76.23, 3.33) * mm, "mid": v(76.13, 3.31) * mm, "end": v(76.03, 3.28) * mm});
            skArc(sketch, "E15.54.3", {"start": v(76.1, 0.04) * mm, "mid": v(76.2, 0) * mm, "end": v(76.3, 0) * mm});
            skLineSegment(sketch, "E15.54.4", {"start": v(76.3, 0) * mm, "end": v(77.8, 0.03) * mm});
            skArc(sketch, "E15.54.5", {"start": v(78.32, -0.48) * mm, "mid": v(78.17, -0.11) * mm, "end": v(77.8, 0.03) * mm});
            skArc(sketch, "E15.54.6", {"start": v(76.1, 0.04) * mm, "mid": v(75.22, 0.4) * mm, "end": v(74.36, 0.82) * mm});
            skArc(sketch, "E15.54.7", {"start": v(76.03, 3.28) * mm, "mid": v(75.17, 2.87) * mm, "end": v(74.33, 2.42) * mm});
            skArc(sketch, "E15.54.8", {"start": v(74.33, 2.42) * mm, "mid": v(74.13, 2.23) * mm, "end": v(74.07, 1.96) * mm});
            skLineSegment(sketch, "E15.54.9", {"start": v(74.07, 1.96) * mm, "end": v(74.09, 1.62) * mm});
            skLineSegment(sketch, "E15.54.10", {"start": v(74.09, 1.28) * mm, "end": v(74.09, 1.62) * mm});
            skArc(sketch, "E15.54.11", {"start": v(74.09, 1.28) * mm, "mid": v(74.16, 1) * mm, "end": v(74.36, 0.82) * mm});
            skArc(sketch, "E15.55.0", {"start": v(77.14, 10.12) * mm, "mid": v(77.48, 10.31) * mm, "end": v(77.59, 10.7) * mm});
            skLineSegment(sketch, "E15.55.1", {"start": v(75.65, 9.96) * mm, "end": v(77.14, 10.12) * mm});
            skArc(sketch, "E15.55.2", {"start": v(75.65, 9.96) * mm, "mid": v(75.55, 9.94) * mm, "end": v(75.46, 9.9) * mm});
            skArc(sketch, "E15.55.3", {"start": v(75.81, 6.67) * mm, "mid": v(75.91, 6.65) * mm, "end": v(76.01, 6.65) * mm});
            skLineSegment(sketch, "E15.55.4", {"start": v(76.01, 6.65) * mm, "end": v(77.5, 6.82) * mm});
            skArc(sketch, "E15.55.5", {"start": v(78.06, 6.35) * mm, "mid": v(77.88, 6.7) * mm, "end": v(77.5, 6.82) * mm});
            skArc(sketch, "E15.55.6", {"start": v(75.81, 6.67) * mm, "mid": v(74.9, 6.96) * mm, "end": v(74, 7.3) * mm});
            skArc(sketch, "E15.55.7", {"start": v(75.46, 9.9) * mm, "mid": v(74.63, 9.42) * mm, "end": v(73.83, 8.9) * mm});
            skArc(sketch, "E15.55.8", {"start": v(73.83, 8.9) * mm, "mid": v(73.66, 8.68) * mm, "end": v(73.62, 8.4) * mm});
            skLineSegment(sketch, "E15.55.9", {"start": v(73.62, 8.4) * mm, "end": v(73.67, 8.07) * mm});
            skLineSegment(sketch, "E15.55.10", {"start": v(73.7, 7.73) * mm, "end": v(73.67, 8.07) * mm});
            skArc(sketch, "E15.55.11", {"start": v(73.7, 7.73) * mm, "mid": v(73.8, 7.47) * mm, "end": v(74, 7.3) * mm});
            skArc(sketch, "E15.56.0", {"start": v(75.96, 16.8) * mm, "mid": v(76.3, 17.03) * mm, "end": v(76.36, 17.42) * mm});
            skLineSegment(sketch, "E15.56.1", {"start": v(74.5, 16.51) * mm, "end": v(75.96, 16.8) * mm});
            skArc(sketch, "E15.56.2", {"start": v(74.5, 16.51) * mm, "mid": v(74.4, 16.48) * mm, "end": v(74.3, 16.44) * mm});
            skArc(sketch, "E15.56.3", {"start": v(74.94, 13.25) * mm, "mid": v(75.04, 13.24) * mm, "end": v(75.14, 13.25) * mm});
            skLineSegment(sketch, "E15.56.4", {"start": v(75.14, 13.25) * mm, "end": v(76.61, 13.54) * mm});
            skArc(sketch, "E15.56.5", {"start": v(77.21, 13.13) * mm, "mid": v(77, 13.46) * mm, "end": v(76.61, 13.54) * mm});
            skArc(sketch, "E15.56.6", {"start": v(74.94, 13.25) * mm, "mid": v(74.01, 13.46) * mm, "end": v(73.1, 13.72) * mm});
            skArc(sketch, "E15.56.7", {"start": v(74.3, 16.44) * mm, "mid": v(73.53, 15.88) * mm, "end": v(72.78, 15.3) * mm});
            skArc(sketch, "E15.56.8", {"start": v(72.78, 15.3) * mm, "mid": v(72.62, 15.07) * mm, "end": v(72.6, 14.8) * mm});
            skLineSegment(sketch, "E15.56.9", {"start": v(72.6, 14.8) * mm, "end": v(72.68, 14.46) * mm});
            skLineSegment(sketch, "E15.56.10", {"start": v(72.74, 14.12) * mm, "end": v(72.68, 14.46) * mm});
            skArc(sketch, "E15.56.11", {"start": v(72.74, 14.12) * mm, "mid": v(72.86, 13.87) * mm, "end": v(73.1, 13.72) * mm});
            skArc(sketch, "E15.57.0", {"start": v(74.21, 23.36) * mm, "mid": v(74.52, 23.61) * mm, "end": v(74.55, 24) * mm});
            skLineSegment(sketch, "E15.57.1", {"start": v(72.77, 22.94) * mm, "end": v(74.21, 23.36) * mm});
            skArc(sketch, "E15.57.2", {"start": v(72.77, 22.94) * mm, "mid": v(72.68, 22.9) * mm, "end": v(72.6, 22.85) * mm});
            skArc(sketch, "E15.57.3", {"start": v(73.5, 19.73) * mm, "mid": v(73.6, 19.73) * mm, "end": v(73.7, 19.75) * mm});
            skLineSegment(sketch, "E15.57.4", {"start": v(73.7, 19.75) * mm, "end": v(75.14, 20.17) * mm});
            skArc(sketch, "E15.57.5", {"start": v(75.77, 19.81) * mm, "mid": v(75.53, 20.12) * mm, "end": v(75.14, 20.17) * mm});
            skArc(sketch, "E15.57.6", {"start": v(73.5, 19.73) * mm, "mid": v(72.56, 19.86) * mm, "end": v(71.62, 20.04) * mm});
            skArc(sketch, "E15.57.7", {"start": v(72.6, 22.85) * mm, "mid": v(71.86, 22.23) * mm, "end": v(71.17, 21.58) * mm});
            skArc(sketch, "E15.57.8", {"start": v(71.17, 21.58) * mm, "mid": v(71.03, 21.34) * mm, "end": v(71.04, 21.06) * mm});
            skLineSegment(sketch, "E15.57.9", {"start": v(71.04, 21.06) * mm, "end": v(71.15, 20.74) * mm});
            skLineSegment(sketch, "E15.57.10", {"start": v(71.23, 20.4) * mm, "end": v(71.15, 20.74) * mm});
            skArc(sketch, "E15.57.11", {"start": v(71.23, 20.4) * mm, "mid": v(71.37, 20.17) * mm, "end": v(71.62, 20.04) * mm});
            skArc(sketch, "E15.58.0", {"start": v(71.9, 29.74) * mm, "mid": v(72.18, 30.02) * mm, "end": v(72.18, 30.41) * mm});
            skLineSegment(sketch, "E15.58.1", {"start": v(70.5, 29.2) * mm, "end": v(71.9, 29.74) * mm});
            skArc(sketch, "E15.58.2", {"start": v(70.5, 29.2) * mm, "mid": v(70.4, 29.15) * mm, "end": v(70.33, 29.09) * mm});
            skArc(sketch, "E15.58.3", {"start": v(71.5, 26.06) * mm, "mid": v(71.6, 26.07) * mm, "end": v(71.7, 26.1) * mm});
            skLineSegment(sketch, "E15.58.4", {"start": v(71.7, 26.1) * mm, "end": v(73.1, 26.64) * mm});
            skArc(sketch, "E15.58.5", {"start": v(73.76, 26.34) * mm, "mid": v(73.5, 26.63) * mm, "end": v(73.1, 26.64) * mm});
            skArc(sketch, "E15.58.6", {"start": v(71.5, 26.06) * mm, "mid": v(70.55, 26.11) * mm, "end": v(69.6, 26.2) * mm});
            skArc(sketch, "E15.58.7", {"start": v(70.33, 29.09) * mm, "mid": v(69.65, 28.41) * mm, "end": v(69.02, 27.7) * mm});
            skArc(sketch, "E15.58.8", {"start": v(69.02, 27.7) * mm, "mid": v(68.9, 27.45) * mm, "end": v(68.94, 27.17) * mm});
            skLineSegment(sketch, "E15.58.9", {"start": v(68.94, 27.17) * mm, "end": v(69.07, 26.86) * mm});
            skLineSegment(sketch, "E15.58.10", {"start": v(69.18, 26.54) * mm, "end": v(69.07, 26.86) * mm});
            skArc(sketch, "E15.58.11", {"start": v(69.18, 26.54) * mm, "mid": v(69.34, 26.31) * mm, "end": v(69.6, 26.2) * mm});
            skArc(sketch, "E15.59.0", {"start": v(69.03, 35.9) * mm, "mid": v(69.28, 36.2) * mm, "end": v(69.25, 36.59) * mm});
            skLineSegment(sketch, "E15.59.1", {"start": v(67.68, 35.23) * mm, "end": v(69.03, 35.9) * mm});
            skArc(sketch, "E15.59.2", {"start": v(67.68, 35.23) * mm, "mid": v(67.6, 35.18) * mm, "end": v(67.52, 35.1) * mm});
            skArc(sketch, "E15.59.3", {"start": v(68.96, 32.2) * mm, "mid": v(69.06, 32.21) * mm, "end": v(69.15, 32.25) * mm});
            skLineSegment(sketch, "E15.59.4", {"start": v(69.15, 32.25) * mm, "end": v(70.5, 32.91) * mm});
            skArc(sketch, "E15.59.5", {"start": v(71.18, 32.67) * mm, "mid": v(70.9, 32.93) * mm, "end": v(70.5, 32.91) * mm});
            skArc(sketch, "E15.59.6", {"start": v(68.96, 32.2) * mm, "mid": v(68, 32.16) * mm, "end": v(67.05, 32.17) * mm});
            skArc(sketch, "E15.59.7", {"start": v(67.52, 35.1) * mm, "mid": v(66.91, 34.37) * mm, "end": v(66.34, 33.6) * mm});
            skArc(sketch, "E15.59.8", {"start": v(66.34, 33.6) * mm, "mid": v(66.25, 33.35) * mm, "end": v(66.3, 33.08) * mm});
            skLineSegment(sketch, "E15.59.9", {"start": v(66.3, 33.08) * mm, "end": v(66.46, 32.78) * mm});
            skLineSegment(sketch, "E15.59.10", {"start": v(66.6, 32.47) * mm, "end": v(66.46, 32.78) * mm});
            skArc(sketch, "E15.59.11", {"start": v(66.6, 32.47) * mm, "mid": v(66.79, 32.26) * mm, "end": v(67.05, 32.17) * mm});
            skArc(sketch, "E15.60.0", {"start": v(65.63, 41.77) * mm, "mid": v(65.87, 42.1) * mm, "end": v(65.8, 42.48) * mm});
            skLineSegment(sketch, "E15.60.1", {"start": v(64.35, 41) * mm, "end": v(65.63, 41.77) * mm});
            skArc(sketch, "E15.60.2", {"start": v(64.35, 41) * mm, "mid": v(64.27, 40.93) * mm, "end": v(64.2, 40.86) * mm});
            skArc(sketch, "E15.60.3", {"start": v(65.9, 38.08) * mm, "mid": v(65.99, 38.1) * mm, "end": v(66.08, 38.15) * mm});
            skLineSegment(sketch, "E15.60.4", {"start": v(66.08, 38.15) * mm, "end": v(67.36, 38.93) * mm});
            skArc(sketch, "E15.60.5", {"start": v(68.06, 38.75) * mm, "mid": v(67.75, 38.99) * mm, "end": v(67.36, 38.93) * mm});
            skArc(sketch, "E15.60.6", {"start": v(65.9, 38.08) * mm, "mid": v(64.94, 37.96) * mm, "end": v(64, 37.9) * mm});
            skArc(sketch, "E15.60.7", {"start": v(64.2, 40.86) * mm, "mid": v(63.66, 40.07) * mm, "end": v(63.16, 39.26) * mm});
            skArc(sketch, "E15.60.8", {"start": v(63.16, 39.26) * mm, "mid": v(63.09, 39) * mm, "end": v(63.17, 38.73) * mm});
            skLineSegment(sketch, "E15.60.9", {"start": v(63.17, 38.73) * mm, "end": v(63.35, 38.44) * mm});
            skLineSegment(sketch, "E15.60.10", {"start": v(63.52, 38.15) * mm, "end": v(63.35, 38.44) * mm});
            skArc(sketch, "E15.60.11", {"start": v(63.52, 38.15) * mm, "mid": v(63.72, 37.95) * mm, "end": v(64, 37.9) * mm});
            skArc(sketch, "E15.61.0", {"start": v(61.74, 47.33) * mm, "mid": v(61.95, 47.67) * mm, "end": v(61.85, 48.06) * mm});
            skLineSegment(sketch, "E15.61.1", {"start": v(60.53, 46.45) * mm, "end": v(61.74, 47.33) * mm});
            skArc(sketch, "E15.61.2", {"start": v(60.53, 46.45) * mm, "mid": v(60.46, 46.38) * mm, "end": v(60.4, 46.3) * mm});
            skArc(sketch, "E15.61.3", {"start": v(62.32, 43.68) * mm, "mid": v(62.41, 43.72) * mm, "end": v(62.5, 43.77) * mm});
            skLineSegment(sketch, "E15.61.4", {"start": v(62.5, 43.77) * mm, "end": v(63.71, 44.65) * mm});
            skArc(sketch, "E15.61.5", {"start": v(64.43, 44.53) * mm, "mid": v(64.1, 44.74) * mm, "end": v(63.71, 44.65) * mm});
            skArc(sketch, "E15.61.6", {"start": v(62.32, 43.68) * mm, "mid": v(61.39, 43.48) * mm, "end": v(60.44, 43.32) * mm});
            skArc(sketch, "E15.61.7", {"start": v(60.4, 46.3) * mm, "mid": v(59.93, 45.47) * mm, "end": v(59.5, 44.62) * mm});
            skArc(sketch, "E15.61.8", {"start": v(59.5, 44.62) * mm, "mid": v(59.45, 44.35) * mm, "end": v(59.55, 44.09) * mm});
            skLineSegment(sketch, "E15.61.9", {"start": v(59.55, 44.09) * mm, "end": v(59.76, 43.82) * mm});
            skLineSegment(sketch, "E15.61.10", {"start": v(59.96, 43.54) * mm, "end": v(59.76, 43.82) * mm});
            skArc(sketch, "E15.61.11", {"start": v(59.96, 43.54) * mm, "mid": v(60.17, 43.36) * mm, "end": v(60.44, 43.32) * mm});
            skArc(sketch, "E15.62.0", {"start": v(57.38, 52.54) * mm, "mid": v(57.56, 52.9) * mm, "end": v(57.42, 53.26) * mm});
            skLineSegment(sketch, "E15.62.1", {"start": v(56.26, 51.55) * mm, "end": v(57.38, 52.54) * mm});
            skArc(sketch, "E15.62.2", {"start": v(56.26, 51.55) * mm, "mid": v(56.19, 51.47) * mm, "end": v(56.14, 51.39) * mm});
            skArc(sketch, "E15.62.3", {"start": v(58.28, 48.95) * mm, "mid": v(58.37, 48.99) * mm, "end": v(58.45, 49.05) * mm});
            skLineSegment(sketch, "E15.62.4", {"start": v(58.45, 49.05) * mm, "end": v(59.58, 50.04) * mm});
            skArc(sketch, "E15.62.5", {"start": v(60.3, 49.98) * mm, "mid": v(59.95, 50.16) * mm, "end": v(59.58, 50.04) * mm});
            skArc(sketch, "E15.62.6", {"start": v(58.28, 48.95) * mm, "mid": v(57.36, 48.66) * mm, "end": v(56.44, 48.43) * mm});
            skArc(sketch, "E15.62.7", {"start": v(56.14, 51.39) * mm, "mid": v(55.74, 50.52) * mm, "end": v(55.38, 49.63) * mm});
            skArc(sketch, "E15.62.8", {"start": v(55.38, 49.63) * mm, "mid": v(55.36, 49.36) * mm, "end": v(55.48, 49.11) * mm});
            skLineSegment(sketch, "E15.62.9", {"start": v(55.48, 49.11) * mm, "end": v(55.72, 48.86) * mm});
            skLineSegment(sketch, "E15.62.10", {"start": v(55.93, 48.6) * mm, "end": v(55.72, 48.86) * mm});
            skArc(sketch, "E15.62.11", {"start": v(55.93, 48.6) * mm, "mid": v(56.16, 48.44) * mm, "end": v(56.44, 48.43) * mm});
            skArc(sketch, "E15.63.0", {"start": v(52.59, 57.34) * mm, "mid": v(52.73, 57.7) * mm, "end": v(52.56, 58.06) * mm});
            skLineSegment(sketch, "E15.63.1", {"start": v(51.55, 56.25) * mm, "end": v(52.59, 57.34) * mm});
            skArc(sketch, "E15.63.2", {"start": v(51.55, 56.25) * mm, "mid": v(51.49, 56.17) * mm, "end": v(51.44, 56.09) * mm});
            skArc(sketch, "E15.63.3", {"start": v(53.79, 53.84) * mm, "mid": v(53.88, 53.89) * mm, "end": v(53.95, 53.95) * mm});
            skLineSegment(sketch, "E15.63.4", {"start": v(53.95, 53.95) * mm, "end": v(54.99, 55.04) * mm});
            skArc(sketch, "E15.63.5", {"start": v(55.72, 55.04) * mm, "mid": v(55.35, 55.2) * mm, "end": v(54.99, 55.04) * mm});
            skArc(sketch, "E15.63.6", {"start": v(53.79, 53.84) * mm, "mid": v(52.9, 53.48) * mm, "end": v(52, 53.16) * mm});
            skArc(sketch, "E15.63.7", {"start": v(51.44, 56.09) * mm, "mid": v(51.12, 55.19) * mm, "end": v(50.84, 54.27) * mm});
            skArc(sketch, "E15.63.8", {"start": v(50.84, 54.27) * mm, "mid": v(50.85, 54) * mm, "end": v(51, 53.76) * mm});
            skLineSegment(sketch, "E15.63.9", {"start": v(51, 53.76) * mm, "end": v(51.25, 53.53) * mm});
            skLineSegment(sketch, "E15.63.10", {"start": v(51.49, 53.29) * mm, "end": v(51.25, 53.53) * mm});
            skArc(sketch, "E15.63.11", {"start": v(51.49, 53.29) * mm, "mid": v(51.73, 53.15) * mm, "end": v(52, 53.16) * mm});
            skArc(sketch, "E15.64.0", {"start": v(47.39, 61.7) * mm, "mid": v(47.5, 62.08) * mm, "end": v(47.3, 62.42) * mm});
            skLineSegment(sketch, "E15.64.1", {"start": v(46.45, 60.53) * mm, "end": v(47.39, 61.7) * mm});
            skArc(sketch, "E15.64.2", {"start": v(46.45, 60.53) * mm, "mid": v(46.4, 60.45) * mm, "end": v(46.36, 60.36) * mm});
            skArc(sketch, "E15.64.3", {"start": v(48.9, 58.32) * mm, "mid": v(48.97, 58.38) * mm, "end": v(49.04, 58.45) * mm});
            skLineSegment(sketch, "E15.64.4", {"start": v(49.04, 58.45) * mm, "end": v(49.98, 59.62) * mm});
            skArc(sketch, "E15.64.5", {"start": v(50.7, 59.7) * mm, "mid": v(50.33, 59.8) * mm, "end": v(49.98, 59.62) * mm});
            skArc(sketch, "E15.64.6", {"start": v(48.9, 58.32) * mm, "mid": v(48.04, 57.89) * mm, "end": v(47.17, 57.5) * mm});
            skArc(sketch, "E15.64.7", {"start": v(46.36, 60.36) * mm, "mid": v(46.12, 59.43) * mm, "end": v(45.92, 58.5) * mm});
            skArc(sketch, "E15.64.8", {"start": v(45.92, 58.5) * mm, "mid": v(45.95, 58.22) * mm, "end": v(46.11, 58) * mm});
            skLineSegment(sketch, "E15.64.9", {"start": v(46.11, 58) * mm, "end": v(46.38, 57.8) * mm});
            skLineSegment(sketch, "E15.64.10", {"start": v(46.65, 57.57) * mm, "end": v(46.38, 57.8) * mm});
            skArc(sketch, "E15.64.11", {"start": v(46.65, 57.57) * mm, "mid": v(46.9, 57.46) * mm, "end": v(47.17, 57.5) * mm});
            skArc(sketch, "E15.65.0", {"start": v(41.83, 65.6) * mm, "mid": v(41.9, 65.99) * mm, "end": v(41.68, 66.3) * mm});
            skLineSegment(sketch, "E15.65.1", {"start": v(41, 64.35) * mm, "end": v(41.83, 65.6) * mm});
            skArc(sketch, "E15.65.2", {"start": v(41, 64.35) * mm, "mid": v(40.95, 64.26) * mm, "end": v(40.92, 64.17) * mm});
            skArc(sketch, "E15.65.3", {"start": v(43.62, 62.36) * mm, "mid": v(43.7, 62.43) * mm, "end": v(43.76, 62.5) * mm});
            skLineSegment(sketch, "E15.65.4", {"start": v(43.76, 62.5) * mm, "end": v(44.6, 63.75) * mm});
            skArc(sketch, "E15.65.5", {"start": v(45.31, 63.88) * mm, "mid": v(44.93, 63.97) * mm, "end": v(44.6, 63.75) * mm});
            skArc(sketch, "E15.65.6", {"start": v(43.62, 62.36) * mm, "mid": v(42.81, 61.85) * mm, "end": v(41.98, 61.39) * mm});
            skArc(sketch, "E15.65.7", {"start": v(40.92, 64.17) * mm, "mid": v(40.76, 63.22) * mm, "end": v(40.65, 62.28) * mm});
            skArc(sketch, "E15.65.8", {"start": v(40.65, 62.28) * mm, "mid": v(40.7, 62) * mm, "end": v(40.88, 61.8) * mm});
            skLineSegment(sketch, "E15.65.9", {"start": v(40.88, 61.8) * mm, "end": v(41.17, 61.62) * mm});
            skLineSegment(sketch, "E15.65.10", {"start": v(41.45, 61.42) * mm, "end": v(41.17, 61.62) * mm});
            skArc(sketch, "E15.65.11", {"start": v(41.45, 61.42) * mm, "mid": v(41.71, 61.33) * mm, "end": v(41.98, 61.39) * mm});
            skArc(sketch, "E15.66.0", {"start": v(35.96, 69) * mm, "mid": v(36, 69.39) * mm, "end": v(35.74, 69.7) * mm});
            skLineSegment(sketch, "E15.66.1", {"start": v(35.23, 67.68) * mm, "end": v(35.96, 69) * mm});
            skArc(sketch, "E15.66.2", {"start": v(35.23, 67.68) * mm, "mid": v(35.2, 67.59) * mm, "end": v(35.17, 67.49) * mm});
            skArc(sketch, "E15.66.3", {"start": v(38.02, 65.93) * mm, "mid": v(38.1, 66) * mm, "end": v(38.15, 66.08) * mm});
            skLineSegment(sketch, "E15.66.4", {"start": v(38.15, 66.08) * mm, "end": v(38.87, 67.4) * mm});
            skArc(sketch, "E15.66.5", {"start": v(39.57, 67.59) * mm, "mid": v(39.18, 67.64) * mm, "end": v(38.87, 67.4) * mm});
            skArc(sketch, "E15.66.6", {"start": v(38.02, 65.93) * mm, "mid": v(37.26, 65.35) * mm, "end": v(36.47, 64.81) * mm});
            skArc(sketch, "E15.66.7", {"start": v(35.17, 67.49) * mm, "mid": v(35.1, 66.54) * mm, "end": v(35.06, 65.58) * mm});
            skArc(sketch, "E15.66.8", {"start": v(35.06, 65.58) * mm, "mid": v(35.14, 65.32) * mm, "end": v(35.34, 65.13) * mm});
            skLineSegment(sketch, "E15.66.9", {"start": v(35.34, 65.13) * mm, "end": v(35.64, 64.97) * mm});
            skLineSegment(sketch, "E15.66.10", {"start": v(35.94, 64.8) * mm, "end": v(35.64, 64.97) * mm});
            skArc(sketch, "E15.66.11", {"start": v(35.94, 64.8) * mm, "mid": v(36.2, 64.73) * mm, "end": v(36.47, 64.81) * mm});
            skArc(sketch, "E15.67.0", {"start": v(29.8, 71.86) * mm, "mid": v(29.81, 72.26) * mm, "end": v(29.53, 72.54) * mm});
            skLineSegment(sketch, "E15.67.1", {"start": v(29.2, 70.5) * mm, "end": v(29.8, 71.86) * mm});
            skArc(sketch, "E15.67.2", {"start": v(29.2, 70.5) * mm, "mid": v(29.17, 70.4) * mm, "end": v(29.16, 70.3) * mm});
            skArc(sketch, "E15.67.3", {"start": v(32.13, 68.99) * mm, "mid": v(32.2, 69.07) * mm, "end": v(32.24, 69.15) * mm});
            skLineSegment(sketch, "E15.67.4", {"start": v(32.24, 69.15) * mm, "end": v(32.85, 70.53) * mm});
            skArc(sketch, "E15.67.5", {"start": v(33.53, 70.78) * mm, "mid": v(33.14, 70.8) * mm, "end": v(32.85, 70.53) * mm});
            skArc(sketch, "E15.67.6", {"start": v(32.13, 68.99) * mm, "mid": v(31.42, 68.35) * mm, "end": v(30.68, 67.74) * mm});
            skArc(sketch, "E15.67.7", {"start": v(29.16, 70.3) * mm, "mid": v(29.16, 69.34) * mm, "end": v(29.22, 68.39) * mm});
            skArc(sketch, "E15.67.8", {"start": v(29.22, 68.39) * mm, "mid": v(29.31, 68.13) * mm, "end": v(29.53, 67.96) * mm});
            skLineSegment(sketch, "E15.67.9", {"start": v(29.53, 67.96) * mm, "end": v(29.85, 67.83) * mm});
            skLineSegment(sketch, "E15.67.10", {"start": v(30.15, 67.68) * mm, "end": v(29.85, 67.83) * mm});
            skArc(sketch, "E15.67.11", {"start": v(30.15, 67.68) * mm, "mid": v(30.43, 67.64) * mm, "end": v(30.68, 67.74) * mm});
            skArc(sketch, "E15.68.0", {"start": v(23.43, 74.19) * mm, "mid": v(23.4, 74.58) * mm, "end": v(23.1, 74.84) * mm});
            skLineSegment(sketch, "E15.68.1", {"start": v(22.95, 72.77) * mm, "end": v(23.43, 74.19) * mm});
            skArc(sketch, "E15.68.2", {"start": v(22.95, 72.77) * mm, "mid": v(22.92, 72.67) * mm, "end": v(22.92, 72.57) * mm});
            skArc(sketch, "E15.68.3", {"start": v(26, 71.53) * mm, "mid": v(26.05, 71.6) * mm, "end": v(26.1, 71.7) * mm});
            skLineSegment(sketch, "E15.68.4", {"start": v(26.1, 71.7) * mm, "end": v(26.58, 73.12) * mm});
            skArc(sketch, "E15.68.5", {"start": v(27.23, 73.43) * mm, "mid": v(26.84, 73.42) * mm, "end": v(26.58, 73.12) * mm});
            skArc(sketch, "E15.68.6", {"start": v(26, 71.53) * mm, "mid": v(25.35, 70.83) * mm, "end": v(24.66, 70.16) * mm});
            skArc(sketch, "E15.68.7", {"start": v(22.92, 72.57) * mm, "mid": v(23, 71.62) * mm, "end": v(23.14, 70.67) * mm});
            skArc(sketch, "E15.68.8", {"start": v(23.14, 70.67) * mm, "mid": v(23.26, 70.42) * mm, "end": v(23.5, 70.27) * mm});
            skLineSegment(sketch, "E15.68.9", {"start": v(23.5, 70.27) * mm, "end": v(23.82, 70.17) * mm});
            skLineSegment(sketch, "E15.68.10", {"start": v(24.14, 70.05) * mm, "end": v(23.82, 70.17) * mm});
            skArc(sketch, "E15.68.11", {"start": v(24.14, 70.05) * mm, "mid": v(24.42, 70.03) * mm, "end": v(24.66, 70.16) * mm});
            skArc(sketch, "E15.69.0", {"start": v(16.87, 75.95) * mm, "mid": v(16.81, 76.34) * mm, "end": v(16.49, 76.57) * mm});
            skLineSegment(sketch, "E15.69.1", {"start": v(16.52, 74.5) * mm, "end": v(16.87, 75.95) * mm});
            skArc(sketch, "E15.69.2", {"start": v(16.52, 74.5) * mm, "mid": v(16.5, 74.4) * mm, "end": v(16.5, 74.3) * mm});
            skArc(sketch, "E15.69.3", {"start": v(19.66, 73.52) * mm, "mid": v(19.71, 73.6) * mm, "end": v(19.75, 73.7) * mm});
            skLineSegment(sketch, "E15.69.4", {"start": v(19.75, 73.7) * mm, "end": v(20.1, 75.16) * mm});
            skArc(sketch, "E15.69.5", {"start": v(20.73, 75.53) * mm, "mid": v(20.34, 75.48) * mm, "end": v(20.1, 75.16) * mm});
            skArc(sketch, "E15.69.6", {"start": v(19.66, 73.52) * mm, "mid": v(19.08, 72.77) * mm, "end": v(18.45, 72.04) * mm});
            skArc(sketch, "E15.69.7", {"start": v(16.5, 74.3) * mm, "mid": v(16.68, 73.35) * mm, "end": v(16.9, 72.42) * mm});
            skArc(sketch, "E15.69.8", {"start": v(16.9, 72.42) * mm, "mid": v(17.04, 72.18) * mm, "end": v(17.28, 72.05) * mm});
            skLineSegment(sketch, "E15.69.9", {"start": v(17.28, 72.05) * mm, "end": v(17.61, 71.98) * mm});
            skLineSegment(sketch, "E15.69.10", {"start": v(17.94, 71.9) * mm, "end": v(17.61, 71.98) * mm});
            skArc(sketch, "E15.69.11", {"start": v(17.94, 71.9) * mm, "mid": v(18.22, 71.9) * mm, "end": v(18.45, 72.04) * mm});
            skArc(sketch, "E15.70.0", {"start": v(10.19, 77.13) * mm, "mid": v(10.1, 77.51) * mm, "end": v(9.75, 77.71) * mm});
            skLineSegment(sketch, "E15.70.1", {"start": v(9.96, 75.65) * mm, "end": v(10.19, 77.13) * mm});
            skArc(sketch, "E15.70.2", {"start": v(9.96, 75.65) * mm, "mid": v(9.96, 75.55) * mm, "end": v(9.97, 75.45) * mm});
            skArc(sketch, "E15.70.3", {"start": v(13.18, 74.95) * mm, "mid": v(13.22, 75.05) * mm, "end": v(13.25, 75.14) * mm});
            skLineSegment(sketch, "E15.70.4", {"start": v(13.25, 75.14) * mm, "end": v(13.48, 76.62) * mm});
            skArc(sketch, "E15.70.5", {"start": v(14.07, 77.05) * mm, "mid": v(13.68, 76.96) * mm, "end": v(13.48, 76.62) * mm});
            skArc(sketch, "E15.70.6", {"start": v(13.18, 74.95) * mm, "mid": v(12.66, 74.15) * mm, "end": v(12.1, 73.38) * mm});
            skArc(sketch, "E15.70.7", {"start": v(9.97, 75.45) * mm, "mid": v(10.22, 74.53) * mm, "end": v(10.52, 73.62) * mm});
            skArc(sketch, "E15.70.8", {"start": v(10.52, 73.62) * mm, "mid": v(10.68, 73.4) * mm, "end": v(10.93, 73.29) * mm});
            skLineSegment(sketch, "E15.70.9", {"start": v(10.93, 73.29) * mm, "end": v(11.27, 73.24) * mm});
            skLineSegment(sketch, "E15.70.10", {"start": v(11.6, 73.18) * mm, "end": v(11.27, 73.24) * mm});
            skArc(sketch, "E15.70.11", {"start": v(11.6, 73.18) * mm, "mid": v(11.88, 73.2) * mm, "end": v(12.1, 73.38) * mm});
            skArc(sketch, "E15.71.0", {"start": v(3.43, 77.72) * mm, "mid": v(3.3, 78.1) * mm, "end": v(2.94, 78.27) * mm});
            skLineSegment(sketch, "E15.71.1", {"start": v(3.33, 76.23) * mm, "end": v(3.43, 77.72) * mm});
            skArc(sketch, "E15.71.2", {"start": v(3.33, 76.23) * mm, "mid": v(3.33, 76.13) * mm, "end": v(3.36, 76.03) * mm});
            skArc(sketch, "E15.71.3", {"start": v(6.6, 75.82) * mm, "mid": v(6.63, 75.91) * mm, "end": v(6.65, 76.01) * mm});
            skLineSegment(sketch, "E15.71.4", {"start": v(6.65, 76.01) * mm, "end": v(6.75, 77.5) * mm});
            skArc(sketch, "E15.71.5", {"start": v(7.3, 77.98) * mm, "mid": v(6.92, 77.86) * mm, "end": v(6.75, 77.5) * mm});
            skArc(sketch, "E15.71.6", {"start": v(6.6, 75.82) * mm, "mid": v(6.15, 74.97) * mm, "end": v(5.66, 74.15) * mm});
            skArc(sketch, "E15.71.7", {"start": v(3.36, 76.03) * mm, "mid": v(3.69, 75.13) * mm, "end": v(4.06, 74.26) * mm});
            skArc(sketch, "E15.71.8", {"start": v(4.06, 74.26) * mm, "mid": v(4.24, 74.05) * mm, "end": v(4.5, 73.96) * mm});
            skLineSegment(sketch, "E15.71.9", {"start": v(4.5, 73.96) * mm, "end": v(4.85, 73.95) * mm});
            skLineSegment(sketch, "E15.71.10", {"start": v(5.19, 73.92) * mm, "end": v(4.85, 73.95) * mm});
            skArc(sketch, "E15.71.11", {"start": v(5.19, 73.92) * mm, "mid": v(5.46, 73.97) * mm, "end": v(5.66, 74.15) * mm});
            skArc(sketch, "E16.trimOffspring", {"start": v(-10.7, 77.59) * mm, "mid": v(-11.91, 77.4) * mm, "end": v(-13.13, 77.21) * mm});
            skArc(sketch, "E17.trimOffspring", {"start": v(-17.42, 76.36) * mm, "mid": v(-18.62, 76.08) * mm, "end": v(-19.81, 75.77) * mm});
            skArc(sketch, "E18.trimOffspring", {"start": v(-24, 74.55) * mm, "mid": v(-25.18, 74.16) * mm, "end": v(-26.34, 73.76) * mm});
            skArc(sketch, "E19.trimOffspring", {"start": v(-72.18, -30.41) * mm, "mid": v(-71.69, -31.54) * mm, "end": v(-71.18, -32.67) * mm});
            skArc(sketch, "E20.trimOffspring", {"start": v(-74.55, -24) * mm, "mid": v(-74.16, -25.18) * mm, "end": v(-73.76, -26.34) * mm});
            skArc(sketch, "E21.trimOffspring", {"start": v(-76.36, -17.42) * mm, "mid": v(-76.08, -18.62) * mm, "end": v(-75.77, -19.81) * mm});
            skArc(sketch, "E22.trimOffspring", {"start": v(-69.25, -36.59) * mm, "mid": v(-68.67, -37.67) * mm, "end": v(-68.06, -38.75) * mm});
            skArc(sketch, "E23.trimOffspring", {"start": v(-77.59, -10.7) * mm, "mid": v(-77.4, -11.91) * mm, "end": v(-77.21, -13.13) * mm});
            skArc(sketch, "E24.trimOffspring", {"start": v(-65.8, -42.48) * mm, "mid": v(-65.12, -43.51) * mm, "end": v(-64.43, -44.53) * mm});
            skArc(sketch, "E25.trimOffspring", {"start": v(-61.85, -48.06) * mm, "mid": v(-61.08, -49.02) * mm, "end": v(-60.3, -49.98) * mm});
            skArc(sketch, "E26.trimOffspring", {"start": v(-57.42, -53.26) * mm, "mid": v(-56.58, -54.16) * mm, "end": v(-55.72, -55.04) * mm});
            skArc(sketch, "E27.trimOffspring", {"start": v(-52.56, -58.06) * mm, "mid": v(-51.64, -58.88) * mm, "end": v(-50.7, -59.7) * mm});
            skArc(sketch, "E28.trimOffspring", {"start": v(-47.3, -62.42) * mm, "mid": v(-46.31, -63.16) * mm, "end": v(-45.31, -63.88) * mm});
            skArc(sketch, "E29.trimOffspring", {"start": v(-41.68, -66.3) * mm, "mid": v(-40.63, -66.96) * mm, "end": v(-39.57, -67.59) * mm});
            skArc(sketch, "E30.trimOffspring", {"start": v(-35.74, -69.7) * mm, "mid": v(-34.64, -70.24) * mm, "end": v(-33.53, -70.78) * mm});
            skArc(sketch, "E31.trimOffspring", {"start": v(-29.53, -72.54) * mm, "mid": v(-28.39, -73) * mm, "end": v(-27.23, -73.43) * mm});
            skArc(sketch, "E32.trimOffspring", {"start": v(-23.1, -74.84) * mm, "mid": v(-21.92, -75.2) * mm, "end": v(-20.73, -75.53) * mm});
            skArc(sketch, "E33.trimOffspring", {"start": v(-16.49, -76.57) * mm, "mid": v(-15.28, -76.82) * mm, "end": v(-14.07, -77.05) * mm});
            skArc(sketch, "E34.trimOffspring", {"start": v(36.59, -69.25) * mm, "mid": v(37.67, -68.67) * mm, "end": v(38.75, -68.06) * mm});
            skArc(sketch, "E35.trimOffspring", {"start": v(42.48, -65.8) * mm, "mid": v(43.51, -65.12) * mm, "end": v(44.53, -64.43) * mm});
            skArc(sketch, "E36.trimOffspring", {"start": v(48.06, -61.85) * mm, "mid": v(49.02, -61.08) * mm, "end": v(49.98, -60.3) * mm});
            skArc(sketch, "E37.trimOffspring", {"start": v(53.26, -57.42) * mm, "mid": v(54.16, -56.58) * mm, "end": v(55.04, -55.72) * mm});
            skArc(sketch, "E38.trimOffspring", {"start": v(58.06, -52.56) * mm, "mid": v(58.88, -51.64) * mm, "end": v(59.7, -50.7) * mm});
            skArc(sketch, "E39.trimOffspring", {"start": v(62.42, -47.3) * mm, "mid": v(63.16, -46.31) * mm, "end": v(63.88, -45.31) * mm});
            skArc(sketch, "E40.trimOffspring", {"start": v(30.41, -72.18) * mm, "mid": v(31.54, -71.69) * mm, "end": v(32.67, -71.18) * mm});
            skArc(sketch, "E41.trimOffspring", {"start": v(24, -74.55) * mm, "mid": v(25.18, -74.16) * mm, "end": v(26.34, -73.76) * mm});
            skArc(sketch, "E42.trimOffspring", {"start": v(17.42, -76.36) * mm, "mid": v(18.62, -76.08) * mm, "end": v(19.81, -75.77) * mm});
            skArc(sketch, "E43.trimOffspring", {"start": v(10.7, -77.59) * mm, "mid": v(11.91, -77.4) * mm, "end": v(13.13, -77.21) * mm});
            skArc(sketch, "E44.trimOffspring", {"start": v(47.3, 62.42) * mm, "mid": v(46.31, 63.16) * mm, "end": v(45.31, 63.88) * mm});
            skArc(sketch, "E45.trimOffspring", {"start": v(52.56, 58.06) * mm, "mid": v(51.64, 58.88) * mm, "end": v(50.7, 59.7) * mm});
            skArc(sketch, "E46.trimOffspring", {"start": v(57.42, 53.26) * mm, "mid": v(56.58, 54.16) * mm, "end": v(55.72, 55.04) * mm});
            skArc(sketch, "E47.trimOffspring", {"start": v(61.85, 48.06) * mm, "mid": v(61.08, 49.02) * mm, "end": v(60.3, 49.98) * mm});
            skArc(sketch, "E48.trimOffspring", {"start": v(65.8, 42.48) * mm, "mid": v(65.12, 43.51) * mm, "end": v(64.43, 44.53) * mm});
            skArc(sketch, "E49.trimOffspring", {"start": v(69.25, 36.59) * mm, "mid": v(68.67, 37.67) * mm, "end": v(68.06, 38.75) * mm});
            skArc(sketch, "E50.trimOffspring", {"start": v(72.18, 30.41) * mm, "mid": v(71.69, 31.54) * mm, "end": v(71.18, 32.67) * mm});
            skArc(sketch, "E51.trimOffspring", {"start": v(74.55, 24) * mm, "mid": v(74.16, 25.18) * mm, "end": v(73.76, 26.34) * mm});
            skArc(sketch, "E52.trimOffspring", {"start": v(76.36, 17.42) * mm, "mid": v(76.08, 18.62) * mm, "end": v(75.77, 19.81) * mm});
            skArc(sketch, "E53.trimOffspring", {"start": v(77.59, 10.7) * mm, "mid": v(77.4, 11.91) * mm, "end": v(77.21, 13.13) * mm});
            skArc(sketch, "E54.trimOffspring", {"start": v(78.22, 3.9) * mm, "mid": v(78.15, 5.12) * mm, "end": v(78.06, 6.35) * mm});
            skArc(sketch, "E55.trimOffspring", {"start": v(78.27, -2.94) * mm, "mid": v(78.3, -1.7) * mm, "end": v(78.32, -0.48) * mm});
            skArc(sketch, "E56.trimOffspring", {"start": v(77.71, -9.75) * mm, "mid": v(77.86, -8.53) * mm, "end": v(77.98, -7.3) * mm});
            skArc(sketch, "E57.trimOffspring", {"start": v(76.57, -16.49) * mm, "mid": v(76.82, -15.28) * mm, "end": v(77.05, -14.07) * mm});
            skArc(sketch, "E58.trimOffspring", {"start": v(74.84, -23.1) * mm, "mid": v(75.2, -21.92) * mm, "end": v(75.53, -20.73) * mm});
            skArc(sketch, "E59.trimOffspring", {"start": v(72.54, -29.53) * mm, "mid": v(73, -28.39) * mm, "end": v(73.43, -27.23) * mm});
            skArc(sketch, "E60.trimOffspring", {"start": v(2.94, 78.27) * mm, "mid": v(1.7, 78.3) * mm, "end": v(0.48, 78.32) * mm});
            skArc(sketch, "E61.trimOffspring", {"start": v(9.75, 77.71) * mm, "mid": v(8.53, 77.86) * mm, "end": v(7.3, 77.98) * mm});
            skArc(sketch, "E62.trimOffspring", {"start": v(16.49, 76.57) * mm, "mid": v(15.28, 76.82) * mm, "end": v(14.07, 77.05) * mm});
            skArc(sketch, "E63.trimOffspring", {"start": v(23.1, 74.84) * mm, "mid": v(21.92, 75.2) * mm, "end": v(20.73, 75.53) * mm});
            skArc(sketch, "E64.trimOffspring", {"start": v(29.53, 72.54) * mm, "mid": v(28.39, 73) * mm, "end": v(27.23, 73.43) * mm});
            skArc(sketch, "E65.trimOffspring", {"start": v(35.74, 69.7) * mm, "mid": v(34.64, 70.24) * mm, "end": v(33.53, 70.78) * mm});
            skArc(sketch, "E66.trimOffspring", {"start": v(41.68, 66.3) * mm, "mid": v(40.63, 66.96) * mm, "end": v(39.57, 67.59) * mm});
            skArc(sketch, "E67.trimOffspring", {"start": v(-30.41, 72.18) * mm, "mid": v(-31.54, 71.69) * mm, "end": v(-32.67, 71.18) * mm});
            skArc(sketch, "E68.trimOffspring", {"start": v(-36.59, 69.25) * mm, "mid": v(-37.67, 68.67) * mm, "end": v(-38.75, 68.06) * mm});
            skArc(sketch, "E69.trimOffspring", {"start": v(-42.48, 65.8) * mm, "mid": v(-43.51, 65.12) * mm, "end": v(-44.53, 64.43) * mm});
            skArc(sketch, "E70.trimOffspring", {"start": v(-48.06, 61.85) * mm, "mid": v(-49.02, 61.08) * mm, "end": v(-49.98, 60.3) * mm});
            skArc(sketch, "E71.trimOffspring", {"start": v(-53.26, 57.42) * mm, "mid": v(-54.16, 56.58) * mm, "end": v(-55.04, 55.72) * mm});
            skArc(sketch, "E72.trimOffspring", {"start": v(-78.22, -3.9) * mm, "mid": v(-78.15, -5.12) * mm, "end": v(-78.06, -6.35) * mm});
            skArc(sketch, "E73.trimOffspring", {"start": v(-77.71, 9.75) * mm, "mid": v(-77.86, 8.53) * mm, "end": v(-77.98, 7.3) * mm});
            skArc(sketch, "E74.trimOffspring", {"start": v(-78.27, 2.94) * mm, "mid": v(-78.3, 1.7) * mm, "end": v(-78.32, 0.48) * mm});
            skArc(sketch, "E75.trimOffspring", {"start": v(-76.57, 16.49) * mm, "mid": v(-76.82, 15.28) * mm, "end": v(-77.05, 14.07) * mm});
            skArc(sketch, "E76.trimOffspring", {"start": v(-74.84, 23.1) * mm, "mid": v(-75.2, 21.92) * mm, "end": v(-75.53, 20.73) * mm});
            skArc(sketch, "E77.trimOffspring", {"start": v(-72.54, 29.53) * mm, "mid": v(-73, 28.39) * mm, "end": v(-73.43, 27.23) * mm});
            skArc(sketch, "E78.trimOffspring", {"start": v(-69.7, 35.74) * mm, "mid": v(-70.24, 34.64) * mm, "end": v(-70.78, 33.53) * mm});
            skArc(sketch, "E79.trimOffspring", {"start": v(-66.3, 41.68) * mm, "mid": v(-66.96, 40.63) * mm, "end": v(-67.59, 39.57) * mm});
            skArc(sketch, "E80.trimOffspring", {"start": v(-58.06, 52.56) * mm, "mid": v(-58.88, 51.64) * mm, "end": v(-59.7, 50.7) * mm});
            skArc(sketch, "E81.trimOffspring", {"start": v(-62.42, 47.3) * mm, "mid": v(-63.16, 46.31) * mm, "end": v(-63.88, 45.31) * mm});
            skArc(sketch, "E82.trimOffspring", {"start": v(3.9, -78.22) * mm, "mid": v(5.12, -78.15) * mm, "end": v(6.35, -78.06) * mm});
            skArc(sketch, "E83.trimOffspring", {"start": v(-2.94, -78.27) * mm, "mid": v(-1.7, -78.3) * mm, "end": v(-0.48, -78.32) * mm});
            skArc(sketch, "E84.trimOffspring", {"start": v(-9.75, -77.71) * mm, "mid": v(-8.53, -77.86) * mm, "end": v(-7.3, -77.98) * mm});
            skArc(sketch, "E85.trimOffspring", {"start": v(69.7, -35.74) * mm, "mid": v(70.24, -34.64) * mm, "end": v(70.78, -33.53) * mm});
            skArc(sketch, "E86.trimOffspring", {"start": v(66.3, -41.68) * mm, "mid": v(66.96, -40.63) * mm, "end": v(67.59, -39.57) * mm});
            skCircle(sketch, "E87", {"center": v(0, 0) * mm, "radius": 84.92 * mm});
            skSolve(sketch);
        }
        {
            var Q0;
            Q0 = qSketchRegion(id + "F0", true);
            extrude(context, id + "F1", {"entities" : qUnion([Q0]), "depth" : 25.4 * mm});
        }
        {
            var Q0;
            Q0=makeQuery(id+"F1.opExtrude","CAP_FACE",FACE,{"disambiguationData":[OSD([sQuery(id+"F0.wireOp",EDGE,"E0"),sQuery(id+"F0.wireOp",EDGE,"E1.MirrorCS"),sQuery(id+"F0.wireOp",EDGE,"E3"),sQuery(id+"F0.wireOp",EDGE,"E4"),sQuery(id+"F0.wireOp",EDGE,"E5.MirrorCS"),sQuery(id+"F0.wireOp",EDGE,"E6.MirrorCS"),sQuery(id+"F0.wireOp",EDGE,"E7.MirrorCS"),sQuery(id+"F0.wireOp",EDGE,"E9.filletArc"),sQuery(id+"F0.wireOp",EDGE,"E10.filletArc"),sQuery(id+"F0.wireOp",EDGE,"E11.filletArc"),sQuery(id+"F0.wireOp",EDGE,"E12.filletArc"),sQuery(id+"F0.wireOp",EDGE,"E13.filletArc"),sQuery(id+"F0.wireOp",EDGE,"E14.filletArc"),sQuery(id+"F0.wireOp",EDGE,"E15.1.0"),sQuery(id+"F0.wireOp",EDGE,"E15.1.1"),sQuery(id+"F0.wireOp",EDGE,"E15.1.2"),sQuery(id+"F0.wireOp",EDGE,"E15.1.3"),sQuery(id+"F0.wireOp",EDGE,"E15.1.4"),sQuery(id+"F0.wireOp",EDGE,"E15.1.5"),sQuery(id+"F0.wireOp",EDGE,"E15.1.6"),sQuery(id+"F0.wireOp",EDGE,"E15.1.7"),sQuery(id+"F0.wireOp",EDGE,"E15.1.8"),sQuery(id+"F0.wireOp",EDGE,"E15.1.9"),sQuery(id+"F0.wireOp",EDGE,"E15.1.10"),sQuery(id+"F0.wireOp",EDGE,"E15.1.11"),sQuery(id+"F0.wireOp",EDGE,"E15.2.0"),sQuery(id+"F0.wireOp",EDGE,"E15.2.1"),sQuery(id+"F0.wireOp",EDGE,"E15.2.2"),sQuery(id+"F0.wireOp",EDGE,"E15.2.3"),sQuery(id+"F0.wireOp",EDGE,"E15.2.4"),sQuery(id+"F0.wireOp",EDGE,"E15.2.5"),sQuery(id+"F0.wireOp",EDGE,"E15.2.6"),sQuery(id+"F0.wireOp",EDGE,"E15.2.7"),sQuery(id+"F0.wireOp",EDGE,"E15.2.8"),sQuery(id+"F0.wireOp",EDGE,"E15.2.9"),sQuery(id+"F0.wireOp",EDGE,"E15.2.10"),sQuery(id+"F0.wireOp",EDGE,"E15.2.11"),sQuery(id+"F0.wireOp",EDGE,"E15.3.0"),sQuery(id+"F0.wireOp",EDGE,"E15.3.1"),sQuery(id+"F0.wireOp",EDGE,"E15.3.2"),sQuery(id+"F0.wireOp",EDGE,"E15.3.3"),sQuery(id+"F0.wireOp",EDGE,"E15.3.4"),sQuery(id+"F0.wireOp",EDGE,"E15.3.5"),sQuery(id+"F0.wireOp",EDGE,"E15.3.6"),sQuery(id+"F0.wireOp",EDGE,"E15.3.7"),sQuery(id+"F0.wireOp",EDGE,"E15.3.8"),sQuery(id+"F0.wireOp",EDGE,"E15.3.9"),sQuery(id+"F0.wireOp",EDGE,"E15.3.10"),sQuery(id+"F0.wireOp",EDGE,"E15.3.11"),sQuery(id+"F0.wireOp",EDGE,"E15.4.0"),sQuery(id+"F0.wireOp",EDGE,"E15.4.1"),sQuery(id+"F0.wireOp",EDGE,"E15.4.2"),sQuery(id+"F0.wireOp",EDGE,"E15.4.3"),sQuery(id+"F0.wireOp",EDGE,"E15.4.4"),sQuery(id+"F0.wireOp",EDGE,"E15.4.5"),sQuery(id+"F0.wireOp",EDGE,"E15.4.6"),sQuery(id+"F0.wireOp",EDGE,"E15.4.7"),sQuery(id+"F0.wireOp",EDGE,"E15.4.8"),sQuery(id+"F0.wireOp",EDGE,"E15.4.9"),sQuery(id+"F0.wireOp",EDGE,"E15.4.10"),sQuery(id+"F0.wireOp",EDGE,"E15.4.11"),sQuery(id+"F0.wireOp",EDGE,"E15.5.0"),sQuery(id+"F0.wireOp",EDGE,"E15.5.1"),sQuery(id+"F0.wireOp",EDGE,"E15.5.2"),sQuery(id+"F0.wireOp",EDGE,"E15.5.3"),sQuery(id+"F0.wireOp",EDGE,"E15.5.4"),sQuery(id+"F0.wireOp",EDGE,"E15.5.5"),sQuery(id+"F0.wireOp",EDGE,"E15.5.6"),sQuery(id+"F0.wireOp",EDGE,"E15.5.7"),sQuery(id+"F0.wireOp",EDGE,"E15.5.8"),sQuery(id+"F0.wireOp",EDGE,"E15.5.9"),sQuery(id+"F0.wireOp",EDGE,"E15.5.10"),sQuery(id+"F0.wireOp",EDGE,"E15.5.11"),sQuery(id+"F0.wireOp",EDGE,"E15.6.0"),sQuery(id+"F0.wireOp",EDGE,"E15.6.1"),sQuery(id+"F0.wireOp",EDGE,"E15.6.2"),sQuery(id+"F0.wireOp",EDGE,"E15.6.3"),sQuery(id+"F0.wireOp",EDGE,"E15.6.4"),sQuery(id+"F0.wireOp",EDGE,"E15.6.5"),sQuery(id+"F0.wireOp",EDGE,"E15.6.6"),sQuery(id+"F0.wireOp",EDGE,"E15.6.7"),sQuery(id+"F0.wireOp",EDGE,"E15.6.8"),sQuery(id+"F0.wireOp",EDGE,"E15.6.9"),sQuery(id+"F0.wireOp",EDGE,"E15.6.10"),sQuery(id+"F0.wireOp",EDGE,"E15.6.11"),sQuery(id+"F0.wireOp",EDGE,"E15.7.0"),sQuery(id+"F0.wireOp",EDGE,"E15.7.1"),sQuery(id+"F0.wireOp",EDGE,"E15.7.2"),sQuery(id+"F0.wireOp",EDGE,"E15.7.3"),sQuery(id+"F0.wireOp",EDGE,"E15.7.4"),sQuery(id+"F0.wireOp",EDGE,"E15.7.5"),sQuery(id+"F0.wireOp",EDGE,"E15.7.6"),sQuery(id+"F0.wireOp",EDGE,"E15.7.7"),sQuery(id+"F0.wireOp",EDGE,"E15.7.8"),sQuery(id+"F0.wireOp",EDGE,"E15.7.9"),sQuery(id+"F0.wireOp",EDGE,"E15.7.10"),sQuery(id+"F0.wireOp",EDGE,"E15.7.11"),sQuery(id+"F0.wireOp",EDGE,"E15.8.0"),sQuery(id+"F0.wireOp",EDGE,"E15.8.1"),sQuery(id+"F0.wireOp",EDGE,"E15.8.2"),sQuery(id+"F0.wireOp",EDGE,"E15.8.3"),sQuery(id+"F0.wireOp",EDGE,"E15.8.4"),sQuery(id+"F0.wireOp",EDGE,"E15.8.5"),sQuery(id+"F0.wireOp",EDGE,"E15.8.6"),sQuery(id+"F0.wireOp",EDGE,"E15.8.7"),sQuery(id+"F0.wireOp",EDGE,"E15.8.8"),sQuery(id+"F0.wireOp",EDGE,"E15.8.9"),sQuery(id+"F0.wireOp",EDGE,"E15.8.10"),sQuery(id+"F0.wireOp",EDGE,"E15.8.11"),sQuery(id+"F0.wireOp",EDGE,"E15.9.0"),sQuery(id+"F0.wireOp",EDGE,"E15.9.1"),sQuery(id+"F0.wireOp",EDGE,"E15.9.2"),sQuery(id+"F0.wireOp",EDGE,"E15.9.3"),sQuery(id+"F0.wireOp",EDGE,"E15.9.4"),sQuery(id+"F0.wireOp",EDGE,"E15.9.5"),sQuery(id+"F0.wireOp",EDGE,"E15.9.6"),sQuery(id+"F0.wireOp",EDGE,"E15.9.7"),sQuery(id+"F0.wireOp",EDGE,"E15.9.8"),sQuery(id+"F0.wireOp",EDGE,"E15.9.9"),sQuery(id+"F0.wireOp",EDGE,"E15.9.10"),sQuery(id+"F0.wireOp",EDGE,"E15.9.11"),sQuery(id+"F0.wireOp",EDGE,"E15.10.0"),sQuery(id+"F0.wireOp",EDGE,"E15.10.1"),sQuery(id+"F0.wireOp",EDGE,"E15.10.2"),sQuery(id+"F0.wireOp",EDGE,"E15.10.3"),sQuery(id+"F0.wireOp",EDGE,"E15.10.4"),sQuery(id+"F0.wireOp",EDGE,"E15.10.5"),sQuery(id+"F0.wireOp",EDGE,"E15.10.6"),sQuery(id+"F0.wireOp",EDGE,"E15.10.7"),sQuery(id+"F0.wireOp",EDGE,"E15.10.8"),sQuery(id+"F0.wireOp",EDGE,"E15.10.9"),sQuery(id+"F0.wireOp",EDGE,"E15.10.10"),sQuery(id+"F0.wireOp",EDGE,"E15.10.11"),sQuery(id+"F0.wireOp",EDGE,"E15.11.0"),sQuery(id+"F0.wireOp",EDGE,"E15.11.1"),sQuery(id+"F0.wireOp",EDGE,"E15.11.2"),sQuery(id+"F0.wireOp",EDGE,"E15.11.3"),sQuery(id+"F0.wireOp",EDGE,"E15.11.4"),sQuery(id+"F0.wireOp",EDGE,"E15.11.5"),sQuery(id+"F0.wireOp",EDGE,"E15.11.6"),sQuery(id+"F0.wireOp",EDGE,"E15.11.7"),sQuery(id+"F0.wireOp",EDGE,"E15.11.8"),sQuery(id+"F0.wireOp",EDGE,"E15.11.9"),sQuery(id+"F0.wireOp",EDGE,"E15.11.10"),sQuery(id+"F0.wireOp",EDGE,"E15.11.11"),sQuery(id+"F0.wireOp",EDGE,"E15.12.0"),sQuery(id+"F0.wireOp",EDGE,"E15.12.1"),sQuery(id+"F0.wireOp",EDGE,"E15.12.2"),sQuery(id+"F0.wireOp",EDGE,"E15.12.3"),sQuery(id+"F0.wireOp",EDGE,"E15.12.4"),sQuery(id+"F0.wireOp",EDGE,"E15.12.5"),sQuery(id+"F0.wireOp",EDGE,"E15.12.6"),sQuery(id+"F0.wireOp",EDGE,"E15.12.7"),sQuery(id+"F0.wireOp",EDGE,"E15.12.8"),sQuery(id+"F0.wireOp",EDGE,"E15.12.9"),sQuery(id+"F0.wireOp",EDGE,"E15.12.10"),sQuery(id+"F0.wireOp",EDGE,"E15.12.11"),sQuery(id+"F0.wireOp",EDGE,"E15.13.0"),sQuery(id+"F0.wireOp",EDGE,"E15.13.1"),sQuery(id+"F0.wireOp",EDGE,"E15.13.2"),sQuery(id+"F0.wireOp",EDGE,"E15.13.3"),sQuery(id+"F0.wireOp",EDGE,"E15.13.4"),sQuery(id+"F0.wireOp",EDGE,"E15.13.5"),sQuery(id+"F0.wireOp",EDGE,"E15.13.6"),sQuery(id+"F0.wireOp",EDGE,"E15.13.7"),sQuery(id+"F0.wireOp",EDGE,"E15.13.8"),sQuery(id+"F0.wireOp",EDGE,"E15.13.9"),sQuery(id+"F0.wireOp",EDGE,"E15.13.10"),sQuery(id+"F0.wireOp",EDGE,"E15.13.11"),sQuery(id+"F0.wireOp",EDGE,"E15.14.0"),sQuery(id+"F0.wireOp",EDGE,"E15.14.1"),sQuery(id+"F0.wireOp",EDGE,"E15.14.2"),sQuery(id+"F0.wireOp",EDGE,"E15.14.3"),sQuery(id+"F0.wireOp",EDGE,"E15.14.4"),sQuery(id+"F0.wireOp",EDGE,"E15.14.5"),sQuery(id+"F0.wireOp",EDGE,"E15.14.6"),sQuery(id+"F0.wireOp",EDGE,"E15.14.7"),sQuery(id+"F0.wireOp",EDGE,"E15.14.8"),sQuery(id+"F0.wireOp",EDGE,"E15.14.9"),sQuery(id+"F0.wireOp",EDGE,"E15.14.10"),sQuery(id+"F0.wireOp",EDGE,"E15.14.11"),sQuery(id+"F0.wireOp",EDGE,"E15.15.0"),sQuery(id+"F0.wireOp",EDGE,"E15.15.1"),sQuery(id+"F0.wireOp",EDGE,"E15.15.2"),sQuery(id+"F0.wireOp",EDGE,"E15.15.3"),sQuery(id+"F0.wireOp",EDGE,"E15.15.4"),sQuery(id+"F0.wireOp",EDGE,"E15.15.5"),sQuery(id+"F0.wireOp",EDGE,"E15.15.6"),sQuery(id+"F0.wireOp",EDGE,"E15.15.7"),sQuery(id+"F0.wireOp",EDGE,"E15.15.8"),sQuery(id+"F0.wireOp",EDGE,"E15.15.9"),sQuery(id+"F0.wireOp",EDGE,"E15.15.10"),sQuery(id+"F0.wireOp",EDGE,"E15.15.11"),sQuery(id+"F0.wireOp",EDGE,"E15.16.0"),sQuery(id+"F0.wireOp",EDGE,"E15.16.1"),sQuery(id+"F0.wireOp",EDGE,"E15.16.2"),sQuery(id+"F0.wireOp",EDGE,"E15.16.3"),sQuery(id+"F0.wireOp",EDGE,"E15.16.4"),sQuery(id+"F0.wireOp",EDGE,"E15.16.5"),sQuery(id+"F0.wireOp",EDGE,"E15.16.6"),sQuery(id+"F0.wireOp",EDGE,"E15.16.7"),sQuery(id+"F0.wireOp",EDGE,"E15.16.8"),sQuery(id+"F0.wireOp",EDGE,"E15.16.9"),sQuery(id+"F0.wireOp",EDGE,"E15.16.10"),sQuery(id+"F0.wireOp",EDGE,"E15.16.11"),sQuery(id+"F0.wireOp",EDGE,"E15.17.0"),sQuery(id+"F0.wireOp",EDGE,"E15.17.1"),sQuery(id+"F0.wireOp",EDGE,"E15.17.2"),sQuery(id+"F0.wireOp",EDGE,"E15.17.3"),sQuery(id+"F0.wireOp",EDGE,"E15.17.4"),sQuery(id+"F0.wireOp",EDGE,"E15.17.5"),sQuery(id+"F0.wireOp",EDGE,"E15.17.6"),sQuery(id+"F0.wireOp",EDGE,"E15.17.7"),sQuery(id+"F0.wireOp",EDGE,"E15.17.8"),sQuery(id+"F0.wireOp",EDGE,"E15.17.9"),sQuery(id+"F0.wireOp",EDGE,"E15.17.10"),sQuery(id+"F0.wireOp",EDGE,"E15.17.11"),sQuery(id+"F0.wireOp",EDGE,"E15.18.0"),sQuery(id+"F0.wireOp",EDGE,"E15.18.1"),sQuery(id+"F0.wireOp",EDGE,"E15.18.2"),sQuery(id+"F0.wireOp",EDGE,"E15.18.3"),sQuery(id+"F0.wireOp",EDGE,"E15.18.4"),sQuery(id+"F0.wireOp",EDGE,"E15.18.5"),sQuery(id+"F0.wireOp",EDGE,"E15.18.6"),sQuery(id+"F0.wireOp",EDGE,"E15.18.7"),sQuery(id+"F0.wireOp",EDGE,"E15.18.8"),sQuery(id+"F0.wireOp",EDGE,"E15.18.9"),sQuery(id+"F0.wireOp",EDGE,"E15.18.10"),sQuery(id+"F0.wireOp",EDGE,"E15.18.11"),sQuery(id+"F0.wireOp",EDGE,"E15.19.0"),sQuery(id+"F0.wireOp",EDGE,"E15.19.1"),sQuery(id+"F0.wireOp",EDGE,"E15.19.2"),sQuery(id+"F0.wireOp",EDGE,"E15.19.3"),sQuery(id+"F0.wireOp",EDGE,"E15.19.4"),sQuery(id+"F0.wireOp",EDGE,"E15.19.5"),sQuery(id+"F0.wireOp",EDGE,"E15.19.6"),sQuery(id+"F0.wireOp",EDGE,"E15.19.7"),sQuery(id+"F0.wireOp",EDGE,"E15.19.8"),sQuery(id+"F0.wireOp",EDGE,"E15.19.9"),sQuery(id+"F0.wireOp",EDGE,"E15.19.10"),sQuery(id+"F0.wireOp",EDGE,"E15.19.11"),sQuery(id+"F0.wireOp",EDGE,"E15.20.0"),sQuery(id+"F0.wireOp",EDGE,"E15.20.1"),sQuery(id+"F0.wireOp",EDGE,"E15.20.2"),sQuery(id+"F0.wireOp",EDGE,"E15.20.3"),sQuery(id+"F0.wireOp",EDGE,"E15.20.4"),sQuery(id+"F0.wireOp",EDGE,"E15.20.5"),sQuery(id+"F0.wireOp",EDGE,"E15.20.6"),sQuery(id+"F0.wireOp",EDGE,"E15.20.7"),sQuery(id+"F0.wireOp",EDGE,"E15.20.8"),sQuery(id+"F0.wireOp",EDGE,"E15.20.9"),sQuery(id+"F0.wireOp",EDGE,"E15.20.10"),sQuery(id+"F0.wireOp",EDGE,"E15.20.11"),sQuery(id+"F0.wireOp",EDGE,"E15.21.0"),sQuery(id+"F0.wireOp",EDGE,"E15.21.1"),sQuery(id+"F0.wireOp",EDGE,"E15.21.2"),sQuery(id+"F0.wireOp",EDGE,"E15.21.3"),sQuery(id+"F0.wireOp",EDGE,"E15.21.4"),sQuery(id+"F0.wireOp",EDGE,"E15.21.5"),sQuery(id+"F0.wireOp",EDGE,"E15.21.6"),sQuery(id+"F0.wireOp",EDGE,"E15.21.7"),sQuery(id+"F0.wireOp",EDGE,"E15.21.8"),sQuery(id+"F0.wireOp",EDGE,"E15.21.9"),sQuery(id+"F0.wireOp",EDGE,"E15.21.10"),sQuery(id+"F0.wireOp",EDGE,"E15.21.11"),sQuery(id+"F0.wireOp",EDGE,"E15.22.0"),sQuery(id+"F0.wireOp",EDGE,"E15.22.1"),sQuery(id+"F0.wireOp",EDGE,"E15.22.2"),sQuery(id+"F0.wireOp",EDGE,"E15.22.3"),sQuery(id+"F0.wireOp",EDGE,"E15.22.4"),sQuery(id+"F0.wireOp",EDGE,"E15.22.5"),sQuery(id+"F0.wireOp",EDGE,"E15.22.6"),sQuery(id+"F0.wireOp",EDGE,"E15.22.7"),sQuery(id+"F0.wireOp",EDGE,"E15.22.8"),sQuery(id+"F0.wireOp",EDGE,"E15.22.9"),sQuery(id+"F0.wireOp",EDGE,"E15.22.10"),sQuery(id+"F0.wireOp",EDGE,"E15.22.11"),sQuery(id+"F0.wireOp",EDGE,"E15.23.0"),sQuery(id+"F0.wireOp",EDGE,"E15.23.1"),sQuery(id+"F0.wireOp",EDGE,"E15.23.2"),sQuery(id+"F0.wireOp",EDGE,"E15.23.3"),sQuery(id+"F0.wireOp",EDGE,"E15.23.4"),sQuery(id+"F0.wireOp",EDGE,"E15.23.5"),sQuery(id+"F0.wireOp",EDGE,"E15.23.6"),sQuery(id+"F0.wireOp",EDGE,"E15.23.7"),sQuery(id+"F0.wireOp",EDGE,"E15.23.8"),sQuery(id+"F0.wireOp",EDGE,"E15.23.9"),sQuery(id+"F0.wireOp",EDGE,"E15.23.10"),sQuery(id+"F0.wireOp",EDGE,"E15.23.11"),sQuery(id+"F0.wireOp",EDGE,"E15.24.0"),sQuery(id+"F0.wireOp",EDGE,"E15.24.1"),sQuery(id+"F0.wireOp",EDGE,"E15.24.2"),sQuery(id+"F0.wireOp",EDGE,"E15.24.3"),sQuery(id+"F0.wireOp",EDGE,"E15.24.4"),sQuery(id+"F0.wireOp",EDGE,"E15.24.5"),sQuery(id+"F0.wireOp",EDGE,"E15.24.6"),sQuery(id+"F0.wireOp",EDGE,"E15.24.7"),sQuery(id+"F0.wireOp",EDGE,"E15.24.8"),sQuery(id+"F0.wireOp",EDGE,"E15.24.9"),sQuery(id+"F0.wireOp",EDGE,"E15.24.10"),sQuery(id+"F0.wireOp",EDGE,"E15.24.11"),sQuery(id+"F0.wireOp",EDGE,"E15.25.0"),sQuery(id+"F0.wireOp",EDGE,"E15.25.1"),sQuery(id+"F0.wireOp",EDGE,"E15.25.2"),sQuery(id+"F0.wireOp",EDGE,"E15.25.3"),sQuery(id+"F0.wireOp",EDGE,"E15.25.4"),sQuery(id+"F0.wireOp",EDGE,"E15.25.5"),sQuery(id+"F0.wireOp",EDGE,"E15.25.6"),sQuery(id+"F0.wireOp",EDGE,"E15.25.7"),sQuery(id+"F0.wireOp",EDGE,"E15.25.8"),sQuery(id+"F0.wireOp",EDGE,"E15.25.9"),sQuery(id+"F0.wireOp",EDGE,"E15.25.10"),sQuery(id+"F0.wireOp",EDGE,"E15.25.11"),sQuery(id+"F0.wireOp",EDGE,"E15.26.0"),sQuery(id+"F0.wireOp",EDGE,"E15.26.1"),sQuery(id+"F0.wireOp",EDGE,"E15.26.2"),sQuery(id+"F0.wireOp",EDGE,"E15.26.3"),sQuery(id+"F0.wireOp",EDGE,"E15.26.4"),sQuery(id+"F0.wireOp",EDGE,"E15.26.5"),sQuery(id+"F0.wireOp",EDGE,"E15.26.6"),sQuery(id+"F0.wireOp",EDGE,"E15.26.7"),sQuery(id+"F0.wireOp",EDGE,"E15.26.8"),sQuery(id+"F0.wireOp",EDGE,"E15.26.9"),sQuery(id+"F0.wireOp",EDGE,"E15.26.10"),sQuery(id+"F0.wireOp",EDGE,"E15.26.11"),sQuery(id+"F0.wireOp",EDGE,"E15.27.0"),sQuery(id+"F0.wireOp",EDGE,"E15.27.1"),sQuery(id+"F0.wireOp",EDGE,"E15.27.2"),sQuery(id+"F0.wireOp",EDGE,"E15.27.3"),sQuery(id+"F0.wireOp",EDGE,"E15.27.4"),sQuery(id+"F0.wireOp",EDGE,"E15.27.5"),sQuery(id+"F0.wireOp",EDGE,"E15.27.6"),sQuery(id+"F0.wireOp",EDGE,"E15.27.7"),sQuery(id+"F0.wireOp",EDGE,"E15.27.8"),sQuery(id+"F0.wireOp",EDGE,"E15.27.9"),sQuery(id+"F0.wireOp",EDGE,"E15.27.10"),sQuery(id+"F0.wireOp",EDGE,"E15.27.11"),sQuery(id+"F0.wireOp",EDGE,"E15.28.0"),sQuery(id+"F0.wireOp",EDGE,"E15.28.1"),sQuery(id+"F0.wireOp",EDGE,"E15.28.2"),sQuery(id+"F0.wireOp",EDGE,"E15.28.3"),sQuery(id+"F0.wireOp",EDGE,"E15.28.4"),sQuery(id+"F0.wireOp",EDGE,"E15.28.5"),sQuery(id+"F0.wireOp",EDGE,"E15.28.6"),sQuery(id+"F0.wireOp",EDGE,"E15.28.7"),sQuery(id+"F0.wireOp",EDGE,"E15.28.8"),sQuery(id+"F0.wireOp",EDGE,"E15.28.9"),sQuery(id+"F0.wireOp",EDGE,"E15.28.10"),sQuery(id+"F0.wireOp",EDGE,"E15.28.11"),sQuery(id+"F0.wireOp",EDGE,"E15.29.0"),sQuery(id+"F0.wireOp",EDGE,"E15.29.1"),sQuery(id+"F0.wireOp",EDGE,"E15.29.2"),sQuery(id+"F0.wireOp",EDGE,"E15.29.3"),sQuery(id+"F0.wireOp",EDGE,"E15.29.4"),sQuery(id+"F0.wireOp",EDGE,"E15.29.5"),sQuery(id+"F0.wireOp",EDGE,"E15.29.6"),sQuery(id+"F0.wireOp",EDGE,"E15.29.7"),sQuery(id+"F0.wireOp",EDGE,"E15.29.8"),sQuery(id+"F0.wireOp",EDGE,"E15.29.9"),sQuery(id+"F0.wireOp",EDGE,"E15.29.10"),sQuery(id+"F0.wireOp",EDGE,"E15.29.11"),sQuery(id+"F0.wireOp",EDGE,"E15.30.0"),sQuery(id+"F0.wireOp",EDGE,"E15.30.1"),sQuery(id+"F0.wireOp",EDGE,"E15.30.2"),sQuery(id+"F0.wireOp",EDGE,"E15.30.3"),sQuery(id+"F0.wireOp",EDGE,"E15.30.4"),sQuery(id+"F0.wireOp",EDGE,"E15.30.5"),sQuery(id+"F0.wireOp",EDGE,"E15.30.6"),sQuery(id+"F0.wireOp",EDGE,"E15.30.7"),sQuery(id+"F0.wireOp",EDGE,"E15.30.8"),sQuery(id+"F0.wireOp",EDGE,"E15.30.9"),sQuery(id+"F0.wireOp",EDGE,"E15.30.10"),sQuery(id+"F0.wireOp",EDGE,"E15.30.11"),sQuery(id+"F0.wireOp",EDGE,"E15.31.0"),sQuery(id+"F0.wireOp",EDGE,"E15.31.1"),sQuery(id+"F0.wireOp",EDGE,"E15.31.2"),sQuery(id+"F0.wireOp",EDGE,"E15.31.3"),sQuery(id+"F0.wireOp",EDGE,"E15.31.4"),sQuery(id+"F0.wireOp",EDGE,"E15.31.5"),sQuery(id+"F0.wireOp",EDGE,"E15.31.6"),sQuery(id+"F0.wireOp",EDGE,"E15.31.7"),sQuery(id+"F0.wireOp",EDGE,"E15.31.8"),sQuery(id+"F0.wireOp",EDGE,"E15.31.9"),sQuery(id+"F0.wireOp",EDGE,"E15.31.10"),sQuery(id+"F0.wireOp",EDGE,"E15.31.11"),sQuery(id+"F0.wireOp",EDGE,"E15.32.0"),sQuery(id+"F0.wireOp",EDGE,"E15.32.1"),sQuery(id+"F0.wireOp",EDGE,"E15.32.2"),sQuery(id+"F0.wireOp",EDGE,"E15.32.3"),sQuery(id+"F0.wireOp",EDGE,"E15.32.4"),sQuery(id+"F0.wireOp",EDGE,"E15.32.5"),sQuery(id+"F0.wireOp",EDGE,"E15.32.6"),sQuery(id+"F0.wireOp",EDGE,"E15.32.7"),sQuery(id+"F0.wireOp",EDGE,"E15.32.8"),sQuery(id+"F0.wireOp",EDGE,"E15.32.9"),sQuery(id+"F0.wireOp",EDGE,"E15.32.10"),sQuery(id+"F0.wireOp",EDGE,"E15.32.11"),sQuery(id+"F0.wireOp",EDGE,"E15.33.0"),sQuery(id+"F0.wireOp",EDGE,"E15.33.1"),sQuery(id+"F0.wireOp",EDGE,"E15.33.2"),sQuery(id+"F0.wireOp",EDGE,"E15.33.3"),sQuery(id+"F0.wireOp",EDGE,"E15.33.4"),sQuery(id+"F0.wireOp",EDGE,"E15.33.5"),sQuery(id+"F0.wireOp",EDGE,"E15.33.6"),sQuery(id+"F0.wireOp",EDGE,"E15.33.7"),sQuery(id+"F0.wireOp",EDGE,"E15.33.8"),sQuery(id+"F0.wireOp",EDGE,"E15.33.9"),sQuery(id+"F0.wireOp",EDGE,"E15.33.10"),sQuery(id+"F0.wireOp",EDGE,"E15.33.11"),sQuery(id+"F0.wireOp",EDGE,"E15.34.0"),sQuery(id+"F0.wireOp",EDGE,"E15.34.1"),sQuery(id+"F0.wireOp",EDGE,"E15.34.2"),sQuery(id+"F0.wireOp",EDGE,"E15.34.3"),sQuery(id+"F0.wireOp",EDGE,"E15.34.4"),sQuery(id+"F0.wireOp",EDGE,"E15.34.5"),sQuery(id+"F0.wireOp",EDGE,"E15.34.6"),sQuery(id+"F0.wireOp",EDGE,"E15.34.7"),sQuery(id+"F0.wireOp",EDGE,"E15.34.8"),sQuery(id+"F0.wireOp",EDGE,"E15.34.9"),sQuery(id+"F0.wireOp",EDGE,"E15.34.10"),sQuery(id+"F0.wireOp",EDGE,"E15.34.11"),sQuery(id+"F0.wireOp",EDGE,"E15.35.0"),sQuery(id+"F0.wireOp",EDGE,"E15.35.1"),sQuery(id+"F0.wireOp",EDGE,"E15.35.2"),sQuery(id+"F0.wireOp",EDGE,"E15.35.3"),sQuery(id+"F0.wireOp",EDGE,"E15.35.4"),sQuery(id+"F0.wireOp",EDGE,"E15.35.5"),sQuery(id+"F0.wireOp",EDGE,"E15.35.6"),sQuery(id+"F0.wireOp",EDGE,"E15.35.7"),sQuery(id+"F0.wireOp",EDGE,"E15.35.8"),sQuery(id+"F0.wireOp",EDGE,"E15.35.9"),sQuery(id+"F0.wireOp",EDGE,"E15.35.10"),sQuery(id+"F0.wireOp",EDGE,"E15.35.11"),sQuery(id+"F0.wireOp",EDGE,"E15.36.0"),sQuery(id+"F0.wireOp",EDGE,"E15.36.1"),sQuery(id+"F0.wireOp",EDGE,"E15.36.2"),sQuery(id+"F0.wireOp",EDGE,"E15.36.3"),sQuery(id+"F0.wireOp",EDGE,"E15.36.4"),sQuery(id+"F0.wireOp",EDGE,"E15.36.5"),sQuery(id+"F0.wireOp",EDGE,"E15.36.6"),sQuery(id+"F0.wireOp",EDGE,"E15.36.7"),sQuery(id+"F0.wireOp",EDGE,"E15.36.8"),sQuery(id+"F0.wireOp",EDGE,"E15.36.9"),sQuery(id+"F0.wireOp",EDGE,"E15.36.10"),sQuery(id+"F0.wireOp",EDGE,"E15.36.11"),sQuery(id+"F0.wireOp",EDGE,"E15.37.0"),sQuery(id+"F0.wireOp",EDGE,"E15.37.1"),sQuery(id+"F0.wireOp",EDGE,"E15.37.2"),sQuery(id+"F0.wireOp",EDGE,"E15.37.3"),sQuery(id+"F0.wireOp",EDGE,"E15.37.4"),sQuery(id+"F0.wireOp",EDGE,"E15.37.5"),sQuery(id+"F0.wireOp",EDGE,"E15.37.6"),sQuery(id+"F0.wireOp",EDGE,"E15.37.7"),sQuery(id+"F0.wireOp",EDGE,"E15.37.8"),sQuery(id+"F0.wireOp",EDGE,"E15.37.9"),sQuery(id+"F0.wireOp",EDGE,"E15.37.10"),sQuery(id+"F0.wireOp",EDGE,"E15.37.11"),sQuery(id+"F0.wireOp",EDGE,"E15.38.0"),sQuery(id+"F0.wireOp",EDGE,"E15.38.1"),sQuery(id+"F0.wireOp",EDGE,"E15.38.2"),sQuery(id+"F0.wireOp",EDGE,"E15.38.3"),sQuery(id+"F0.wireOp",EDGE,"E15.38.4"),sQuery(id+"F0.wireOp",EDGE,"E15.38.5"),sQuery(id+"F0.wireOp",EDGE,"E15.38.6"),sQuery(id+"F0.wireOp",EDGE,"E15.38.7"),sQuery(id+"F0.wireOp",EDGE,"E15.38.8"),sQuery(id+"F0.wireOp",EDGE,"E15.38.9"),sQuery(id+"F0.wireOp",EDGE,"E15.38.10"),sQuery(id+"F0.wireOp",EDGE,"E15.38.11"),sQuery(id+"F0.wireOp",EDGE,"E15.39.0"),sQuery(id+"F0.wireOp",EDGE,"E15.39.1"),sQuery(id+"F0.wireOp",EDGE,"E15.39.2"),sQuery(id+"F0.wireOp",EDGE,"E15.39.3"),sQuery(id+"F0.wireOp",EDGE,"E15.39.4"),sQuery(id+"F0.wireOp",EDGE,"E15.39.5"),sQuery(id+"F0.wireOp",EDGE,"E15.39.6"),sQuery(id+"F0.wireOp",EDGE,"E15.39.7"),sQuery(id+"F0.wireOp",EDGE,"E15.39.8"),sQuery(id+"F0.wireOp",EDGE,"E15.39.9"),sQuery(id+"F0.wireOp",EDGE,"E15.39.10"),sQuery(id+"F0.wireOp",EDGE,"E15.39.11"),sQuery(id+"F0.wireOp",EDGE,"E15.40.0"),sQuery(id+"F0.wireOp",EDGE,"E15.40.1"),sQuery(id+"F0.wireOp",EDGE,"E15.40.2"),sQuery(id+"F0.wireOp",EDGE,"E15.40.3"),sQuery(id+"F0.wireOp",EDGE,"E15.40.4"),sQuery(id+"F0.wireOp",EDGE,"E15.40.5"),sQuery(id+"F0.wireOp",EDGE,"E15.40.6"),sQuery(id+"F0.wireOp",EDGE,"E15.40.7"),sQuery(id+"F0.wireOp",EDGE,"E15.40.8"),sQuery(id+"F0.wireOp",EDGE,"E15.40.9"),sQuery(id+"F0.wireOp",EDGE,"E15.40.10"),sQuery(id+"F0.wireOp",EDGE,"E15.40.11"),sQuery(id+"F0.wireOp",EDGE,"E15.41.0"),sQuery(id+"F0.wireOp",EDGE,"E15.41.1"),sQuery(id+"F0.wireOp",EDGE,"E15.41.2"),sQuery(id+"F0.wireOp",EDGE,"E15.41.3"),sQuery(id+"F0.wireOp",EDGE,"E15.41.4"),sQuery(id+"F0.wireOp",EDGE,"E15.41.5"),sQuery(id+"F0.wireOp",EDGE,"E15.41.6"),sQuery(id+"F0.wireOp",EDGE,"E15.41.7"),sQuery(id+"F0.wireOp",EDGE,"E15.41.8"),sQuery(id+"F0.wireOp",EDGE,"E15.41.9"),sQuery(id+"F0.wireOp",EDGE,"E15.41.10"),sQuery(id+"F0.wireOp",EDGE,"E15.41.11"),sQuery(id+"F0.wireOp",EDGE,"E15.42.0"),sQuery(id+"F0.wireOp",EDGE,"E15.42.1"),sQuery(id+"F0.wireOp",EDGE,"E15.42.2"),sQuery(id+"F0.wireOp",EDGE,"E15.42.3"),sQuery(id+"F0.wireOp",EDGE,"E15.42.4"),sQuery(id+"F0.wireOp",EDGE,"E15.42.5"),sQuery(id+"F0.wireOp",EDGE,"E15.42.6"),sQuery(id+"F0.wireOp",EDGE,"E15.42.7"),sQuery(id+"F0.wireOp",EDGE,"E15.42.8"),sQuery(id+"F0.wireOp",EDGE,"E15.42.9"),sQuery(id+"F0.wireOp",EDGE,"E15.42.10"),sQuery(id+"F0.wireOp",EDGE,"E15.42.11"),sQuery(id+"F0.wireOp",EDGE,"E15.43.0"),sQuery(id+"F0.wireOp",EDGE,"E15.43.1"),sQuery(id+"F0.wireOp",EDGE,"E15.43.2"),sQuery(id+"F0.wireOp",EDGE,"E15.43.3"),sQuery(id+"F0.wireOp",EDGE,"E15.43.4"),sQuery(id+"F0.wireOp",EDGE,"E15.43.5"),sQuery(id+"F0.wireOp",EDGE,"E15.43.6"),sQuery(id+"F0.wireOp",EDGE,"E15.43.7"),sQuery(id+"F0.wireOp",EDGE,"E15.43.8"),sQuery(id+"F0.wireOp",EDGE,"E15.43.9"),sQuery(id+"F0.wireOp",EDGE,"E15.43.10"),sQuery(id+"F0.wireOp",EDGE,"E15.43.11"),sQuery(id+"F0.wireOp",EDGE,"E15.44.0"),sQuery(id+"F0.wireOp",EDGE,"E15.44.1"),sQuery(id+"F0.wireOp",EDGE,"E15.44.2"),sQuery(id+"F0.wireOp",EDGE,"E15.44.3"),sQuery(id+"F0.wireOp",EDGE,"E15.44.4"),sQuery(id+"F0.wireOp",EDGE,"E15.44.5"),sQuery(id+"F0.wireOp",EDGE,"E15.44.6"),sQuery(id+"F0.wireOp",EDGE,"E15.44.7"),sQuery(id+"F0.wireOp",EDGE,"E15.44.8"),sQuery(id+"F0.wireOp",EDGE,"E15.44.9"),sQuery(id+"F0.wireOp",EDGE,"E15.44.10"),sQuery(id+"F0.wireOp",EDGE,"E15.44.11"),sQuery(id+"F0.wireOp",EDGE,"E15.45.0"),sQuery(id+"F0.wireOp",EDGE,"E15.45.1"),sQuery(id+"F0.wireOp",EDGE,"E15.45.2"),sQuery(id+"F0.wireOp",EDGE,"E15.45.3"),sQuery(id+"F0.wireOp",EDGE,"E15.45.4"),sQuery(id+"F0.wireOp",EDGE,"E15.45.5"),sQuery(id+"F0.wireOp",EDGE,"E15.45.6"),sQuery(id+"F0.wireOp",EDGE,"E15.45.7"),sQuery(id+"F0.wireOp",EDGE,"E15.45.8"),sQuery(id+"F0.wireOp",EDGE,"E15.45.9"),sQuery(id+"F0.wireOp",EDGE,"E15.45.10"),sQuery(id+"F0.wireOp",EDGE,"E15.45.11"),sQuery(id+"F0.wireOp",EDGE,"E15.46.0"),sQuery(id+"F0.wireOp",EDGE,"E15.46.1"),sQuery(id+"F0.wireOp",EDGE,"E15.46.2"),sQuery(id+"F0.wireOp",EDGE,"E15.46.3"),sQuery(id+"F0.wireOp",EDGE,"E15.46.4"),sQuery(id+"F0.wireOp",EDGE,"E15.46.5"),sQuery(id+"F0.wireOp",EDGE,"E15.46.6"),sQuery(id+"F0.wireOp",EDGE,"E15.46.7"),sQuery(id+"F0.wireOp",EDGE,"E15.46.8"),sQuery(id+"F0.wireOp",EDGE,"E15.46.9"),sQuery(id+"F0.wireOp",EDGE,"E15.46.10"),sQuery(id+"F0.wireOp",EDGE,"E15.46.11"),sQuery(id+"F0.wireOp",EDGE,"E15.47.0"),sQuery(id+"F0.wireOp",EDGE,"E15.47.1"),sQuery(id+"F0.wireOp",EDGE,"E15.47.2"),sQuery(id+"F0.wireOp",EDGE,"E15.47.3"),sQuery(id+"F0.wireOp",EDGE,"E15.47.4"),sQuery(id+"F0.wireOp",EDGE,"E15.47.5"),sQuery(id+"F0.wireOp",EDGE,"E15.47.6"),sQuery(id+"F0.wireOp",EDGE,"E15.47.7"),sQuery(id+"F0.wireOp",EDGE,"E15.47.8"),sQuery(id+"F0.wireOp",EDGE,"E15.47.9"),sQuery(id+"F0.wireOp",EDGE,"E15.47.10"),sQuery(id+"F0.wireOp",EDGE,"E15.47.11"),sQuery(id+"F0.wireOp",EDGE,"E15.48.0"),sQuery(id+"F0.wireOp",EDGE,"E15.48.1"),sQuery(id+"F0.wireOp",EDGE,"E15.48.2"),sQuery(id+"F0.wireOp",EDGE,"E15.48.3"),sQuery(id+"F0.wireOp",EDGE,"E15.48.4"),sQuery(id+"F0.wireOp",EDGE,"E15.48.5"),sQuery(id+"F0.wireOp",EDGE,"E15.48.6"),sQuery(id+"F0.wireOp",EDGE,"E15.48.7"),sQuery(id+"F0.wireOp",EDGE,"E15.48.8"),sQuery(id+"F0.wireOp",EDGE,"E15.48.9"),sQuery(id+"F0.wireOp",EDGE,"E15.48.10"),sQuery(id+"F0.wireOp",EDGE,"E15.48.11"),sQuery(id+"F0.wireOp",EDGE,"E15.49.0"),sQuery(id+"F0.wireOp",EDGE,"E15.49.1"),sQuery(id+"F0.wireOp",EDGE,"E15.49.2"),sQuery(id+"F0.wireOp",EDGE,"E15.49.3"),sQuery(id+"F0.wireOp",EDGE,"E15.49.4"),sQuery(id+"F0.wireOp",EDGE,"E15.49.5"),sQuery(id+"F0.wireOp",EDGE,"E15.49.6"),sQuery(id+"F0.wireOp",EDGE,"E15.49.7"),sQuery(id+"F0.wireOp",EDGE,"E15.49.8"),sQuery(id+"F0.wireOp",EDGE,"E15.49.9"),sQuery(id+"F0.wireOp",EDGE,"E15.49.10"),sQuery(id+"F0.wireOp",EDGE,"E15.49.11"),sQuery(id+"F0.wireOp",EDGE,"E15.50.0"),sQuery(id+"F0.wireOp",EDGE,"E15.50.1"),sQuery(id+"F0.wireOp",EDGE,"E15.50.2"),sQuery(id+"F0.wireOp",EDGE,"E15.50.3"),sQuery(id+"F0.wireOp",EDGE,"E15.50.4"),sQuery(id+"F0.wireOp",EDGE,"E15.50.5"),sQuery(id+"F0.wireOp",EDGE,"E15.50.6"),sQuery(id+"F0.wireOp",EDGE,"E15.50.7"),sQuery(id+"F0.wireOp",EDGE,"E15.50.8"),sQuery(id+"F0.wireOp",EDGE,"E15.50.9"),sQuery(id+"F0.wireOp",EDGE,"E15.50.10"),sQuery(id+"F0.wireOp",EDGE,"E15.50.11"),sQuery(id+"F0.wireOp",EDGE,"E15.51.0"),sQuery(id+"F0.wireOp",EDGE,"E15.51.1"),sQuery(id+"F0.wireOp",EDGE,"E15.51.2"),sQuery(id+"F0.wireOp",EDGE,"E15.51.3"),sQuery(id+"F0.wireOp",EDGE,"E15.51.4"),sQuery(id+"F0.wireOp",EDGE,"E15.51.5"),sQuery(id+"F0.wireOp",EDGE,"E15.51.6"),sQuery(id+"F0.wireOp",EDGE,"E15.51.7"),sQuery(id+"F0.wireOp",EDGE,"E15.51.8"),sQuery(id+"F0.wireOp",EDGE,"E15.51.9"),sQuery(id+"F0.wireOp",EDGE,"E15.51.10"),sQuery(id+"F0.wireOp",EDGE,"E15.51.11"),sQuery(id+"F0.wireOp",EDGE,"E15.52.0"),sQuery(id+"F0.wireOp",EDGE,"E15.52.1"),sQuery(id+"F0.wireOp",EDGE,"E15.52.2"),sQuery(id+"F0.wireOp",EDGE,"E15.52.3"),sQuery(id+"F0.wireOp",EDGE,"E15.52.4"),sQuery(id+"F0.wireOp",EDGE,"E15.52.5"),sQuery(id+"F0.wireOp",EDGE,"E15.52.6"),sQuery(id+"F0.wireOp",EDGE,"E15.52.7"),sQuery(id+"F0.wireOp",EDGE,"E15.52.8"),sQuery(id+"F0.wireOp",EDGE,"E15.52.9"),sQuery(id+"F0.wireOp",EDGE,"E15.52.10"),sQuery(id+"F0.wireOp",EDGE,"E15.52.11"),sQuery(id+"F0.wireOp",EDGE,"E15.53.0"),sQuery(id+"F0.wireOp",EDGE,"E15.53.1"),sQuery(id+"F0.wireOp",EDGE,"E15.53.2"),sQuery(id+"F0.wireOp",EDGE,"E15.53.3"),sQuery(id+"F0.wireOp",EDGE,"E15.53.4"),sQuery(id+"F0.wireOp",EDGE,"E15.53.5"),sQuery(id+"F0.wireOp",EDGE,"E15.53.6"),sQuery(id+"F0.wireOp",EDGE,"E15.53.7"),sQuery(id+"F0.wireOp",EDGE,"E15.53.8"),sQuery(id+"F0.wireOp",EDGE,"E15.53.9"),sQuery(id+"F0.wireOp",EDGE,"E15.53.10"),sQuery(id+"F0.wireOp",EDGE,"E15.53.11"),sQuery(id+"F0.wireOp",EDGE,"E15.54.0"),sQuery(id+"F0.wireOp",EDGE,"E15.54.1"),sQuery(id+"F0.wireOp",EDGE,"E15.54.2"),sQuery(id+"F0.wireOp",EDGE,"E15.54.3"),sQuery(id+"F0.wireOp",EDGE,"E15.54.4"),sQuery(id+"F0.wireOp",EDGE,"E15.54.5"),sQuery(id+"F0.wireOp",EDGE,"E15.54.6"),sQuery(id+"F0.wireOp",EDGE,"E15.54.7"),sQuery(id+"F0.wireOp",EDGE,"E15.54.8"),sQuery(id+"F0.wireOp",EDGE,"E15.54.9"),sQuery(id+"F0.wireOp",EDGE,"E15.54.10"),sQuery(id+"F0.wireOp",EDGE,"E15.54.11"),sQuery(id+"F0.wireOp",EDGE,"E15.55.0"),sQuery(id+"F0.wireOp",EDGE,"E15.55.1"),sQuery(id+"F0.wireOp",EDGE,"E15.55.2"),sQuery(id+"F0.wireOp",EDGE,"E15.55.3"),sQuery(id+"F0.wireOp",EDGE,"E15.55.4"),sQuery(id+"F0.wireOp",EDGE,"E15.55.5"),sQuery(id+"F0.wireOp",EDGE,"E15.55.6"),sQuery(id+"F0.wireOp",EDGE,"E15.55.7"),sQuery(id+"F0.wireOp",EDGE,"E15.55.8"),sQuery(id+"F0.wireOp",EDGE,"E15.55.9"),sQuery(id+"F0.wireOp",EDGE,"E15.55.10"),sQuery(id+"F0.wireOp",EDGE,"E15.55.11"),sQuery(id+"F0.wireOp",EDGE,"E15.56.0"),sQuery(id+"F0.wireOp",EDGE,"E15.56.1"),sQuery(id+"F0.wireOp",EDGE,"E15.56.2"),sQuery(id+"F0.wireOp",EDGE,"E15.56.3"),sQuery(id+"F0.wireOp",EDGE,"E15.56.4"),sQuery(id+"F0.wireOp",EDGE,"E15.56.5"),sQuery(id+"F0.wireOp",EDGE,"E15.56.6"),sQuery(id+"F0.wireOp",EDGE,"E15.56.7"),sQuery(id+"F0.wireOp",EDGE,"E15.56.8"),sQuery(id+"F0.wireOp",EDGE,"E15.56.9"),sQuery(id+"F0.wireOp",EDGE,"E15.56.10"),sQuery(id+"F0.wireOp",EDGE,"E15.56.11"),sQuery(id+"F0.wireOp",EDGE,"E15.57.0"),sQuery(id+"F0.wireOp",EDGE,"E15.57.1"),sQuery(id+"F0.wireOp",EDGE,"E15.57.2"),sQuery(id+"F0.wireOp",EDGE,"E15.57.3"),sQuery(id+"F0.wireOp",EDGE,"E15.57.4"),sQuery(id+"F0.wireOp",EDGE,"E15.57.5"),sQuery(id+"F0.wireOp",EDGE,"E15.57.6"),sQuery(id+"F0.wireOp",EDGE,"E15.57.7"),sQuery(id+"F0.wireOp",EDGE,"E15.57.8"),sQuery(id+"F0.wireOp",EDGE,"E15.57.9"),sQuery(id+"F0.wireOp",EDGE,"E15.57.10"),sQuery(id+"F0.wireOp",EDGE,"E15.57.11"),sQuery(id+"F0.wireOp",EDGE,"E15.58.0"),sQuery(id+"F0.wireOp",EDGE,"E15.58.1"),sQuery(id+"F0.wireOp",EDGE,"E15.58.2"),sQuery(id+"F0.wireOp",EDGE,"E15.58.3"),sQuery(id+"F0.wireOp",EDGE,"E15.58.4"),sQuery(id+"F0.wireOp",EDGE,"E15.58.5"),sQuery(id+"F0.wireOp",EDGE,"E15.58.6"),sQuery(id+"F0.wireOp",EDGE,"E15.58.7"),sQuery(id+"F0.wireOp",EDGE,"E15.58.8"),sQuery(id+"F0.wireOp",EDGE,"E15.58.9"),sQuery(id+"F0.wireOp",EDGE,"E15.58.10"),sQuery(id+"F0.wireOp",EDGE,"E15.58.11"),sQuery(id+"F0.wireOp",EDGE,"E15.59.0"),sQuery(id+"F0.wireOp",EDGE,"E15.59.1"),sQuery(id+"F0.wireOp",EDGE,"E15.59.2"),sQuery(id+"F0.wireOp",EDGE,"E15.59.3"),sQuery(id+"F0.wireOp",EDGE,"E15.59.4"),sQuery(id+"F0.wireOp",EDGE,"E15.59.5"),sQuery(id+"F0.wireOp",EDGE,"E15.59.6"),sQuery(id+"F0.wireOp",EDGE,"E15.59.7"),sQuery(id+"F0.wireOp",EDGE,"E15.59.8"),sQuery(id+"F0.wireOp",EDGE,"E15.59.9"),sQuery(id+"F0.wireOp",EDGE,"E15.59.10"),sQuery(id+"F0.wireOp",EDGE,"E15.59.11"),sQuery(id+"F0.wireOp",EDGE,"E15.60.0"),sQuery(id+"F0.wireOp",EDGE,"E15.60.1"),sQuery(id+"F0.wireOp",EDGE,"E15.60.2"),sQuery(id+"F0.wireOp",EDGE,"E15.60.3"),sQuery(id+"F0.wireOp",EDGE,"E15.60.4"),sQuery(id+"F0.wireOp",EDGE,"E15.60.5"),sQuery(id+"F0.wireOp",EDGE,"E15.60.6"),sQuery(id+"F0.wireOp",EDGE,"E15.60.7"),sQuery(id+"F0.wireOp",EDGE,"E15.60.8"),sQuery(id+"F0.wireOp",EDGE,"E15.60.9"),sQuery(id+"F0.wireOp",EDGE,"E15.60.10"),sQuery(id+"F0.wireOp",EDGE,"E15.60.11"),sQuery(id+"F0.wireOp",EDGE,"E15.61.0"),sQuery(id+"F0.wireOp",EDGE,"E15.61.1"),sQuery(id+"F0.wireOp",EDGE,"E15.61.2"),sQuery(id+"F0.wireOp",EDGE,"E15.61.3"),sQuery(id+"F0.wireOp",EDGE,"E15.61.4"),sQuery(id+"F0.wireOp",EDGE,"E15.61.5"),sQuery(id+"F0.wireOp",EDGE,"E15.61.6"),sQuery(id+"F0.wireOp",EDGE,"E15.61.7"),sQuery(id+"F0.wireOp",EDGE,"E15.61.8"),sQuery(id+"F0.wireOp",EDGE,"E15.61.9"),sQuery(id+"F0.wireOp",EDGE,"E15.61.10"),sQuery(id+"F0.wireOp",EDGE,"E15.61.11"),sQuery(id+"F0.wireOp",EDGE,"E15.62.0"),sQuery(id+"F0.wireOp",EDGE,"E15.62.1"),sQuery(id+"F0.wireOp",EDGE,"E15.62.2"),sQuery(id+"F0.wireOp",EDGE,"E15.62.3"),sQuery(id+"F0.wireOp",EDGE,"E15.62.4"),sQuery(id+"F0.wireOp",EDGE,"E15.62.5"),sQuery(id+"F0.wireOp",EDGE,"E15.62.6"),sQuery(id+"F0.wireOp",EDGE,"E15.62.7"),sQuery(id+"F0.wireOp",EDGE,"E15.62.8"),sQuery(id+"F0.wireOp",EDGE,"E15.62.9"),sQuery(id+"F0.wireOp",EDGE,"E15.62.10"),sQuery(id+"F0.wireOp",EDGE,"E15.62.11"),sQuery(id+"F0.wireOp",EDGE,"E15.63.0"),sQuery(id+"F0.wireOp",EDGE,"E15.63.1"),sQuery(id+"F0.wireOp",EDGE,"E15.63.2"),sQuery(id+"F0.wireOp",EDGE,"E15.63.3"),sQuery(id+"F0.wireOp",EDGE,"E15.63.4"),sQuery(id+"F0.wireOp",EDGE,"E15.63.5"),sQuery(id+"F0.wireOp",EDGE,"E15.63.6"),sQuery(id+"F0.wireOp",EDGE,"E15.63.7"),sQuery(id+"F0.wireOp",EDGE,"E15.63.8"),sQuery(id+"F0.wireOp",EDGE,"E15.63.9"),sQuery(id+"F0.wireOp",EDGE,"E15.63.10"),sQuery(id+"F0.wireOp",EDGE,"E15.63.11"),sQuery(id+"F0.wireOp",EDGE,"E15.64.0"),sQuery(id+"F0.wireOp",EDGE,"E15.64.1"),sQuery(id+"F0.wireOp",EDGE,"E15.64.2"),sQuery(id+"F0.wireOp",EDGE,"E15.64.3"),sQuery(id+"F0.wireOp",EDGE,"E15.64.4"),sQuery(id+"F0.wireOp",EDGE,"E15.64.5"),sQuery(id+"F0.wireOp",EDGE,"E15.64.6"),sQuery(id+"F0.wireOp",EDGE,"E15.64.7"),sQuery(id+"F0.wireOp",EDGE,"E15.64.8"),sQuery(id+"F0.wireOp",EDGE,"E15.64.9"),sQuery(id+"F0.wireOp",EDGE,"E15.64.10"),sQuery(id+"F0.wireOp",EDGE,"E15.64.11"),sQuery(id+"F0.wireOp",EDGE,"E15.65.0"),sQuery(id+"F0.wireOp",EDGE,"E15.65.1"),sQuery(id+"F0.wireOp",EDGE,"E15.65.2"),sQuery(id+"F0.wireOp",EDGE,"E15.65.3"),sQuery(id+"F0.wireOp",EDGE,"E15.65.4"),sQuery(id+"F0.wireOp",EDGE,"E15.65.5"),sQuery(id+"F0.wireOp",EDGE,"E15.65.6"),sQuery(id+"F0.wireOp",EDGE,"E15.65.7"),sQuery(id+"F0.wireOp",EDGE,"E15.65.8"),sQuery(id+"F0.wireOp",EDGE,"E15.65.9"),sQuery(id+"F0.wireOp",EDGE,"E15.65.10"),sQuery(id+"F0.wireOp",EDGE,"E15.65.11"),sQuery(id+"F0.wireOp",EDGE,"E15.66.0"),sQuery(id+"F0.wireOp",EDGE,"E15.66.1"),sQuery(id+"F0.wireOp",EDGE,"E15.66.2"),sQuery(id+"F0.wireOp",EDGE,"E15.66.3"),sQuery(id+"F0.wireOp",EDGE,"E15.66.4"),sQuery(id+"F0.wireOp",EDGE,"E15.66.5"),sQuery(id+"F0.wireOp",EDGE,"E15.66.6"),sQuery(id+"F0.wireOp",EDGE,"E15.66.7"),sQuery(id+"F0.wireOp",EDGE,"E15.66.8"),sQuery(id+"F0.wireOp",EDGE,"E15.66.9"),sQuery(id+"F0.wireOp",EDGE,"E15.66.10"),sQuery(id+"F0.wireOp",EDGE,"E15.66.11"),sQuery(id+"F0.wireOp",EDGE,"E15.67.0"),sQuery(id+"F0.wireOp",EDGE,"E15.67.1"),sQuery(id+"F0.wireOp",EDGE,"E15.67.2"),sQuery(id+"F0.wireOp",EDGE,"E15.67.3"),sQuery(id+"F0.wireOp",EDGE,"E15.67.4"),sQuery(id+"F0.wireOp",EDGE,"E15.67.5"),sQuery(id+"F0.wireOp",EDGE,"E15.67.6"),sQuery(id+"F0.wireOp",EDGE,"E15.67.7"),sQuery(id+"F0.wireOp",EDGE,"E15.67.8"),sQuery(id+"F0.wireOp",EDGE,"E15.67.9"),sQuery(id+"F0.wireOp",EDGE,"E15.67.10"),sQuery(id+"F0.wireOp",EDGE,"E15.67.11"),sQuery(id+"F0.wireOp",EDGE,"E15.68.0"),sQuery(id+"F0.wireOp",EDGE,"E15.68.1"),sQuery(id+"F0.wireOp",EDGE,"E15.68.2"),sQuery(id+"F0.wireOp",EDGE,"E15.68.3"),sQuery(id+"F0.wireOp",EDGE,"E15.68.4"),sQuery(id+"F0.wireOp",EDGE,"E15.68.5"),sQuery(id+"F0.wireOp",EDGE,"E15.68.6"),sQuery(id+"F0.wireOp",EDGE,"E15.68.7"),sQuery(id+"F0.wireOp",EDGE,"E15.68.8"),sQuery(id+"F0.wireOp",EDGE,"E15.68.9"),sQuery(id+"F0.wireOp",EDGE,"E15.68.10"),sQuery(id+"F0.wireOp",EDGE,"E15.68.11"),sQuery(id+"F0.wireOp",EDGE,"E15.69.0"),sQuery(id+"F0.wireOp",EDGE,"E15.69.1"),sQuery(id+"F0.wireOp",EDGE,"E15.69.2"),sQuery(id+"F0.wireOp",EDGE,"E15.69.3"),sQuery(id+"F0.wireOp",EDGE,"E15.69.4"),sQuery(id+"F0.wireOp",EDGE,"E15.69.5"),sQuery(id+"F0.wireOp",EDGE,"E15.69.6"),sQuery(id+"F0.wireOp",EDGE,"E15.69.7"),sQuery(id+"F0.wireOp",EDGE,"E15.69.8"),sQuery(id+"F0.wireOp",EDGE,"E15.69.9"),sQuery(id+"F0.wireOp",EDGE,"E15.69.10"),sQuery(id+"F0.wireOp",EDGE,"E15.69.11"),sQuery(id+"F0.wireOp",EDGE,"E15.70.0"),sQuery(id+"F0.wireOp",EDGE,"E15.70.1"),sQuery(id+"F0.wireOp",EDGE,"E15.70.2"),sQuery(id+"F0.wireOp",EDGE,"E15.70.3"),sQuery(id+"F0.wireOp",EDGE,"E15.70.4"),sQuery(id+"F0.wireOp",EDGE,"E15.70.5"),sQuery(id+"F0.wireOp",EDGE,"E15.70.6"),sQuery(id+"F0.wireOp",EDGE,"E15.70.7"),sQuery(id+"F0.wireOp",EDGE,"E15.70.8"),sQuery(id+"F0.wireOp",EDGE,"E15.70.9"),sQuery(id+"F0.wireOp",EDGE,"E15.70.10"),sQuery(id+"F0.wireOp",EDGE,"E15.70.11"),sQuery(id+"F0.wireOp",EDGE,"E15.71.0"),sQuery(id+"F0.wireOp",EDGE,"E15.71.1"),sQuery(id+"F0.wireOp",EDGE,"E15.71.2"),sQuery(id+"F0.wireOp",EDGE,"E15.71.3"),sQuery(id+"F0.wireOp",EDGE,"E15.71.4"),sQuery(id+"F0.wireOp",EDGE,"E15.71.5"),sQuery(id+"F0.wireOp",EDGE,"E15.71.6"),sQuery(id+"F0.wireOp",EDGE,"E15.71.7"),sQuery(id+"F0.wireOp",EDGE,"E15.71.8"),sQuery(id+"F0.wireOp",EDGE,"E15.71.9"),sQuery(id+"F0.wireOp",EDGE,"E15.71.10"),sQuery(id+"F0.wireOp",EDGE,"E15.71.11"),sQuery(id+"F0.wireOp",EDGE,"E16.trimOffspring"),sQuery(id+"F0.wireOp",EDGE,"E17.trimOffspring"),sQuery(id+"F0.wireOp",EDGE,"E18.trimOffspring"),sQuery(id+"F0.wireOp",EDGE,"E19.trimOffspring"),sQuery(id+"F0.wireOp",EDGE,"E20.trimOffspring"),sQuery(id+"F0.wireOp",EDGE,"E21.trimOffspring"),sQuery(id+"F0.wireOp",EDGE,"E22.trimOffspring"),sQuery(id+"F0.wireOp",EDGE,"E23.trimOffspring"),sQuery(id+"F0.wireOp",EDGE,"E24.trimOffspring"),sQuery(id+"F0.wireOp",EDGE,"E25.trimOffspring"),sQuery(id+"F0.wireOp",EDGE,"E26.trimOffspring"),sQuery(id+"F0.wireOp",EDGE,"E27.trimOffspring"),sQuery(id+"F0.wireOp",EDGE,"E28.trimOffspring"),sQuery(id+"F0.wireOp",EDGE,"E29.trimOffspring"),sQuery(id+"F0.wireOp",EDGE,"E30.trimOffspring"),sQuery(id+"F0.wireOp",EDGE,"E31.trimOffspring"),sQuery(id+"F0.wireOp",EDGE,"E32.trimOffspring"),sQuery(id+"F0.wireOp",EDGE,"E33.trimOffspring"),sQuery(id+"F0.wireOp",EDGE,"E34.trimOffspring"),sQuery(id+"F0.wireOp",EDGE,"E35.trimOffspring"),sQuery(id+"F0.wireOp",EDGE,"E36.trimOffspring"),sQuery(id+"F0.wireOp",EDGE,"E37.trimOffspring"),sQuery(id+"F0.wireOp",EDGE,"E38.trimOffspring"),sQuery(id+"F0.wireOp",EDGE,"E39.trimOffspring"),sQuery(id+"F0.wireOp",EDGE,"E40.trimOffspring"),sQuery(id+"F0.wireOp",EDGE,"E41.trimOffspring"),sQuery(id+"F0.wireOp",EDGE,"E42.trimOffspring"),sQuery(id+"F0.wireOp",EDGE,"E43.trimOffspring"),sQuery(id+"F0.wireOp",EDGE,"E44.trimOffspring"),sQuery(id+"F0.wireOp",EDGE,"E45.trimOffspring"),sQuery(id+"F0.wireOp",EDGE,"E46.trimOffspring"),sQuery(id+"F0.wireOp",EDGE,"E47.trimOffspring"),sQuery(id+"F0.wireOp",EDGE,"E48.trimOffspring"),sQuery(id+"F0.wireOp",EDGE,"E49.trimOffspring"),sQuery(id+"F0.wireOp",EDGE,"E50.trimOffspring"),sQuery(id+"F0.wireOp",EDGE,"E51.trimOffspring"),sQuery(id+"F0.wireOp",EDGE,"E52.trimOffspring"),sQuery(id+"F0.wireOp",EDGE,"E53.trimOffspring"),sQuery(id+"F0.wireOp",EDGE,"E54.trimOffspring"),sQuery(id+"F0.wireOp",EDGE,"E55.trimOffspring"),sQuery(id+"F0.wireOp",EDGE,"E56.trimOffspring"),sQuery(id+"F0.wireOp",EDGE,"E57.trimOffspring"),sQuery(id+"F0.wireOp",EDGE,"E58.trimOffspring"),sQuery(id+"F0.wireOp",EDGE,"E59.trimOffspring"),sQuery(id+"F0.wireOp",EDGE,"E60.trimOffspring"),sQuery(id+"F0.wireOp",EDGE,"E61.trimOffspring"),sQuery(id+"F0.wireOp",EDGE,"E62.trimOffspring"),sQuery(id+"F0.wireOp",EDGE,"E63.trimOffspring"),sQuery(id+"F0.wireOp",EDGE,"E64.trimOffspring"),sQuery(id+"F0.wireOp",EDGE,"E65.trimOffspring"),sQuery(id+"F0.wireOp",EDGE,"E66.trimOffspring"),sQuery(id+"F0.wireOp",EDGE,"E67.trimOffspring"),sQuery(id+"F0.wireOp",EDGE,"E68.trimOffspring"),sQuery(id+"F0.wireOp",EDGE,"E69.trimOffspring"),sQuery(id+"F0.wireOp",EDGE,"E70.trimOffspring"),sQuery(id+"F0.wireOp",EDGE,"E71.trimOffspring"),sQuery(id+"F0.wireOp",EDGE,"E72.trimOffspring"),sQuery(id+"F0.wireOp",EDGE,"E73.trimOffspring"),sQuery(id+"F0.wireOp",EDGE,"E74.trimOffspring"),sQuery(id+"F0.wireOp",EDGE,"E75.trimOffspring"),sQuery(id+"F0.wireOp",EDGE,"E76.trimOffspring"),sQuery(id+"F0.wireOp",EDGE,"E77.trimOffspring"),sQuery(id+"F0.wireOp",EDGE,"E78.trimOffspring"),sQuery(id+"F0.wireOp",EDGE,"E79.trimOffspring"),sQuery(id+"F0.wireOp",EDGE,"E80.trimOffspring"),sQuery(id+"F0.wireOp",EDGE,"E81.trimOffspring"),sQuery(id+"F0.wireOp",EDGE,"E82.trimOffspring"),sQuery(id+"F0.wireOp",EDGE,"E83.trimOffspring"),sQuery(id+"F0.wireOp",EDGE,"E84.trimOffspring"),sQuery(id+"F0.wireOp",EDGE,"E85.trimOffspring"),sQuery(id+"F0.wireOp",EDGE,"E86.trimOffspring"),sQuery(id+"F0.wireOp",EDGE,"E87")])],"isStart":false});
            var sketch = newSketch(context, id + "F2", { "sketchPlane" : qUnion([Q0])});
            skCircle(sketch, "E88.0", {"center": v(0, 0) * mm, "radius": 84.92 * mm});
            skSolve(sketch);
        }
        {
            var Q0;
            Q0 = qSketchRegion(id + "F2", true);
            extrude(context, id + "F3", {"entities" : qUnion([Q0]), "operationType" : NewBodyOperationType.ADD, "depth" : 6.35 * mm});
        }
        {
            var Q0;
            Q0=makeQuery(id+"F3.opExtrude","CAP_FACE",FACE,{"disambiguationData":[OSD([sQuery(id+"F2.wireOp",EDGE,"E88.0")])],"isStart":true});
            var sketch = newSketch(context, id + "F4", { "sketchPlane" : qUnion([Q0])});
            skCircle(sketch, "E89", {"center": v(0, 0) * mm, "radius": 6.35 * mm});
            skCircle(sketch, "E90", {"center": v(0, -50.8) * mm, "radius": 6.35 * mm});
            skCircle(sketch, "E91", {"center": v(50.8, 0) * mm, "radius": 6.35 * mm});
            skCircle(sketch, "E92", {"center": v(-50.8, 0) * mm, "radius": 6.35 * mm});
            skCircle(sketch, "E93", {"center": v(0, 50.8) * mm, "radius": 6.35 * mm});
            skSolve(sketch);
        }
        {
            var Q0;
            Q0 = qSketchRegion(id + "F4", true);
            extrude(context, id + "F5", {"entities" : qUnion([Q0]), "operationType" : NewBodyOperationType.ADD, "depth" : 6.35 * mm});
        }
    });
